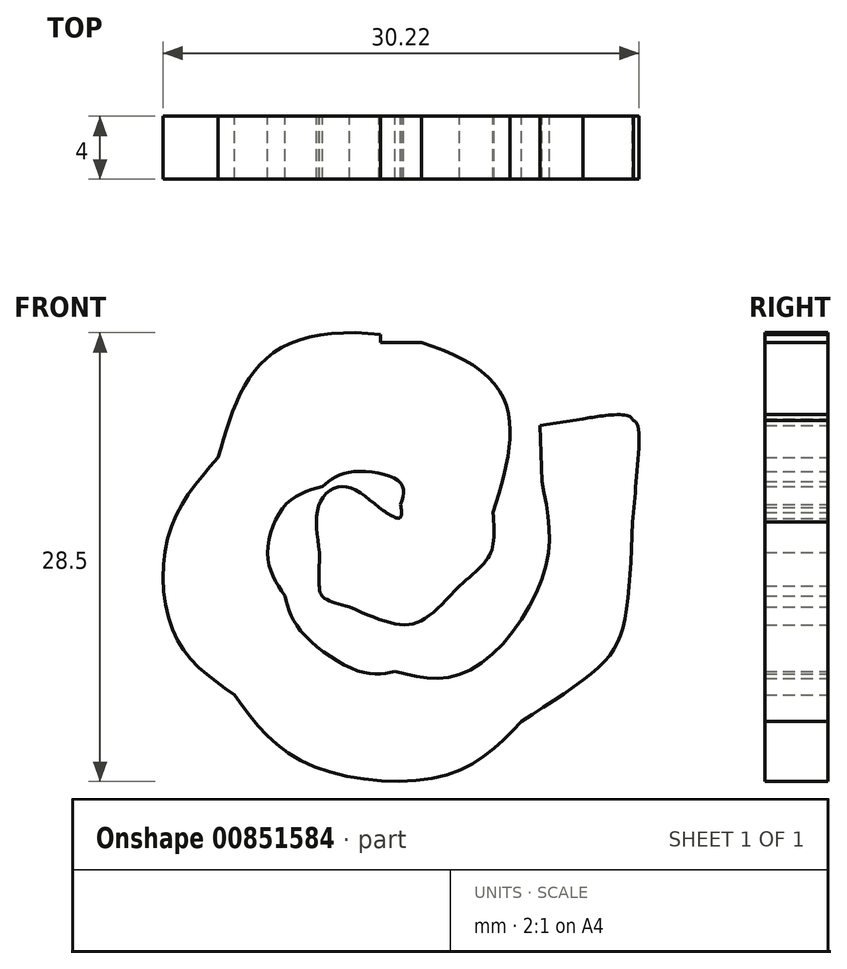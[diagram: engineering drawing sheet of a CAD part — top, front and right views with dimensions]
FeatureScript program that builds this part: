
annotation { "Feature Type Name" : "Feature", "Feature Type Description" : "" }
export const myFeature = defineFeature(function(context is Context, id is Id, definition is map)
    precondition{}
    {
        {
            var Q0;
            Q0=qCreatedBy(makeId("Front.planeOp"),FACE);
            var sketch = newSketch(context, id + "F0", { "sketchPlane" : qUnion([Q0])});
            skLineSegment(sketch, "E0", {"start": v(36.36, -139.97) * mm, "end": v(36.36, -139.97) * mm});
            skLineSegment(sketch, "E1", {"start": v(-25.94, -136.42) * mm, "end": v(-25.94, -136.42) * mm});
            skLineSegment(sketch, "E2", {"start": v(29.93, -128) * mm, "end": v(29.93, -132) * mm});
            skLineSegment(sketch, "E3", {"start": v(-29.93, -128) * mm, "end": v(-29.93, -132) * mm});
            skLineSegment(sketch, "E4", {"start": v(-29.93, -132) * mm, "end": v(29.93, -132) * mm});
            skLineSegment(sketch, "E5", {"start": v(-29.93, -128) * mm, "end": v(29.93, -128) * mm});
            skLineSegment(sketch, "E6", {"start": v(29.93, 122) * mm, "end": v(29.93, 118) * mm});
            skLineSegment(sketch, "E7", {"start": v(-29.93, 122) * mm, "end": v(-29.93, 118) * mm});
            skLineSegment(sketch, "E8", {"start": v(-29.93, 118) * mm, "end": v(29.93, 118) * mm});
            skLineSegment(sketch, "E9", {"start": v(-29.93, 122) * mm, "end": v(29.93, 122) * mm});
            skLineSegment(sketch, "E10", {"start": v(79.92, 150) * mm, "end": v(79.92, -150) * mm});
            skLineSegment(sketch, "E11", {"start": v(-79.92, 150) * mm, "end": v(-79.92, -150) * mm});
            skLineSegment(sketch, "E12", {"start": v(-79.92, -150) * mm, "end": v(79.92, -150) * mm});
            skLineSegment(sketch, "E13", {"start": v(36, -88.2) * mm, "end": v(37.81, -85.02) * mm});
            skLineSegment(sketch, "E14", {"start": v(-79.92, 150) * mm, "end": v(79.92, 150) * mm});
            skLineSegment(sketch, "E15", {"start": v(37.81, -85.02) * mm, "end": v(36.03, -83.85) * mm});
            skLineSegment(sketch, "E16", {"start": v(26.27, -98.72) * mm, "end": v(26.27, -98.72) * mm});
            skLineSegment(sketch, "E17", {"start": v(-42.53, -95.26) * mm, "end": v(-42.53, -95.26) * mm});
            skLineSegment(sketch, "E18", {"start": v(66.59, -95.3) * mm, "end": v(69.78, -95.3) * mm});
            skLineSegment(sketch, "E19", {"start": v(69.78, -95.3) * mm, "end": v(69.78, -92.14) * mm});
            skLineSegment(sketch, "E20", {"start": v(-23.5, -77.49) * mm, "end": v(-23.5, -77.49) * mm});
            skLineSegment(sketch, "E21", {"start": v(69.78, -63.28) * mm, "end": v(69.78, -63.28) * mm});
            skLineSegment(sketch, "E22", {"start": v(49.47, -48.56) * mm, "end": v(57.44, -48.58) * mm});
            skLineSegment(sketch, "E23", {"start": v(57.44, -48.58) * mm, "end": v(61.12, -45.49) * mm});
            skLineSegment(sketch, "E24", {"start": v(61.12, -45.49) * mm, "end": v(61.12, -45.49) * mm});
            skLineSegment(sketch, "E25", {"start": v(-66.72, -40.7) * mm, "end": v(-66.72, -40.7) * mm});
            skLineSegment(sketch, "E26", {"start": v(-6.36, -19.37) * mm, "end": v(-5.74, -15.94) * mm});
            skLineSegment(sketch, "E27", {"start": v(-5.74, -15.94) * mm, "end": v(-10.95, -15.85) * mm});
            skLineSegment(sketch, "E28", {"start": v(-15.96, -40.77) * mm, "end": v(-15.96, -40.77) * mm});
            skLineSegment(sketch, "E29", {"start": v(-39.28, -7.66) * mm, "end": v(-39.78, -2) * mm});
            skLineSegment(sketch, "E30", {"start": v(-39.78, -2) * mm, "end": v(-42.58, -1.59) * mm});
            skLineSegment(sketch, "E31", {"start": v(30.34, -23.6) * mm, "end": v(30.34, -23.6) * mm});
            skLineSegment(sketch, "E32", {"start": v(-30.01, -15.6) * mm, "end": v(-30.01, -15.6) * mm});
            skLineSegment(sketch, "E33", {"start": v(30.85, -8.85) * mm, "end": v(35.62, -7.69) * mm});
            skLineSegment(sketch, "E34", {"start": v(35.62, -7.69) * mm, "end": v(35.42, -4.75) * mm});
            skLineSegment(sketch, "E35", {"start": v(30.85, -8.85) * mm, "end": v(30.85, -8.85) * mm});
            skLineSegment(sketch, "E36", {"start": v(-66.78, 19.45) * mm, "end": v(-70.51, 19.45) * mm});
            skLineSegment(sketch, "E37", {"start": v(-70.51, 19.45) * mm, "end": v(-70.51, 16.65) * mm});
            skLineSegment(sketch, "E38", {"start": v(-21.63, 21.6) * mm, "end": v(-22.15, 15.83) * mm});
            skLineSegment(sketch, "E39", {"start": v(-22.15, 15.83) * mm, "end": v(-20.44, 16.3) * mm});
            skLineSegment(sketch, "E40", {"start": v(66.2, 31.38) * mm, "end": v(69.86, 31.27) * mm});
            skLineSegment(sketch, "E41", {"start": v(69.86, 31.27) * mm, "end": v(69.63, 33.78) * mm});
            skLineSegment(sketch, "E42", {"start": v(69.63, 33.78) * mm, "end": v(69.41, 36.3) * mm});
            skLineSegment(sketch, "E43", {"start": v(69.41, 36.3) * mm, "end": v(64.14, 36.3) * mm});
            skLineSegment(sketch, "E44", {"start": v(48.66, 39.8) * mm, "end": v(46.45, 40.2) * mm});
            skLineSegment(sketch, "E45", {"start": v(46.45, 40.2) * mm, "end": v(46.15, 35.79) * mm});
            skLineSegment(sketch, "E46", {"start": v(-70.51, 31.82) * mm, "end": v(-70.51, 28.39) * mm});
            skLineSegment(sketch, "E47", {"start": v(-70.51, 28.39) * mm, "end": v(-65.19, 28.4) * mm});
            skLineSegment(sketch, "E48", {"start": v(-55.9, 30.29) * mm, "end": v(-55.9, 30.29) * mm});
            skLineSegment(sketch, "E49", {"start": v(-18.1, 31.9) * mm, "end": v(-18.1, 31.9) * mm});
            skLineSegment(sketch, "E50", {"start": v(66.84, 41.57) * mm, "end": v(69.78, 41.53) * mm});
            skLineSegment(sketch, "E51", {"start": v(69.78, 41.53) * mm, "end": v(69.78, 45.61) * mm});
            skLineSegment(sketch, "E52", {"start": v(33.23, 47.48) * mm, "end": v(38.92, 47.78) * mm});
            skLineSegment(sketch, "E53", {"start": v(38.92, 47.78) * mm, "end": v(38.48, 50.36) * mm});
            skLineSegment(sketch, "E54", {"start": v(33.93, 65.25) * mm, "end": v(33.93, 65.25) * mm});
            skLineSegment(sketch, "E55", {"start": v(69.78, 74.16) * mm, "end": v(69.78, 77.16) * mm});
            skLineSegment(sketch, "E56", {"start": v(69.78, 77.16) * mm, "end": v(65.5, 76.74) * mm});
            skLineSegment(sketch, "E57", {"start": v(32.65, 87.45) * mm, "end": v(32.06, 85.77) * mm});
            skLineSegment(sketch, "E58", {"start": v(32.06, 85.77) * mm, "end": v(31.62, 87.42) * mm});
            skLineSegment(sketch, "E59", {"start": v(-17.07, 113.15) * mm, "end": v(-19.78, 112.74) * mm});
            skLineSegment(sketch, "E60", {"start": v(-19.78, 112.74) * mm, "end": v(-19.68, 109.18) * mm});
            skLineSegment(sketch, "E61", {"start": v(68.13, 110) * mm, "end": v(66.47, 112.94) * mm});
            skLineSegment(sketch, "E62", {"start": v(66.47, 112.94) * mm, "end": v(68.13, 115.64) * mm});
            skLineSegment(sketch, "E63", {"start": v(-43.22, 137.14) * mm, "end": v(-44.94, 140.4) * mm});
            skLineSegment(sketch, "E64", {"start": v(-44.94, 140.4) * mm, "end": v(-49.28, 140.4) * mm});
            skLineSegment(sketch, "E65", {"start": v(24.63, 136.8) * mm, "end": v(22.84, 140.4) * mm});
            skLineSegment(sketch, "E66", {"start": v(22.84, 140.4) * mm, "end": v(18.03, 140.4) * mm});
            skLineSegment(sketch, "E67", {"start": v(-2.29, 140.4) * mm, "end": v(-8.25, 140.4) * mm});
            skLineSegment(sketch, "E68", {"start": v(-8.25, 140.4) * mm, "end": v(-7.7, 138.51) * mm});
            skLineSegment(sketch, "E69", {"start": v(-21.3, 140.06) * mm, "end": v(-28.12, 140.06) * mm});
            skLineSegment(sketch, "E70", {"start": v(-28.12, 140.06) * mm, "end": v(-30.35, 137.47) * mm});
            skLineSegment(sketch, "E71", {"start": v(64.64, 137.41) * mm, "end": v(64.64, 140.4) * mm});
            skLineSegment(sketch, "E72", {"start": v(64.64, 140.4) * mm, "end": v(61.7, 140.4) * mm});
            skLineSegment(sketch, "E73", {"start": v(56.95, 136.32) * mm, "end": v(56.95, 136.32) * mm});
            skFitSpline(sketch, "E74", {"points": [v(-44.8, -139.2) * mm, v(-44.8, -136.21) * mm, v(-55.8, -134.8) * mm, v(-60.05, -137.22) * mm]});
            skFitSpline(sketch, "E75", {"points": [v(-60.05, -137.22) * mm, v(-64.45, -139.73) * mm, v(-63.24, -140.32) * mm, v(-53.62, -140.32) * mm]});
            skFitSpline(sketch, "E76", {"points": [v(-53.62, -140.32) * mm, v(-45.94, -140.32) * mm, v(-44.8, -140.18) * mm, v(-44.8, -139.2) * mm]});
            skFitSpline(sketch, "E77", {"points": [v(-34.52, -139.77) * mm, v(-34.52, -138.62) * mm, v(-36.01, -137.23) * mm, v(-37.24, -137.23) * mm]});
            skFitSpline(sketch, "E78", {"points": [v(-37.24, -137.23) * mm, v(-38.23, -137.23) * mm, v(-38.57, -139.4) * mm, v(-37.7, -140.2) * mm]});
            skFitSpline(sketch, "E79", {"points": [v(-37.7, -140.2) * mm, v(-36.84, -141.01) * mm, v(-34.52, -140.7) * mm, v(-34.52, -139.77) * mm]});
            skFitSpline(sketch, "E80", {"points": [v(-8.08, -139.18) * mm, v(-8.08, -137.4) * mm, v(-14.2, -134.92) * mm, v(-17.58, -135.35) * mm]});
            skFitSpline(sketch, "E81", {"points": [v(-17.58, -135.35) * mm, v(-20.96, -135.77) * mm, v(-24.24, -137.67) * mm, v(-24.24, -139.2) * mm]});
            skFitSpline(sketch, "E82", {"points": [v(-24.24, -139.2) * mm, v(-24.24, -140.17) * mm, v(-23.15, -140.32) * mm, v(-16.16, -140.32) * mm]});
            skFitSpline(sketch, "E83", {"points": [v(-16.16, -140.32) * mm, v(-9.12, -140.32) * mm, v(-8.08, -140.17) * mm, v(-8.08, -139.18) * mm]});
            skFitSpline(sketch, "E84", {"points": [v(-1.6, -139.47) * mm, v(-1.98, -137.68) * mm, v(-4.4, -137.48) * mm, v(-4.4, -139.24) * mm]});
            skFitSpline(sketch, "E85", {"points": [v(-4.4, -139.24) * mm, v(-4.4, -140.22) * mm, v(-3.94, -140.66) * mm, v(-2.88, -140.66) * mm]});
            skFitSpline(sketch, "E86", {"points": [v(-2.88, -140.66) * mm, v(-1.83, -140.66) * mm, v(-1.44, -140.3) * mm, v(-1.6, -139.47) * mm]});
            skFitSpline(sketch, "E87", {"points": [v(16.13, -139.33) * mm, v(17.1, -137.64) * mm, v(17.11, -135.85) * mm, v(16.14, -135.85) * mm]});
            skFitSpline(sketch, "E88", {"points": [v(16.14, -135.85) * mm, v(14.72, -135.85) * mm, v(9.5, -139.34) * mm, v(9.93, -140) * mm]});
            skFitSpline(sketch, "E89", {"points": [v(9.93, -140) * mm, v(10.76, -141.25) * mm, v(15.32, -140.76) * mm, v(16.13, -139.33) * mm]});
            skFitSpline(sketch, "E90", {"points": [v(28.28, -138.93) * mm, v(29.71, -137.34) * mm, v(32.67, -135.85) * mm, v(34.41, -135.85) * mm]});
            skFitSpline(sketch, "E91", {"points": [v(34.41, -135.85) * mm, v(35.47, -135.85) * mm, v(37.12, -136.78) * mm, v(38.5, -138.15) * mm]});
            skFitSpline(sketch, "E92", {"points": [v(38.5, -138.15) * mm, v(40.14, -139.78) * mm, v(41.5, -140.46) * mm, v(43.18, -140.5) * mm]});
            skFitSpline(sketch, "E93", {"points": [v(43.18, -140.5) * mm, v(45.3, -140.57) * mm, v(45.54, -140.37) * mm, v(45.54, -138.6) * mm]});
            skFitSpline(sketch, "E94", {"points": [v(45.54, -138.6) * mm, v(45.54, -136.35) * mm, v(42.67, -132.84) * mm, v(39.61, -131.36) * mm]});
            skFitSpline(sketch, "E95", {"points": [v(39.61, -131.36) * mm, v(36.24, -129.73) * mm, v(30.19, -130.06) * mm, v(27.05, -132.05) * mm]});
            skFitSpline(sketch, "E96", {"points": [v(27.05, -132.05) * mm, v(24.23, -133.85) * mm, v(21.3, -137.66) * mm, v(21.3, -139.55) * mm]});
            skFitSpline(sketch, "E97", {"points": [v(21.3, -139.55) * mm, v(21.3, -140.5) * mm, v(21.81, -140.6) * mm, v(24.42, -140.22) * mm]});
            skFitSpline(sketch, "E98", {"points": [v(24.42, -140.22) * mm, v(26.14, -139.96) * mm, v(27.87, -139.38) * mm, v(28.28, -138.93) * mm]});
            skFitSpline(sketch, "E99", {"points": [v(36.36, -139.97) * mm, v(36.92, -139.13) * mm, v(34.9, -138.3) * mm, v(33.81, -138.93) * mm]});
            skFitSpline(sketch, "E100", {"points": [v(33.81, -138.93) * mm, v(33.38, -139.18) * mm, v(33.22, -139.67) * mm, v(33.45, -140.02) * mm]});
            skFitSpline(sketch, "E101", {"points": [v(33.45, -140.02) * mm, v(34.01, -140.87) * mm, v(35.79, -140.84) * mm, v(36.36, -139.97) * mm]});
            skFitSpline(sketch, "E102", {"points": [v(-66.85, -137.74) * mm, v(-64.38, -135.2) * mm, v(-64.05, -133.8) * mm, v(-65.92, -133.78) * mm]});
            skFitSpline(sketch, "E103", {"points": [v(-65.92, -133.78) * mm, v(-66.63, -133.78) * mm, v(-67.95, -133.59) * mm, v(-68.86, -133.36) * mm]});
            skFitSpline(sketch, "E104", {"points": [v(-68.86, -133.36) * mm, v(-70.42, -132.97) * mm, v(-70.51, -133.15) * mm, v(-70.51, -136.46) * mm]});
            skFitSpline(sketch, "E105", {"points": [v(-70.51, -136.46) * mm, v(-70.51, -138.4) * mm, v(-70.18, -139.98) * mm, v(-69.77, -139.98) * mm]});
            skFitSpline(sketch, "E106", {"points": [v(-69.77, -139.98) * mm, v(-69.36, -139.98) * mm, v(-68.05, -138.97) * mm, v(-66.85, -137.74) * mm]});
            skFitSpline(sketch, "E107", {"points": [v(54.12, -138.46) * mm, v(55.46, -138) * mm, v(56.56, -137.32) * mm, v(56.56, -136.93) * mm]});
            skFitSpline(sketch, "E108", {"points": [v(56.56, -136.93) * mm, v(56.56, -135.48) * mm, v(51.75, -126.95) * mm, v(50.92, -126.94) * mm]});
            skFitSpline(sketch, "E109", {"points": [v(50.92, -126.94) * mm, v(50.25, -126.92) * mm, v(47.2, -128.2) * mm, v(44.87, -129.49) * mm]});
            skFitSpline(sketch, "E110", {"points": [v(44.87, -129.49) * mm, v(44.17, -129.87) * mm, v(49.68, -139.2) * mm, v(50.63, -139.25) * mm]});
            skFitSpline(sketch, "E111", {"points": [v(50.63, -139.25) * mm, v(51.2, -139.27) * mm, v(52.78, -138.92) * mm, v(54.12, -138.46) * mm]});
            skFitSpline(sketch, "E112", {"points": [v(-25.94, -136.42) * mm, v(-23.41, -134.2) * mm, v(-23.7, -132.42) * mm, v(-26.57, -132.42) * mm]});
            skFitSpline(sketch, "E113", {"points": [v(-26.57, -132.42) * mm, v(-29.63, -132.42) * mm, v(-34.96, -127.4) * mm, v(-35.67, -123.84) * mm]});
            skFitSpline(sketch, "E114", {"points": [v(-35.67, -123.84) * mm, v(-36.58, -119.29) * mm, v(-32.7, -114.56) * mm, v(-28.04, -114.55) * mm]});
            skFitSpline(sketch, "E115", {"points": [v(-28.04, -114.55) * mm, v(-25.94, -114.55) * mm, v(-22.04, -118.06) * mm, v(-22.04, -119.95) * mm]});
            skFitSpline(sketch, "E116", {"points": [v(-22.04, -119.95) * mm, v(-22.04, -121.63) * mm, v(-23.9, -123.5) * mm, v(-25.58, -123.46) * mm]});
            skFitSpline(sketch, "E117", {"points": [v(-25.58, -123.46) * mm, v(-26.7, -123.44) * mm, v(-26.7, -123.38) * mm, v(-25.52, -122.74) * mm]});
            skFitSpline(sketch, "E118", {"points": [v(-25.52, -122.74) * mm, v(-23.9, -121.85) * mm, v(-23.8, -118.29) * mm, v(-25.4, -117.72) * mm]});
            skFitSpline(sketch, "E119", {"points": [v(-25.4, -117.72) * mm, v(-28.94, -116.44) * mm, v(-32.32, -118.93) * mm, v(-32.32, -122.82) * mm]});
            skFitSpline(sketch, "E120", {"points": [v(-18.36, -125.92) * mm, v(-15.89, -123.41) * mm, v(-15.73, -117.03) * mm, v(-18.06, -114.08) * mm]});
            skFitSpline(sketch, "E121", {"points": [v(-18.06, -114.08) * mm, v(-20.81, -110.61) * mm, v(-24.04, -109.05) * mm, v(-28.48, -109.05) * mm]});
            skFitSpline(sketch, "E122", {"points": [v(-28.48, -109.05) * mm, v(-33.5, -109.05) * mm, v(-36.53, -110.68) * mm, v(-39.61, -115.04) * mm]});
            skFitSpline(sketch, "E123", {"points": [v(-39.61, -115.04) * mm, v(-44.52, -121.97) * mm, v(-41.67, -129.93) * mm, v(-31.95, -136.4) * mm]});
            skFitSpline(sketch, "E124", {"points": [v(-31.95, -136.4) * mm, v(-29.15, -138.27) * mm, v(-28.05, -138.27) * mm, v(-25.94, -136.42) * mm]});
            skFitSpline(sketch, "E125", {"points": [v(69.78, -134.48) * mm, v(69.78, -132.43) * mm, v(69.48, -131.73) * mm, v(68.62, -131.73) * mm]});
            skFitSpline(sketch, "E126", {"points": [v(68.62, -131.73) * mm, v(66.72, -131.73) * mm, v(63.31, -128) * mm, v(62.78, -125.34) * mm]});
            skFitSpline(sketch, "E127", {"points": [v(62.78, -125.34) * mm, v(62.2, -122.41) * mm, v(64.15, -119.3) * mm, v(67.63, -117.61) * mm]});
            skFitSpline(sketch, "E128", {"points": [v(67.63, -117.61) * mm, v(69.38, -116.77) * mm, v(69.78, -116.13) * mm, v(69.78, -114.19) * mm]});
            skFitSpline(sketch, "E129", {"points": [v(69.78, -114.19) * mm, v(69.78, -112.35) * mm, v(69.47, -111.8) * mm, v(68.46, -111.8) * mm]});
            skFitSpline(sketch, "E130", {"points": [v(68.46, -111.8) * mm, v(66.32, -111.8) * mm, v(60.8, -114.75) * mm, v(59.27, -116.7) * mm]});
            skFitSpline(sketch, "E131", {"points": [v(59.27, -116.7) * mm, v(56.34, -120.47) * mm, v(56.77, -129.54) * mm, v(60.05, -133.2) * mm]});
            skFitSpline(sketch, "E132", {"points": [v(60.05, -133.2) * mm, v(62.14, -135.5) * mm, v(65.46, -137.16) * mm, v(68.13, -137.2) * mm]});
            skFitSpline(sketch, "E133", {"points": [v(68.13, -137.2) * mm, v(69.57, -137.22) * mm, v(69.78, -136.88) * mm, v(69.78, -134.48) * mm]});
            skFitSpline(sketch, "E134", {"points": [v(10.65, -133.04) * mm, v(14.55, -130.57) * mm, v(17.16, -125.17) * mm, v(16.74, -120.43) * mm]});
            skFitSpline(sketch, "E135", {"points": [v(16.74, -120.43) * mm, v(16.47, -117.36) * mm, v(15.87, -116.05) * mm, v(13.33, -112.96) * mm]});
            skFitSpline(sketch, "E136", {"points": [v(13.33, -112.96) * mm, v(10.85, -109.96) * mm, v(9.24, -108.8) * mm, v(5.18, -107.1) * mm]});
            skFitSpline(sketch, "E137", {"points": [v(5.18, -107.1) * mm, v(-2.45, -103.9) * mm, v(-3.27, -103.82) * mm, v(-7.2, -105.8) * mm]});
            skFitSpline(sketch, "E138", {"points": [v(-7.2, -105.8) * mm, v(-9.1, -106.75) * mm, v(-12.06, -107.75) * mm, v(-13.77, -108) * mm]});
            skFitSpline(sketch, "E139", {"points": [v(-13.77, -108) * mm, v(-15.49, -108.27) * mm, v(-16.9, -108.7) * mm, v(-16.9, -108.94) * mm]});
            skFitSpline(sketch, "E140", {"points": [v(-16.9, -108.94) * mm, v(-16.92, -109.92) * mm, v(-12.82, -117.95) * mm, v(-12.3, -117.97) * mm]});
            skFitSpline(sketch, "E141", {"points": [v(-12.3, -117.97) * mm, v(-11.98, -117.98) * mm, v(-10.33, -116.64) * mm, v(-8.62, -114.98) * mm]});
            skFitSpline(sketch, "E142", {"points": [v(-8.62, -114.98) * mm, v(-4.52, -111.03) * mm, v(-1.24, -110.39) * mm, v(3.55, -112.62) * mm]});
            skFitSpline(sketch, "E143", {"points": [v(3.55, -112.62) * mm, v(6.95, -114.2) * mm, v(9.93, -117.47) * mm, v(10.75, -120.54) * mm]});
            skFitSpline(sketch, "E144", {"points": [v(10.75, -120.54) * mm, v(11.4, -122.96) * mm, v(9.63, -126.16) * mm, v(6.58, -128.05) * mm]});
            skFitSpline(sketch, "E145", {"points": [v(6.58, -128.05) * mm, v(3.97, -129.67) * mm, v(3.7, -129.7) * mm, v(1.18, -128.71) * mm]});
            skFitSpline(sketch, "E146", {"points": [v(1.18, -128.71) * mm, v(-2.1, -127.43) * mm, v(-3.53, -124.9) * mm, v(-2.34, -122.45) * mm]});
            skFitSpline(sketch, "E147", {"points": [v(-2.34, -122.45) * mm, v(-1.88, -121.5) * mm, v(-0.93, -120.73) * mm, v(-0.24, -120.73) * mm]});
            skFitSpline(sketch, "E148", {"points": [v(-0.24, -120.73) * mm, v(0.75, -120.73) * mm, v(0.83, -120.92) * mm, v(0.15, -121.56) * mm]});
            skFitSpline(sketch, "E149", {"points": [v(0.15, -121.56) * mm, v(-0.34, -122.01) * mm, v(-0.73, -123.24) * mm, v(-0.73, -124.3) * mm]});
            skFitSpline(sketch, "E150", {"points": [v(-0.73, -124.3) * mm, v(-0.73, -128.48) * mm, v(5.94, -127.14) * mm, v(6.87, -122.77) * mm]});
            skFitSpline(sketch, "E151", {"points": [v(6.87, -122.77) * mm, v(8.06, -117.23) * mm, v(2.16, -113) * mm, v(-3.34, -115.46) * mm]});
            skFitSpline(sketch, "E152", {"points": [v(-3.34, -115.46) * mm, v(-8.23, -117.64) * mm, v(-10.35, -124.2) * mm, v(-7.71, -128.98) * mm]});
            skFitSpline(sketch, "E153", {"points": [v(-7.71, -128.98) * mm, v(-6.51, -131.15) * mm, v(-2.7, -134.12) * mm, v(-0.37, -134.7) * mm]});
            skFitSpline(sketch, "E154", {"points": [v(-0.37, -134.7) * mm, v(2.72, -135.49) * mm, v(8.05, -134.68) * mm, v(10.65, -133.04) * mm]});
            skFitSpline(sketch, "E155", {"points": [v(-42.6, -132.59) * mm, v(-42.61, -132.3) * mm, v(-43.43, -130.53) * mm, v(-44.42, -128.64) * mm]});
            skFitSpline(sketch, "E156", {"points": [v(-44.42, -128.64) * mm, v(-45.41, -126.75) * mm, v(-46.24, -124.81) * mm, v(-46.25, -124.34) * mm]});
            skFitSpline(sketch, "E157", {"points": [v(-46.25, -124.34) * mm, v(-46.28, -123.35) * mm, v(-48.48, -123.15) * mm, v(-48.48, -124.15) * mm]});
            skFitSpline(sketch, "E158", {"points": [v(-48.48, -124.15) * mm, v(-48.48, -124.51) * mm, v(-49.47, -125.87) * mm, v(-50.68, -127.16) * mm]});
            skFitSpline(sketch, "E159", {"points": [v(-50.68, -127.16) * mm, v(-53.41, -130.07) * mm, v(-53.46, -131.03) * mm, v(-50.86, -131.07) * mm]});
            skFitSpline(sketch, "E160", {"points": [v(-50.86, -131.07) * mm, v(-49.75, -131.1) * mm, v(-47.85, -131.53) * mm, v(-46.64, -132.05) * mm]});
            skFitSpline(sketch, "E161", {"points": [v(-46.64, -132.05) * mm, v(-44.11, -133.13) * mm, v(-42.6, -133.33) * mm, v(-42.6, -132.59) * mm]});
            skFitSpline(sketch, "E162", {"points": [v(25.96, -128.25) * mm, v(28.43, -125.78) * mm, v(28.35, -125.09) * mm, v(25.35, -123.31) * mm]});
            skFitSpline(sketch, "E163", {"points": [v(25.35, -123.31) * mm, v(22.99, -120.8) * mm, v(22.31, -120.93) * mm, v(21.8, -124) * mm]});
            skFitSpline(sketch, "E164", {"points": [v(21.8, -124) * mm, v(21.57, -125.42) * mm, v(21.16, -127.27) * mm, v(20.89, -128.12) * mm]});
            skFitSpline(sketch, "E165", {"points": [v(-57.95, -127.41) * mm, v(-54.6, -125.3) * mm, v(-51.45, -119.84) * mm, v(-51.43, -116.07) * mm]});
            skFitSpline(sketch, "E166", {"points": [v(-51.43, -116.07) * mm, v(-51.4, -109.92) * mm, v(-56.36, -104.23) * mm, v(-64.32, -101.31) * mm]});
            skFitSpline(sketch, "E167", {"points": [v(-64.32, -101.31) * mm, v(-67.14, -100.28) * mm, v(-69.69, -99.43) * mm, v(-69.98, -99.43) * mm]});
            skFitSpline(sketch, "E168", {"points": [v(-69.98, -99.43) * mm, v(-70.27, -99.43) * mm, v(-70.51, -100.98) * mm, v(-70.51, -102.87) * mm]});
            skFitSpline(sketch, "E169", {"points": [v(-70.51, -102.87) * mm, v(-70.51, -106.24) * mm, v(-70.47, -106.3) * mm, v(-68.27, -106.3) * mm]});
            skFitSpline(sketch, "E170", {"points": [v(-68.27, -106.3) * mm, v(-65.03, -106.3) * mm, v(-61.98, -108.01) * mm, v(-59.48, -111.24) * mm]});
            skFitSpline(sketch, "E171", {"points": [v(-59.48, -111.24) * mm, v(-56.92, -114.54) * mm, v(-56.74, -116.64) * mm, v(-58.74, -119.67) * mm]});
            skFitSpline(sketch, "E172", {"points": [v(-58.74, -119.67) * mm, v(-61.2, -123.4) * mm, v(-63.4, -124) * mm, v(-68.86, -122.43) * mm]});
            skFitSpline(sketch, "E173", {"points": [v(-68.86, -122.43) * mm, v(-70.4, -121.98) * mm, v(-70.51, -122.15) * mm, v(-70.51, -125.06) * mm]});
            skFitSpline(sketch, "E174", {"points": [v(-70.51, -125.06) * mm, v(-70.51, -128.66) * mm, v(-70.21, -128.85) * mm, v(-64.56, -128.93) * mm]});
            skFitSpline(sketch, "E175", {"points": [v(-64.56, -128.93) * mm, v(-61.43, -128.97) * mm, v(-59.85, -128.6) * mm, v(-57.95, -127.41) * mm]});
            skFitSpline(sketch, "E176", {"points": [v(69.78, -124.86) * mm, v(69.78, -121.7) * mm, v(69.53, -120.73) * mm, v(68.7, -120.73) * mm]});
            skFitSpline(sketch, "E177", {"points": [v(68.7, -120.73) * mm, v(66.66, -120.73) * mm, v(65.38, -125.03) * mm, v(66.55, -127.9) * mm]});
            skFitSpline(sketch, "E178", {"points": [v(66.55, -127.9) * mm, v(66.8, -128.5) * mm, v(67.62, -128.98) * mm, v(68.39, -128.98) * mm]});
            skFitSpline(sketch, "E179", {"points": [v(68.39, -128.98) * mm, v(69.6, -128.98) * mm, v(69.78, -128.45) * mm, v(69.78, -124.86) * mm]});
            skFitSpline(sketch, "E180", {"points": [v(48.78, -123.28) * mm, v(50.92, -122.17) * mm, v(52.28, -120.7) * mm, v(53.9, -117.7) * mm]});
            skFitSpline(sketch, "E181", {"points": [v(53.9, -117.7) * mm, v(55.37, -114.99) * mm, v(57.14, -112.96) * mm, v(59.27, -111.56) * mm]});
            skFitSpline(sketch, "E182", {"points": [v(59.27, -111.56) * mm, v(61, -110.41) * mm, v(62.43, -109.13) * mm, v(62.43, -108.71) * mm]});
            skFitSpline(sketch, "E183", {"points": [v(62.43, -108.71) * mm, v(62.43, -108.3) * mm, v(60.8, -107.4) * mm, v(58.8, -106.73) * mm]});
            skFitSpline(sketch, "E184", {"points": [v(58.8, -106.73) * mm, v(56.8, -106.06) * mm, v(54.78, -105.07) * mm, v(54.3, -104.53) * mm]});
            skFitSpline(sketch, "E185", {"points": [v(54.3, -104.53) * mm, v(53.83, -104) * mm, v(52.96, -103.55) * mm, v(52.37, -103.55) * mm]});
            skFitSpline(sketch, "E186", {"points": [v(52.37, -103.55) * mm, v(51.52, -103.55) * mm, v(51.4, -104.27) * mm, v(51.8, -107.23) * mm]});
            skFitSpline(sketch, "E187", {"points": [v(51.8, -107.23) * mm, v(52.64, -113.53) * mm, v(48.58, -118.79) * mm, v(42.16, -119.73) * mm]});
            skFitSpline(sketch, "E188", {"points": [v(42.16, -119.73) * mm, v(40.58, -119.97) * mm, v(38.39, -119.83) * mm, v(37.28, -119.43) * mm]});
            skFitSpline(sketch, "E189", {"points": [v(37.28, -119.43) * mm, v(33.46, -118.06) * mm, v(31.16, -112.36) * mm, v(33.07, -109.01) * mm]});
            skFitSpline(sketch, "E190", {"points": [v(33.07, -109.01) * mm, v(34.07, -107.27) * mm, v(37.93, -105.44) * mm, v(39.58, -105.94) * mm]});
            skFitSpline(sketch, "E191", {"points": [v(39.58, -105.94) * mm, v(41.31, -106.45) * mm, v(42.95, -109.35) * mm, v(42.17, -110.53) * mm]});
            skFitSpline(sketch, "E192", {"points": [v(42.17, -110.53) * mm, v(41.73, -111.2) * mm, v(41.45, -110.98) * mm, v(41.13, -109.73) * mm]});
            skFitSpline(sketch, "E193", {"points": [v(41.13, -109.73) * mm, v(40.6, -107.58) * mm, v(37.6, -107) * mm, v(36.22, -108.77) * mm]});
            skFitSpline(sketch, "E194", {"points": [v(36.22, -108.77) * mm, v(33.7, -112) * mm, v(36.63, -116.61) * mm, v(41.2, -116.61) * mm]});
            skFitSpline(sketch, "E195", {"points": [v(41.2, -116.61) * mm, v(46.26, -116.61) * mm, v(49.09, -113.34) * mm, v(48.13, -108.57) * mm]});
            skFitSpline(sketch, "E196", {"points": [v(48.13, -108.57) * mm, v(46.97, -102.76) * mm, v(44.09, -100.43) * mm, v(38.2, -100.51) * mm]});
            skFitSpline(sketch, "E197", {"points": [v(38.2, -100.51) * mm, v(34.02, -100.57) * mm, v(30.4, -102.4) * mm, v(28.03, -105.65) * mm]});
            skFitSpline(sketch, "E198", {"points": [v(28.03, -105.65) * mm, v(26.56, -107.68) * mm, v(26.35, -108.68) * mm, v(26.58, -112.63) * mm]});
            skFitSpline(sketch, "E199", {"points": [v(26.58, -112.63) * mm, v(26.8, -116.4) * mm, v(27.26, -117.78) * mm, v(29.05, -120.19) * mm]});
            skFitSpline(sketch, "E200", {"points": [v(29.05, -120.19) * mm, v(32.26, -124.49) * mm, v(35.24, -125.73) * mm, v(41.12, -125.2) * mm]});
            skFitSpline(sketch, "E201", {"points": [v(41.12, -125.2) * mm, v(43.9, -124.96) * mm, v(47.08, -124.16) * mm, v(48.78, -123.28) * mm]});
            skFitSpline(sketch, "E202", {"points": [v(-62.34, -119.6) * mm, v(-61.78, -118.97) * mm, v(-61.33, -117.13) * mm, v(-61.33, -115.5) * mm]});
            skFitSpline(sketch, "E203", {"points": [v(-61.33, -115.5) * mm, v(-61.33, -111.65) * mm, v(-63.38, -109.6) * mm, v(-67.32, -109.48) * mm]});
            skFitSpline(sketch, "E204", {"points": [v(-67.32, -109.48) * mm, v(-70.13, -109.4) * mm, v(-70.15, -109.4) * mm, v(-70.37, -112.32) * mm]});
            skFitSpline(sketch, "E205", {"points": [v(-70.37, -112.32) * mm, v(-70.57, -114.87) * mm, v(-70.4, -115.24) * mm, v(-69.1, -115.24) * mm]});
            skFitSpline(sketch, "E206", {"points": [v(-69.1, -115.24) * mm, v(-67.78, -115.24) * mm, v(-67.7, -115.44) * mm, v(-68.42, -116.91) * mm]});
            skFitSpline(sketch, "E207", {"points": [v(-68.42, -116.91) * mm, v(-68.87, -117.83) * mm, v(-69.04, -119.07) * mm, v(-68.8, -119.66) * mm]});
            skFitSpline(sketch, "E208", {"points": [v(-68.8, -119.66) * mm, v(-68.2, -121.12) * mm, v(-63.65, -121.08) * mm, v(-62.34, -119.6) * mm]});
            skFitSpline(sketch, "E209", {"points": [v(-44.8, -113.86) * mm, v(-44.8, -113.49) * mm, v(-43.59, -111.92) * mm, v(-42.1, -110.38) * mm]});
            skFitSpline(sketch, "E210", {"points": [v(-42.1, -110.38) * mm, v(-39.35, -107.53) * mm, v(-35.79, -105.5) * mm, v(-32.13, -104.67) * mm]});
            skFitSpline(sketch, "E211", {"points": [v(-32.13, -104.67) * mm, v(-29.44, -104.06) * mm, v(-29.59, -103.09) * mm, v(-32.83, -99.98) * mm]});
            skFitSpline(sketch, "E212", {"points": [v(-32.83, -99.98) * mm, v(-35.95, -97) * mm, v(-36.86, -96.83) * mm, v(-39.48, -98.76) * mm]});
            skFitSpline(sketch, "E213", {"points": [v(-39.48, -98.76) * mm, v(-42.08, -100.67) * mm, v(-48.74, -102.39) * mm, v(-51.43, -101.83) * mm]});
            skFitSpline(sketch, "E214", {"points": [v(-51.43, -101.83) * mm, v(-54.27, -101.25) * mm, v(-54.23, -102.1) * mm, v(-51.22, -105.8) * mm]});
            skFitSpline(sketch, "E215", {"points": [v(-51.22, -105.8) * mm, v(-49.9, -107.4) * mm, v(-48.36, -110.04) * mm, v(-47.8, -111.64) * mm]});
            skFitSpline(sketch, "E216", {"points": [v(-47.8, -111.64) * mm, v(-47.24, -113.24) * mm, v(-46.33, -114.55) * mm, v(-45.79, -114.55) * mm]});
            skFitSpline(sketch, "E217", {"points": [v(-45.79, -114.55) * mm, v(-45.25, -114.55) * mm, v(-44.8, -114.24) * mm, v(-44.8, -113.86) * mm]});
            skFitSpline(sketch, "E218", {"points": [v(21.55, -111.29) * mm, v(21.8, -109.5) * mm, v(22.2, -107.38) * mm, v(22.43, -106.6) * mm]});
            skFitSpline(sketch, "E219", {"points": [v(22.43, -106.6) * mm, v(22.84, -105.27) * mm, v(22.57, -105.19) * mm, v(18.05, -105.19) * mm]});
            skFitSpline(sketch, "E220", {"points": [v(18.05, -105.19) * mm, v(13.88, -105.19) * mm, v(13.22, -105.36) * mm, v(13.22, -106.43) * mm]});
            skFitSpline(sketch, "E221", {"points": [v(13.22, -106.43) * mm, v(13.22, -107.12) * mm, v(13.51, -107.68) * mm, v(13.86, -107.68) * mm]});
            skFitSpline(sketch, "E222", {"points": [v(13.86, -107.68) * mm, v(14.22, -107.68) * mm, v(15.62, -109.22) * mm, v(16.99, -111.1) * mm]});
            skFitSpline(sketch, "E223", {"points": [v(16.99, -111.1) * mm, v(18.35, -112.98) * mm, v(19.83, -114.52) * mm, v(20.28, -114.53) * mm]});
            skFitSpline(sketch, "E224", {"points": [v(20.28, -114.53) * mm, v(20.73, -114.54) * mm, v(21.3, -113.08) * mm, v(21.55, -111.29) * mm]});
            skFitSpline(sketch, "E225", {"points": [v(-12.38, -103.54) * mm, v(-6.82, -102.1) * mm, v(-2.31, -94.9) * mm, v(-3.18, -88.85) * mm]});
            skFitSpline(sketch, "E226", {"points": [v(-3.18, -88.85) * mm, v(-4.2, -81.69) * mm, v(-13.12, -77.28) * mm, v(-19.93, -80.58) * mm]});
            skFitSpline(sketch, "E227", {"points": [v(-19.93, -80.58) * mm, v(-24.29, -82.69) * mm, v(-25.79, -90.49) * mm, v(-22.44, -93.62) * mm]});
            skFitSpline(sketch, "E228", {"points": [v(-22.44, -93.62) * mm, v(-19.85, -96.04) * mm, v(-15.36, -95.98) * mm, v(-13.27, -93.5) * mm]});
            skFitSpline(sketch, "E229", {"points": [v(-13.27, -93.5) * mm, v(-11.45, -91.33) * mm, v(-11.32, -88.94) * mm, v(-12.94, -87.42) * mm]});
            skFitSpline(sketch, "E230", {"points": [v(-12.94, -87.42) * mm, v(-14.5, -85.97) * mm, v(-16.28, -86.33) * mm, v(-17.33, -88.3) * mm]});
            skFitSpline(sketch, "E231", {"points": [v(-17.33, -88.3) * mm, v(-18.03, -89.63) * mm, v(-18.25, -89.7) * mm, v(-18.63, -88.78) * mm]});
            skFitSpline(sketch, "E232", {"points": [v(-18.63, -88.78) * mm, v(-19.1, -87.61) * mm, v(-16.17, -84.31) * mm, v(-14.65, -84.31) * mm]});
            skFitSpline(sketch, "E233", {"points": [v(-14.65, -84.31) * mm, v(-12.98, -84.31) * mm, v(-8.81, -88.95) * mm, v(-8.81, -90.8) * mm]});
            skFitSpline(sketch, "E234", {"points": [v(-8.81, -90.8) * mm, v(-8.81, -93.54) * mm, v(-10.76, -96.52) * mm, v(-13.35, -97.77) * mm]});
            skFitSpline(sketch, "E235", {"points": [v(-13.35, -97.77) * mm, v(-20.39, -101.18) * mm, v(-29.5, -93.36) * mm, v(-28.28, -84.98) * mm]});
            skFitSpline(sketch, "E236", {"points": [v(-28.28, -84.98) * mm, v(-27.88, -82.32) * mm, v(-28.06, -81.28) * mm, v(-29.13, -79.9) * mm]});
            skFitSpline(sketch, "E237", {"points": [v(-29.13, -79.9) * mm, v(-31.55, -76.8) * mm, v(-32.41, -77.63) * mm, v(-31.88, -82.52) * mm]});
            skFitSpline(sketch, "E238", {"points": [v(-31.88, -82.52) * mm, v(-31.52, -85.81) * mm, v(-31.72, -87.88) * mm, v(-32.7, -90.78) * mm]});
            skFitSpline(sketch, "E239", {"points": [v(-32.7, -90.78) * mm, v(-33.95, -94.51) * mm, v(-33.95, -94.69) * mm, v(-32.62, -96.06) * mm]});
            skFitSpline(sketch, "E240", {"points": [v(-32.62, -96.06) * mm, v(-28.46, -100.37) * mm, v(-22.6, -103.13) * mm, v(-15.42, -104.18) * mm]});
            skFitSpline(sketch, "E241", {"points": [v(-15.42, -104.18) * mm, v(-15.22, -104.2) * mm, v(-13.85, -103.92) * mm, v(-12.38, -103.54) * mm]});
            skFitSpline(sketch, "E242", {"points": [v(68.86, -103.56) * mm, v(69.42, -103.56) * mm, v(69.78, -102.61) * mm, v(69.78, -101.15) * mm]});
            skFitSpline(sketch, "E243", {"points": [v(69.78, -101.15) * mm, v(69.78, -98.86) * mm, v(69.65, -98.74) * mm, v(67.23, -98.74) * mm]});
            skFitSpline(sketch, "E244", {"points": [v(67.23, -98.74) * mm, v(63.48, -98.74) * mm, v(59.86, -96.84) * mm, v(58.13, -93.96) * mm]});
            skFitSpline(sketch, "E245", {"points": [v(58.13, -93.96) * mm, v(56.86, -91.84) * mm, v(56.73, -91.01) * mm, v(57.34, -88.93) * mm]});
            skFitSpline(sketch, "E246", {"points": [v(57.34, -88.93) * mm, v(58.62, -84.58) * mm, v(64.45, -81.96) * mm, v(66.84, -84.66) * mm]});
            skFitSpline(sketch, "E247", {"points": [v(66.84, -84.66) * mm, v(68.63, -86.67) * mm, v(69.78, -85.86) * mm, v(69.78, -82.58) * mm]});
            skFitSpline(sketch, "E248", {"points": [v(69.78, -82.58) * mm, v(69.78, -79.87) * mm, v(69.53, -79.38) * mm, v(67.9, -78.8) * mm]});
            skFitSpline(sketch, "E249", {"points": [v(67.9, -78.8) * mm, v(63.29, -77.16) * mm, v(57.72, -78.5) * mm, v(54.07, -82.13) * mm]});
            skFitSpline(sketch, "E250", {"points": [v(54.07, -82.13) * mm, v(49.74, -86.44) * mm, v(50.97, -98.01) * mm, v(56.1, -101.16) * mm]});
            skFitSpline(sketch, "E251", {"points": [v(56.1, -101.16) * mm, v(58.54, -102.65) * mm, v(64.6, -104.23) * mm, v(66.47, -103.86) * mm]});
            skFitSpline(sketch, "E252", {"points": [v(66.47, -103.86) * mm, v(67.28, -103.7) * mm, v(68.35, -103.57) * mm, v(68.86, -103.56) * mm]});
            skFitSpline(sketch, "E253", {"points": [v(5.88, -100.78) * mm, v(5.88, -99.64) * mm, v(2.75, -96) * mm, v(1.78, -96) * mm]});
            skFitSpline(sketch, "E254", {"points": [v(1.78, -96) * mm, v(0.87, -96) * mm, v(0, -97.49) * mm, v(0, -99.04) * mm]});
            skFitSpline(sketch, "E255", {"points": [v(0, -99.04) * mm, v(0, -100) * mm, v(2.6, -101.37) * mm, v(4.6, -101.45) * mm]});
            skFitSpline(sketch, "E256", {"points": [v(4.6, -101.45) * mm, v(5.3, -101.47) * mm, v(5.88, -101.17) * mm, v(5.88, -100.78) * mm]});
            skFitSpline(sketch, "E257", {"points": [v(26.27, -98.72) * mm, v(30.25, -96.58) * mm, v(32.85, -93.77) * mm, v(36, -88.2) * mm]});
            skFitSpline(sketch, "E258", {"points": [v(36.03, -83.85) * mm, v(35.05, -83.2) * mm, v(33.65, -82.12) * mm, v(32.91, -81.43) * mm]});
            skFitSpline(sketch, "E259", {"points": [v(32.91, -81.43) * mm, v(30.8, -79.47) * mm, v(30.11, -79.95) * mm, v(30.11, -83.4) * mm]});
            skFitSpline(sketch, "E260", {"points": [v(30.11, -83.4) * mm, v(30.11, -89.29) * mm, v(24.35, -95.3) * mm, v(18.72, -95.3) * mm]});
            skFitSpline(sketch, "E261", {"points": [v(18.72, -95.3) * mm, v(16.5, -95.3) * mm, v(11.82, -91.28) * mm, v(11.67, -89.25) * mm]});
            skFitSpline(sketch, "E262", {"points": [v(11.67, -89.25) * mm, v(11.41, -85.74) * mm, v(13.29, -82.76) * mm, v(16.33, -81.86) * mm]});
            skFitSpline(sketch, "E263", {"points": [v(16.33, -81.86) * mm, v(17.92, -81.38) * mm, v(20.57, -83.26) * mm, v(20.57, -84.87) * mm]});
            skFitSpline(sketch, "E264", {"points": [v(20.57, -84.87) * mm, v(20.57, -85.73) * mm, v(20.33, -85.7) * mm, v(19.15, -84.7) * mm]});
            skFitSpline(sketch, "E265", {"points": [v(19.15, -84.7) * mm, v(16.82, -82.73) * mm, v(15.1, -83.56) * mm, v(14.84, -86.78) * mm]});
            skFitSpline(sketch, "E266", {"points": [v(14.84, -86.78) * mm, v(14.58, -90.02) * mm, v(15.54, -91.07) * mm, v(19.26, -91.63) * mm]});
            skFitSpline(sketch, "E267", {"points": [v(19.26, -91.63) * mm, v(21.25, -91.93) * mm, v(22.22, -91.64) * mm, v(24.1, -90.16) * mm]});
            skFitSpline(sketch, "E268", {"points": [v(24.1, -90.16) * mm, v(26.13, -88.56) * mm, v(26.44, -87.88) * mm, v(26.44, -85.03) * mm]});
            skFitSpline(sketch, "E269", {"points": [v(26.44, -85.03) * mm, v(26.44, -82.25) * mm, v(26.06, -81.34) * mm, v(23.98, -79.22) * mm]});
            skFitSpline(sketch, "E270", {"points": [v(23.98, -79.22) * mm, v(14.84, -69.89) * mm, v(0.2, -83.45) * mm, v(7.4, -94.55) * mm]});
            skFitSpline(sketch, "E271", {"points": [v(7.4, -94.55) * mm, v(8.18, -95.74) * mm, v(10.36, -97.63) * mm, v(12.26, -98.76) * mm]});
            skFitSpline(sketch, "E272", {"points": [v(12.26, -98.76) * mm, v(16.95, -101.54) * mm, v(21.03, -101.53) * mm, v(26.27, -98.72) * mm]});
            skFitSpline(sketch, "E273", {"points": [v(47.4, -97.2) * mm, v(47.12, -96.35) * mm, v(46.54, -94.1) * mm, v(46.12, -92.22) * mm]});
            skFitSpline(sketch, "E274", {"points": [v(46.12, -92.22) * mm, v(45.7, -90.33) * mm, v(44.83, -88.4) * mm, v(44.2, -87.92) * mm]});
            skFitSpline(sketch, "E275", {"points": [v(44.2, -87.92) * mm, v(41.85, -86.16) * mm, v(40.53, -86.94) * mm, v(38.23, -91.45) * mm]});
            skFitSpline(sketch, "E276", {"points": [v(38.23, -91.45) * mm, v(37, -93.87) * mm, v(36, -96.04) * mm, v(36, -96.27) * mm]});
            skFitSpline(sketch, "E277", {"points": [v(36, -96.27) * mm, v(36, -96.5) * mm, v(37.06, -96.7) * mm, v(38.38, -96.72) * mm]});
            skFitSpline(sketch, "E278", {"points": [v(38.38, -96.72) * mm, v(39.7, -96.74) * mm, v(41.92, -97.17) * mm, v(43.34, -97.67) * mm]});
            skFitSpline(sketch, "E279", {"points": [v(43.34, -97.67) * mm, v(47.28, -99.07) * mm, v(48, -98.98) * mm, v(47.4, -97.2) * mm]});
            skFitSpline(sketch, "E280", {"points": [v(-60.96, -96.75) * mm, v(-60.96, -96.41) * mm, v(-61.79, -94.79) * mm, v(-62.8, -93.14) * mm]});
            skFitSpline(sketch, "E281", {"points": [v(-62.8, -93.14) * mm, v(-63.8, -91.5) * mm, v(-64.62, -89.61) * mm, v(-64.63, -88.95) * mm]});
            skFitSpline(sketch, "E282", {"points": [v(-64.63, -88.95) * mm, v(-64.64, -87.45) * mm, v(-66.34, -87.4) * mm, v(-68.7, -88.86) * mm]});
            skFitSpline(sketch, "E283", {"points": [v(-68.7, -88.86) * mm, v(-70, -89.65) * mm, v(-70.51, -90.59) * mm, v(-70.5, -92.12) * mm]});
            skFitSpline(sketch, "E284", {"points": [v(-70.5, -92.12) * mm, v(-70.5, -94.07) * mm, v(-70.13, -94.41) * mm, v(-66.65, -95.74) * mm]});
            skFitSpline(sketch, "E285", {"points": [v(-66.65, -95.74) * mm, v(-62.27, -97.4) * mm, v(-60.96, -97.64) * mm, v(-60.96, -96.75) * mm]});
            skFitSpline(sketch, "E286", {"points": [v(-42.53, -95.26) * mm, v(-39.46, -93.21) * mm, v(-36.78, -89) * mm, v(-36.25, -85.35) * mm]});
            skFitSpline(sketch, "E287", {"points": [v(-36.25, -85.35) * mm, v(-35.69, -81.55) * mm, v(-38.4, -75.88) * mm, v(-42.3, -72.68) * mm]});
            skFitSpline(sketch, "E288", {"points": [v(-42.3, -72.68) * mm, v(-45.65, -69.92) * mm, v(-51.58, -67.13) * mm, v(-54.1, -67.13) * mm]});
            skFitSpline(sketch, "E289", {"points": [v(-54.1, -67.13) * mm, v(-55.2, -67.13) * mm, v(-57.54, -66.48) * mm, v(-59.3, -65.68) * mm]});
            skFitSpline(sketch, "E290", {"points": [v(-59.3, -65.68) * mm, v(-61.07, -64.88) * mm, v(-62.73, -64.43) * mm, v(-62.99, -64.68) * mm]});
            skFitSpline(sketch, "E291", {"points": [v(-62.99, -64.68) * mm, v(-63.25, -64.92) * mm, v(-63.04, -66.12) * mm, v(-62.51, -67.33) * mm]});
            skFitSpline(sketch, "E292", {"points": [v(-62.51, -67.33) * mm, v(-61.99, -68.54) * mm, v(-61.23, -70.85) * mm, v(-60.83, -72.46) * mm]});
            skFitSpline(sketch, "E293", {"points": [v(-60.83, -72.46) * mm, v(-60.44, -74.06) * mm, v(-59.85, -75.38) * mm, v(-59.53, -75.38) * mm]});
            skFitSpline(sketch, "E294", {"points": [v(-59.53, -75.38) * mm, v(-59.2, -75.38) * mm, v(-57.7, -74.9) * mm, v(-56.17, -74.3) * mm]});
            skFitSpline(sketch, "E295", {"points": [v(-56.17, -74.3) * mm, v(-53.63, -73.3) * mm, v(-53.13, -73.3) * mm, v(-50.22, -74.34) * mm]});
            skFitSpline(sketch, "E296", {"points": [v(-50.22, -74.34) * mm, v(-46.49, -75.68) * mm, v(-43.7, -78.52) * mm, v(-42.52, -82.23) * mm]});
            skFitSpline(sketch, "E297", {"points": [v(-42.52, -82.23) * mm, v(-41.79, -84.53) * mm, v(-41.86, -85.2) * mm, v(-43.05, -87.1) * mm]});
            skFitSpline(sketch, "E298", {"points": [v(-43.05, -87.1) * mm, v(-43.81, -88.32) * mm, v(-45.56, -89.87) * mm, v(-46.92, -90.56) * mm]});
            skFitSpline(sketch, "E299", {"points": [v(-46.92, -90.56) * mm, v(-49.07, -91.63) * mm, v(-49.73, -91.68) * mm, v(-51.7, -90.93) * mm]});
            skFitSpline(sketch, "E300", {"points": [v(-51.7, -90.93) * mm, v(-54.87, -89.72) * mm, v(-56.4, -87.06) * mm, v(-55.25, -84.72) * mm]});
            skFitSpline(sketch, "E301", {"points": [v(-55.25, -84.72) * mm, v(-54.78, -83.74) * mm, v(-53.84, -82.94) * mm, v(-53.18, -82.94) * mm]});
            skFitSpline(sketch, "E302", {"points": [v(-53.18, -82.94) * mm, v(-52.2, -82.94) * mm, v(-52.14, -83.13) * mm, v(-52.85, -83.93) * mm]});
            skFitSpline(sketch, "E303", {"points": [v(-52.85, -83.93) * mm, v(-54.03, -85.26) * mm, v(-53.56, -87.77) * mm, v(-51.96, -88.7) * mm]});
            skFitSpline(sketch, "E304", {"points": [v(-51.96, -88.7) * mm, v(-50.98, -89.28) * mm, v(-50.2, -89.22) * mm, v(-48.71, -88.44) * mm]});
            skFitSpline(sketch, "E305", {"points": [v(-48.71, -88.44) * mm, v(-43.13, -85.49) * mm, v(-45.97, -76.75) * mm, v(-52.51, -76.75) * mm]});
            skFitSpline(sketch, "E306", {"points": [v(-52.51, -76.75) * mm, v(-54.56, -76.75) * mm, v(-55.83, -77.35) * mm, v(-58.24, -79.45) * mm]});
            skFitSpline(sketch, "E307", {"points": [v(-58.24, -79.45) * mm, v(-61.19, -82.03) * mm, v(-61.33, -82.34) * mm, v(-61.33, -86.15) * mm]});
            skFitSpline(sketch, "E308", {"points": [v(-61.33, -86.15) * mm, v(-61.33, -91.03) * mm, v(-59.3, -94.13) * mm, v(-54.8, -96.1) * mm]});
            skFitSpline(sketch, "E309", {"points": [v(-54.8, -96.1) * mm, v(-51.04, -97.75) * mm, v(-45.72, -97.38) * mm, v(-42.53, -95.26) * mm]});
            skFitSpline(sketch, "E310", {"points": [v(69.78, -92.14) * mm, v(69.78, -89.33) * mm, v(69.61, -89) * mm, v(68.35, -89.31) * mm]});
            skFitSpline(sketch, "E311", {"points": [v(68.35, -89.31) * mm, v(67.23, -89.59) * mm, v(66.87, -89.26) * mm, v(66.7, -87.85) * mm]});
            skFitSpline(sketch, "E312", {"points": [v(66.7, -87.85) * mm, v(66.52, -86.45) * mm, v(66.01, -85.98) * mm, v(64.5, -85.82) * mm]});
            skFitSpline(sketch, "E313", {"points": [v(64.5, -85.82) * mm, v(61.9, -85.54) * mm, v(59.84, -88.26) * mm, v(60.57, -91) * mm]});
            skFitSpline(sketch, "E314", {"points": [v(60.57, -91) * mm, v(61.4, -94.13) * mm, v(63.06, -95.3) * mm, v(66.59, -95.3) * mm]});
            skFitSpline(sketch, "E315", {"points": [v(47.74, -84.06) * mm, v(47.74, -83.55) * mm, v(48.4, -82.34) * mm, v(49.21, -81.38) * mm]});
            skFitSpline(sketch, "E316", {"points": [v(49.21, -81.38) * mm, v(50.02, -80.42) * mm, v(50.68, -79.33) * mm, v(50.68, -78.96) * mm]});
            skFitSpline(sketch, "E317", {"points": [v(50.68, -78.96) * mm, v(50.68, -78.6) * mm, v(48.86, -78.16) * mm, v(46.64, -77.98) * mm]});
            skFitSpline(sketch, "E318", {"points": [v(46.64, -77.98) * mm, v(42.07, -77.63) * mm, v(39.72, -76.06) * mm, v(37.39, -71.8) * mm]});
            skFitSpline(sketch, "E319", {"points": [v(37.39, -71.8) * mm, v(35.26, -67.92) * mm, v(35.58, -65.98) * mm, v(38.84, -62.93) * mm]});
            skFitSpline(sketch, "E320", {"points": [v(38.84, -62.93) * mm, v(40.41, -61.46) * mm, v(42.31, -60.26) * mm, v(43.07, -60.26) * mm]});
            skFitSpline(sketch, "E321", {"points": [v(43.07, -60.26) * mm, v(45.34, -60.27) * mm, v(49.14, -62.85) * mm, v(49.65, -64.73) * mm]});
            skFitSpline(sketch, "E322", {"points": [v(49.65, -64.73) * mm, v(50.18, -66.72) * mm, v(48.32, -69.2) * mm, v(46.34, -69.17) * mm]});
            skFitSpline(sketch, "E323", {"points": [v(46.34, -69.17) * mm, v(45.33, -69.15) * mm, v(45.34, -69.03) * mm, v(46.46, -68.24) * mm]});
            skFitSpline(sketch, "E324", {"points": [v(46.46, -68.24) * mm, v(48.47, -66.81) * mm, v(48.13, -63.81) * mm, v(45.9, -63.3) * mm]});
            skFitSpline(sketch, "E325", {"points": [v(45.9, -63.3) * mm, v(42.18, -62.42) * mm, v(38.89, -66.2) * mm, v(39.94, -70.14) * mm]});
            skFitSpline(sketch, "E326", {"points": [v(39.94, -70.14) * mm, v(40.81, -73.38) * mm, v(42.95, -75.02) * mm, v(46.19, -74.94) * mm]});
            skFitSpline(sketch, "E327", {"points": [v(46.19, -74.94) * mm, v(54.47, -74.74) * mm, v(58.63, -65.76) * mm, v(53.4, -59.36) * mm]});
            skFitSpline(sketch, "E328", {"points": [v(53.4, -59.36) * mm, v(49.97, -55.15) * mm, v(42.98, -53.46) * mm, v(38.34, -55.73) * mm]});
            skFitSpline(sketch, "E329", {"points": [v(38.34, -55.73) * mm, v(33.73, -57.99) * mm, v(30.11, -63.32) * mm, v(30.11, -67.88) * mm]});
            skFitSpline(sketch, "E330", {"points": [v(30.11, -67.88) * mm, v(30.11, -73.55) * mm, v(34.43, -79.06) * mm, v(41.87, -82.9) * mm]});
            skFitSpline(sketch, "E331", {"points": [v(41.87, -82.9) * mm, v(46.33, -85.2) * mm, v(47.74, -85.47) * mm, v(47.74, -84.06) * mm]});
            skFitSpline(sketch, "E332", {"points": [v(2.53, -81.63) * mm, v(3.14, -80.54) * mm, v(4.96, -78.57) * mm, v(6.6, -77.27) * mm]});
            skFitSpline(sketch, "E333", {"points": [v(6.6, -77.27) * mm, v(8.22, -75.97) * mm, v(9.55, -74.59) * mm, v(9.55, -74.2) * mm]});
            skFitSpline(sketch, "E334", {"points": [v(9.55, -74.2) * mm, v(9.55, -73.81) * mm, v(8.27, -73.3) * mm, v(6.7, -73.07) * mm]});
            skFitSpline(sketch, "E335", {"points": [v(6.7, -73.07) * mm, v(5.14, -72.83) * mm, v(2.17, -71.56) * mm, v(0.1, -70.23) * mm]});
            skFitSpline(sketch, "E336", {"points": [v(0.1, -70.23) * mm, v(-1.95, -68.9) * mm, v(-3.99, -67.82) * mm, v(-4.41, -67.82) * mm]});
            skFitSpline(sketch, "E337", {"points": [v(-4.41, -67.82) * mm, v(-4.84, -67.82) * mm, v(-6.19, -68.89) * mm, v(-7.41, -70.2) * mm]});
            skFitSpline(sketch, "E338", {"points": [v(-7.41, -70.2) * mm, v(-8.64, -71.5) * mm, v(-10.28, -72.75) * mm, v(-11.06, -72.99) * mm]});
            skFitSpline(sketch, "E339", {"points": [v(-11.06, -72.99) * mm, v(-13.55, -73.73) * mm, v(-12.58, -74.98) * mm, v(-7.89, -77.1) * mm]});
            skFitSpline(sketch, "E340", {"points": [v(-7.89, -77.1) * mm, v(-4.96, -78.42) * mm, v(-2.8, -79.95) * mm, v(-1.85, -81.37) * mm]});
            skFitSpline(sketch, "E341", {"points": [v(-1.85, -81.37) * mm, v(0, -84.12) * mm, v(1.12, -84.19) * mm, v(2.53, -81.63) * mm]});
            skFitSpline(sketch, "E342", {"points": [v(-66.98, -80.27) * mm, v(-64.81, -76.67) * mm, v(-64.81, -71.34) * mm, v(-66.98, -67.74) * mm]});
            skFitSpline(sketch, "E343", {"points": [v(-66.98, -67.74) * mm, v(-69.86, -62.94) * mm, v(-70.51, -64.1) * mm, v(-70.51, -74) * mm]});
            skFitSpline(sketch, "E344", {"points": [v(-70.51, -74) * mm, v(-70.51, -83.92) * mm, v(-69.86, -85.07) * mm, v(-66.98, -80.27) * mm]});
            skFitSpline(sketch, "E345", {"points": [v(-23.5, -77.49) * mm, v(-23.5, -77.13) * mm, v(-22.84, -76.65) * mm, v(-22.04, -76.4) * mm]});
            skFitSpline(sketch, "E346", {"points": [v(-22.04, -76.4) * mm, v(-20.12, -75.84) * mm, v(-20.14, -73.54) * mm, v(-22.06, -72.97) * mm]});
            skFitSpline(sketch, "E347", {"points": [v(-22.06, -72.97) * mm, v(-24.03, -72.38) * mm, v(-26.95, -68.13) * mm, v(-27.56, -64.97) * mm]});
            skFitSpline(sketch, "E348", {"points": [v(-27.56, -64.97) * mm, v(-28.48, -60.2) * mm, v(-24.26, -55.45) * mm, v(-19.11, -55.45) * mm]});
            skFitSpline(sketch, "E349", {"points": [v(-19.11, -55.45) * mm, v(-16.9, -55.45) * mm, v(-13.22, -59.06) * mm, v(-13.22, -61.24) * mm]});
            skFitSpline(sketch, "E350", {"points": [v(-13.22, -61.24) * mm, v(-13.22, -62.96) * mm, v(-15.46, -65.76) * mm, v(-16.85, -65.76) * mm]});
            skFitSpline(sketch, "E351", {"points": [v(-16.85, -65.76) * mm, v(-18.33, -65.76) * mm, v(-18.43, -64.27) * mm, v(-16.97, -63.91) * mm]});
            skFitSpline(sketch, "E352", {"points": [v(-16.97, -63.91) * mm, v(-14.84, -63.4) * mm, v(-14.83, -59.92) * mm, v(-16.96, -58.85) * mm]});
            skFitSpline(sketch, "E353", {"points": [v(-16.96, -58.85) * mm, v(-18.83, -57.92) * mm, v(-22.45, -59.1) * mm, v(-23.53, -61) * mm]});
            skFitSpline(sketch, "E354", {"points": [v(-23.53, -61) * mm, v(-24.57, -62.82) * mm, v(-24.4, -66.24) * mm, v(-23.14, -68.51) * mm]});
            skFitSpline(sketch, "E355", {"points": [v(-23.14, -68.51) * mm, v(-20.77, -72.8) * mm, v(-11.38, -71.45) * mm, v(-8.59, -66.43) * mm]});
            skFitSpline(sketch, "E356", {"points": [v(-8.59, -66.43) * mm, v(-5.74, -61.31) * mm, v(-8.47, -53.64) * mm, v(-14.11, -50.9) * mm]});
            skFitSpline(sketch, "E357", {"points": [v(-14.11, -50.9) * mm, v(-17.68, -49.18) * mm, v(-23.95, -49.87) * mm, v(-27.72, -52.4) * mm]});
            skFitSpline(sketch, "E358", {"points": [v(-27.72, -52.4) * mm, v(-32.06, -55.3) * mm, v(-33.06, -57.25) * mm, v(-33.04, -62.77) * mm]});
            skFitSpline(sketch, "E359", {"points": [v(-33.04, -62.77) * mm, v(-33.02, -67.82) * mm, v(-31.57, -71.75) * mm, v(-28.2, -75.88) * mm]});
            skFitSpline(sketch, "E360", {"points": [v(-28.2, -75.88) * mm, v(-26.51, -77.95) * mm, v(-23.5, -78.98) * mm, v(-23.5, -77.49) * mm]});
            skFitSpline(sketch, "E361", {"points": [v(27.91, -75.08) * mm, v(27.91, -74.53) * mm, v(27.6, -73.9) * mm, v(27.22, -73.69) * mm]});
            skFitSpline(sketch, "E362", {"points": [v(27.22, -73.69) * mm, v(26.84, -73.47) * mm, v(26.3, -71.9) * mm, v(26.03, -70.2) * mm]});
            skFitSpline(sketch, "E363", {"points": [v(26.03, -70.2) * mm, v(25.46, -66.61) * mm, v(24.54, -66.39) * mm, v(21.72, -69.14) * mm]});
            skFitSpline(sketch, "E364", {"points": [v(21.72, -69.14) * mm, v(19.29, -71.52) * mm, v(19.4, -72.01) * mm, v(22.77, -74.25) * mm]});
            skFitSpline(sketch, "E365", {"points": [v(22.77, -74.25) * mm, v(25.69, -76.18) * mm, v(27.91, -76.54) * mm, v(27.91, -75.08) * mm]});
            skFitSpline(sketch, "E366", {"points": [v(69.78, -73.06) * mm, v(69.78, -71.06) * mm, v(69.5, -70.69) * mm, v(67.68, -70.35) * mm]});
            skFitSpline(sketch, "E367", {"points": [v(67.68, -70.35) * mm, v(66.52, -70.13) * mm, v(64.57, -69.16) * mm, v(63.35, -68.2) * mm]});
            skFitSpline(sketch, "E368", {"points": [v(63.35, -68.2) * mm, v(60.9, -66.28) * mm, v(59.5, -65.96) * mm, v(59.5, -67.33) * mm]});
            skFitSpline(sketch, "E369", {"points": [v(59.5, -67.33) * mm, v(59.5, -67.82) * mm, v(58.83, -69.43) * mm, v(58.03, -70.91) * mm]});
            skFitSpline(sketch, "E370", {"points": [v(58.03, -70.91) * mm, v(56.03, -74.58) * mm, v(56.14, -74.87) * mm, v(59.31, -74.42) * mm]});
            skFitSpline(sketch, "E371", {"points": [v(59.31, -74.42) * mm, v(60.83, -74.2) * mm, v(63.22, -74.3) * mm, v(64.64, -74.63) * mm]});
            skFitSpline(sketch, "E372", {"points": [v(64.64, -74.63) * mm, v(69.33, -75.74) * mm, v(69.78, -75.6) * mm, v(69.78, -73.06) * mm]});
            skFitSpline(sketch, "E373", {"points": [v(-37, -68.34) * mm, v(-37.24, -67.48) * mm, v(-37.44, -65.32) * mm, v(-37.45, -63.52) * mm]});
            skFitSpline(sketch, "E374", {"points": [v(-37.45, -63.52) * mm, v(-37.46, -61.37) * mm, v(-37.77, -60.27) * mm, v(-38.38, -60.28) * mm]});
            skFitSpline(sketch, "E375", {"points": [v(-38.38, -60.28) * mm, v(-39.44, -60.3) * mm, v(-44.8, -64.8) * mm, v(-44.8, -65.67) * mm]});
            skFitSpline(sketch, "E376", {"points": [v(-44.8, -65.67) * mm, v(-44.8, -66.57) * mm, v(-39.48, -69.8) * mm, v(-37.92, -69.84) * mm]});
            skFitSpline(sketch, "E377", {"points": [v(-37.92, -69.84) * mm, v(-36.86, -69.87) * mm, v(-36.65, -69.54) * mm, v(-37, -68.34) * mm]});
            skFitSpline(sketch, "E378", {"points": [v(15.2, -67.68) * mm, v(21.47, -65.16) * mm, v(23.5, -62.04) * mm, v(23.5, -54.92) * mm]});
            skFitSpline(sketch, "E379", {"points": [v(23.5, -54.92) * mm, v(23.5, -50.06) * mm, v(21.04, -42.4) * mm, v(19.48, -42.4) * mm]});
            skFitSpline(sketch, "E380", {"points": [v(19.48, -42.4) * mm, v(17.79, -42.4) * mm, v(13.96, -43.9) * mm, v(13.96, -44.57) * mm]});
            skFitSpline(sketch, "E381", {"points": [v(13.96, -44.57) * mm, v(13.96, -44.93) * mm, v(14.75, -46.22) * mm, v(15.73, -47.42) * mm]});
            skFitSpline(sketch, "E382", {"points": [v(15.73, -47.42) * mm, v(18.28, -50.56) * mm, v(18.81, -54.15) * mm, v(17.29, -57.89) * mm]});
            skFitSpline(sketch, "E383", {"points": [v(17.29, -57.89) * mm, v(15.8, -61.5) * mm, v(13.8, -63) * mm, v(10.44, -63) * mm]});
            skFitSpline(sketch, "E384", {"points": [v(10.44, -63) * mm, v(7.21, -63) * mm, v(5.4, -62.04) * mm, v(4.05, -59.59) * mm]});
            skFitSpline(sketch, "E385", {"points": [v(4.05, -59.59) * mm, v(2.51, -56.8) * mm, v(2.65, -55.66) * mm, v(4.77, -53.67) * mm]});
            skFitSpline(sketch, "E386", {"points": [v(4.77, -53.67) * mm, v(6.37, -52.17) * mm, v(6.8, -52.07) * mm, v(8.26, -52.82) * mm]});
            skFitSpline(sketch, "E387", {"points": [v(8.26, -52.82) * mm, v(9.9, -53.67) * mm, v(9.9, -53.68) * mm, v(7.71, -54.05) * mm]});
            skFitSpline(sketch, "E388", {"points": [v(7.71, -54.05) * mm, v(5.27, -54.47) * mm, v(4.34, -56.81) * mm, v(5.9, -58.58) * mm]});
            skFitSpline(sketch, "E389", {"points": [v(5.9, -58.58) * mm, v(7.15, -59.98) * mm, v(12, -59.85) * mm, v(13.42, -58.37) * mm]});
            skFitSpline(sketch, "E390", {"points": [v(13.42, -58.37) * mm, v(16.44, -55.23) * mm, v(15.48, -49.34) * mm, v(11.71, -47.88) * mm]});
            skFitSpline(sketch, "E391", {"points": [v(11.71, -47.88) * mm, v(8.46, -46.62) * mm, v(2.54, -47.36) * mm, v(0.34, -49.3) * mm]});
            skFitSpline(sketch, "E392", {"points": [v(0.34, -49.3) * mm, v(-4.7, -53.71) * mm, v(-3.16, -63.56) * mm, v(3.11, -67.14) * mm]});
            skFitSpline(sketch, "E393", {"points": [v(3.11, -67.14) * mm, v(5.87, -68.7) * mm, v(11.97, -68.98) * mm, v(15.2, -67.68) * mm]});
            skFitSpline(sketch, "E394", {"points": [v(69.78, -63.28) * mm, v(69.78, -61.64) * mm, v(69.16, -60.11) * mm, v(67.94, -58.76) * mm]});
            skFitSpline(sketch, "E395", {"points": [v(67.94, -58.76) * mm, v(66.9, -57.61) * mm, v(66.1, -55.85) * mm, v(66.1, -54.73) * mm]});
            skFitSpline(sketch, "E396", {"points": [v(66.1, -54.73) * mm, v(66.1, -53.36) * mm, v(66.68, -52.38) * mm, v(67.94, -51.6) * mm]});
            skFitSpline(sketch, "E397", {"points": [v(67.94, -51.6) * mm, v(70.38, -50.11) * mm, v(70.63, -45.83) * mm, v(68.27, -45.83) * mm]});
            skFitSpline(sketch, "E398", {"points": [v(68.27, -45.83) * mm, v(65.82, -45.83) * mm, v(62.54, -47.77) * mm, v(61.34, -49.93) * mm]});
            skFitSpline(sketch, "E399", {"points": [v(61.34, -49.93) * mm, v(59.92, -52.5) * mm, v(59.91, -57.7) * mm, v(61.32, -60.23) * mm]});
            skFitSpline(sketch, "E400", {"points": [v(61.32, -60.23) * mm, v(62.62, -62.6) * mm, v(66.7, -65.74) * mm, v(68.5, -65.75) * mm]});
            skFitSpline(sketch, "E401", {"points": [v(68.5, -65.75) * mm, v(69.48, -65.76) * mm, v(69.78, -65.19) * mm, v(69.78, -63.28) * mm]});
            skFitSpline(sketch, "E402", {"points": [v(-47.02, -61.3) * mm, v(-43.78, -59.73) * mm, v(-42.6, -57.66) * mm, v(-42.6, -53.55) * mm]});
            skFitSpline(sketch, "E403", {"points": [v(-42.6, -53.55) * mm, v(-42.6, -46.85) * mm, v(-46.3, -43.45) * mm, v(-51.75, -45.13) * mm]});
            skFitSpline(sketch, "E404", {"points": [v(-51.75, -45.13) * mm, v(-54.76, -46.06) * mm, v(-55.82, -47.54) * mm, v(-55.82, -50.8) * mm]});
            skFitSpline(sketch, "E405", {"points": [v(-55.82, -50.8) * mm, v(-55.82, -53.6) * mm, v(-54.72, -54.76) * mm, v(-52.05, -54.76) * mm]});
            skFitSpline(sketch, "E406", {"points": [v(-52.05, -54.76) * mm, v(-49.94, -54.76) * mm, v(-48.64, -52.83) * mm, v(-49.64, -51.16) * mm]});
            skFitSpline(sketch, "E407", {"points": [v(-49.64, -51.16) * mm, v(-49.92, -50.69) * mm, v(-49.58, -50.8) * mm, v(-48.87, -51.42) * mm]});
            skFitSpline(sketch, "E408", {"points": [v(-48.87, -51.42) * mm, v(-47.16, -52.93) * mm, v(-47.98, -55.17) * mm, v(-50.73, -56.5) * mm]});
            skFitSpline(sketch, "E409", {"points": [v(-50.73, -56.5) * mm, v(-52.66, -57.44) * mm, v(-53.11, -57.44) * mm, v(-55.08, -56.49) * mm]});
            skFitSpline(sketch, "E410", {"points": [v(-55.08, -56.49) * mm, v(-59.32, -54.43) * mm, v(-60.78, -48.91) * mm, v(-57.96, -45.56) * mm]});
            skFitSpline(sketch, "E411", {"points": [v(-57.96, -45.56) * mm, v(-56.26, -43.54) * mm, v(-52.21, -41.7) * mm, v(-49.46, -41.7) * mm]});
            skFitSpline(sketch, "E412", {"points": [v(-49.46, -41.7) * mm, v(-44.7, -41.7) * mm, v(-38.83, -46.8) * mm, v(-37.75, -51.85) * mm]});
            skFitSpline(sketch, "E413", {"points": [v(-37.75, -51.85) * mm, v(-37.18, -54.54) * mm, v(-35.87, -54.71) * mm, v(-34.48, -52.3) * mm]});
            skFitSpline(sketch, "E414", {"points": [v(-34.48, -52.3) * mm, v(-33.92, -51.3) * mm, v(-32.54, -49.78) * mm, v(-31.42, -48.9) * mm]});
            skFitSpline(sketch, "E415", {"points": [v(-31.42, -48.9) * mm, v(-30.3, -48.02) * mm, v(-29.38, -47.03) * mm, v(-29.38, -46.72) * mm]});
            skFitSpline(sketch, "E416", {"points": [v(-29.38, -46.72) * mm, v(-29.38, -46.4) * mm, v(-30.56, -45.55) * mm, v(-32.01, -44.82) * mm]});
            skFitSpline(sketch, "E417", {"points": [v(-32.01, -44.82) * mm, v(-33.46, -44.09) * mm, v(-35.63, -42.2) * mm, v(-36.84, -40.62) * mm]});
            skFitSpline(sketch, "E418", {"points": [v(-36.84, -40.62) * mm, v(-38.72, -38.18) * mm, v(-39.54, -37.7) * mm, v(-42.4, -37.33) * mm]});
            skFitSpline(sketch, "E419", {"points": [v(-42.4, -37.33) * mm, v(-51.66, -36.14) * mm, v(-58.6, -37.46) * mm, v(-62.2, -41.1) * mm]});
            skFitSpline(sketch, "E420", {"points": [v(-62.2, -41.1) * mm, v(-65.63, -44.58) * mm, v(-65.83, -53.98) * mm, v(-62.56, -58.2) * mm]});
            skFitSpline(sketch, "E421", {"points": [v(-62.56, -58.2) * mm, v(-59.62, -62) * mm, v(-51.71, -63.57) * mm, v(-47.02, -61.3) * mm]});
            skFitSpline(sketch, "E422", {"points": [v(-68.3, -56.82) * mm, v(-68.3, -56.06) * mm, v(-68.8, -55.45) * mm, v(-69.41, -55.45) * mm]});
            skFitSpline(sketch, "E423", {"points": [v(-69.41, -55.45) * mm, v(-70.02, -55.45) * mm, v(-70.51, -56.06) * mm, v(-70.51, -56.82) * mm]});
            skFitSpline(sketch, "E424", {"points": [v(-70.51, -56.82) * mm, v(-70.51, -57.59) * mm, v(-70.02, -58.2) * mm, v(-69.41, -58.2) * mm]});
            skFitSpline(sketch, "E425", {"points": [v(-69.41, -58.2) * mm, v(-68.8, -58.2) * mm, v(-68.3, -57.59) * mm, v(-68.3, -56.82) * mm]});
            skFitSpline(sketch, "E426", {"points": [v(56.56, -54.08) * mm, v(56.56, -52.33) * mm, v(56.27, -52.01) * mm, v(54.72, -52.01) * mm]});
            skFitSpline(sketch, "E427", {"points": [v(54.72, -52.01) * mm, v(52.71, -52.01) * mm, v(52.18, -53.83) * mm, v(53.77, -55.31) * mm]});
            skFitSpline(sketch, "E428", {"points": [v(53.77, -55.31) * mm, v(55.33, -56.78) * mm, v(56.56, -56.24) * mm, v(56.56, -54.08) * mm]});
            skFitSpline(sketch, "E429", {"points": [v(33.1, -53.56) * mm, v(34.67, -52.52) * mm, v(35.95, -51.36) * mm, v(35.93, -50.98) * mm]});
            skFitSpline(sketch, "E430", {"points": [v(35.93, -50.98) * mm, v(35.91, -50.6) * mm, v(34.54, -49.37) * mm, v(32.88, -48.23) * mm]});
            skFitSpline(sketch, "E431", {"points": [v(32.88, -48.23) * mm, v(31.07, -47) * mm, v(28.95, -44.59) * mm, v(27.6, -42.22) * mm]});
            skFitSpline(sketch, "E432", {"points": [v(27.6, -42.22) * mm, v(25.34, -38.26) * mm, v(23.99, -37.58) * mm, v(22.56, -39.7) * mm]});
            skFitSpline(sketch, "E433", {"points": [v(22.56, -39.7) * mm, v(22.01, -40.52) * mm, v(22.57, -41.92) * mm, v(24.82, -45.4) * mm]});
            skFitSpline(sketch, "E434", {"points": [v(24.82, -45.4) * mm, v(26.45, -47.95) * mm, v(28.02, -51.25) * mm, v(28.29, -52.74) * mm]});
            skFitSpline(sketch, "E435", {"points": [v(28.29, -52.74) * mm, v(28.55, -54.23) * mm, v(29.1, -55.45) * mm, v(29.51, -55.45) * mm]});
            skFitSpline(sketch, "E436", {"points": [v(29.51, -55.45) * mm, v(29.92, -55.45) * mm, v(31.53, -54.6) * mm, v(33.1, -53.56) * mm]});
            skFitSpline(sketch, "E437", {"points": [v(-4.4, -50.35) * mm, v(-4.4, -48.96) * mm, v(0.3, -44.46) * mm, v(1.74, -44.46) * mm]});
            skFitSpline(sketch, "E438", {"points": [v(1.74, -44.46) * mm, v(2.4, -44.46) * mm, v(2.94, -44.13) * mm, v(2.94, -43.74) * mm]});
            skFitSpline(sketch, "E439", {"points": [v(2.94, -43.74) * mm, v(2.94, -43.1) * mm, v(-3.95, -36.2) * mm, v(-4.58, -36.2) * mm]});
            skFitSpline(sketch, "E440", {"points": [v(-4.58, -36.2) * mm, v(-5.1, -36.2) * mm, v(-14.7, -45.24) * mm, v(-14.7, -45.73) * mm]});
            skFitSpline(sketch, "E441", {"points": [v(-14.7, -45.73) * mm, v(-14.7, -46) * mm, v(-13.52, -46.63) * mm, v(-12.1, -47.12) * mm]});
            skFitSpline(sketch, "E442", {"points": [v(-12.1, -47.12) * mm, v(-10.68, -47.6) * mm, v(-8.99, -48.74) * mm, v(-8.34, -49.66) * mm]});
            skFitSpline(sketch, "E443", {"points": [v(-8.34, -49.66) * mm, v(-7.08, -51.47) * mm, v(-4.4, -51.93) * mm, v(-4.4, -50.35) * mm]});
            skFitSpline(sketch, "E444", {"points": [v(61.12, -45.49) * mm, v(63.14, -43.78) * mm, v(65.1, -42.4) * mm, v(65.45, -42.4) * mm]});
            skFitSpline(sketch, "E445", {"points": [v(65.45, -42.4) * mm, v(65.81, -42.4) * mm, v(66.1, -41.93) * mm, v(66.1, -41.36) * mm]});
            skFitSpline(sketch, "E446", {"points": [v(66.1, -41.36) * mm, v(66.1, -40.8) * mm, v(65.64, -40.33) * mm, v(65.08, -40.33) * mm]});
            skFitSpline(sketch, "E447", {"points": [v(65.08, -40.33) * mm, v(64.52, -40.33) * mm, v(63, -39.4) * mm, v(61.7, -38.27) * mm]});
            skFitSpline(sketch, "E448", {"points": [v(61.7, -38.27) * mm, v(58.75, -35.7) * mm, v(58.02, -35.72) * mm, v(56.19, -38.44) * mm]});
            skFitSpline(sketch, "E449", {"points": [v(56.19, -38.44) * mm, v(55.38, -39.64) * mm, v(53.56, -41.36) * mm, v(52.15, -42.26) * mm]});
            skFitSpline(sketch, "E450", {"points": [v(52.15, -42.26) * mm, v(47.26, -45.36) * mm, v(39.32, -43.03) * mm, v(36.99, -37.8) * mm]});
            skFitSpline(sketch, "E451", {"points": [v(36.99, -37.8) * mm, v(36.05, -35.7) * mm, v(36.09, -35.17) * mm, v(37.37, -32.46) * mm]});
            skFitSpline(sketch, "E452", {"points": [v(37.37, -32.46) * mm, v(39.6, -27.75) * mm, v(43.82, -26.5) * mm, v(46.97, -29.64) * mm]});
            skFitSpline(sketch, "E453", {"points": [v(46.97, -29.64) * mm, v(48.21, -30.88) * mm, v(48.53, -31.78) * mm, v(48.19, -33.08) * mm]});
            skFitSpline(sketch, "E454", {"points": [v(48.19, -33.08) * mm, v(47.93, -34.04) * mm, v(47.42, -34.83) * mm, v(47.06, -34.83) * mm]});
            skFitSpline(sketch, "E455", {"points": [v(47.06, -34.83) * mm, v(46.7, -34.83) * mm, v(46.58, -34.21) * mm, v(46.8, -33.46) * mm]});
            skFitSpline(sketch, "E456", {"points": [v(46.8, -33.46) * mm, v(47.6, -30.58) * mm, v(43.89, -28.92) * mm, v(41.55, -31.1) * mm]});
            skFitSpline(sketch, "E457", {"points": [v(41.55, -31.1) * mm, v(40, -32.56) * mm, v(40.08, -37.06) * mm, v(41.68, -38.9) * mm]});
            skFitSpline(sketch, "E458", {"points": [v(41.68, -38.9) * mm, v(43.47, -40.95) * mm, v(47.91, -41.52) * mm, v(50.36, -40.02) * mm]});
            skFitSpline(sketch, "E459", {"points": [v(50.36, -40.02) * mm, v(52.54, -38.69) * mm, v(54.35, -35.13) * mm, v(54.35, -32.2) * mm]});
            skFitSpline(sketch, "E460", {"points": [v(54.35, -32.2) * mm, v(54.35, -24.56) * mm, v(45.4, -20.04) * mm, v(37.61, -23.77) * mm]});
            skFitSpline(sketch, "E461", {"points": [v(37.61, -23.77) * mm, v(32.66, -26.13) * mm, v(30.85, -29.47) * mm, v(30.85, -36.2) * mm]});
            skFitSpline(sketch, "E462", {"points": [v(30.85, -36.2) * mm, v(30.85, -41.16) * mm, v(32.8, -44.08) * mm, v(37.85, -46.67) * mm]});
            skFitSpline(sketch, "E463", {"points": [v(37.85, -46.67) * mm, v(41.18, -48.38) * mm, v(42.2, -48.55) * mm, v(49.47, -48.56) * mm]});
            skFitSpline(sketch, "E464", {"points": [v(-66.72, -40.7) * mm, v(-65.61, -39) * mm, v(-63.47, -37) * mm, v(-61.77, -36.1) * mm]});
            skFitSpline(sketch, "E465", {"points": [v(-61.77, -36.1) * mm, v(-60.12, -35.21) * mm, v(-58.77, -34.13) * mm, v(-58.77, -33.7) * mm]});
            skFitSpline(sketch, "E466", {"points": [v(-58.77, -33.7) * mm, v(-58.76, -33.26) * mm, v(-60.25, -32.09) * mm, v(-62.07, -31.09) * mm]});
            skFitSpline(sketch, "E467", {"points": [v(-62.07, -31.09) * mm, v(-63.89, -30.1) * mm, v(-66.1, -28.36) * mm, v(-66.98, -27.25) * mm]});
            skFitSpline(sketch, "E468", {"points": [v(-66.98, -27.25) * mm, v(-69.68, -23.83) * mm, v(-70.82, -24.53) * mm, v(-70.12, -29.16) * mm]});
            skFitSpline(sketch, "E469", {"points": [v(-70.12, -29.16) * mm, v(-69.42, -33.81) * mm, v(-69.43, -36.07) * mm, v(-70.16, -40.5) * mm]});
            skFitSpline(sketch, "E470", {"points": [v(-70.16, -40.5) * mm, v(-70.87, -44.78) * mm, v(-69.42, -44.87) * mm, v(-66.72, -40.7) * mm]});
            skFitSpline(sketch, "E471", {"points": [v(-15.96, -40.77) * mm, v(-13.61, -39.8) * mm, v(-10.97, -37.97) * mm, v(-9.35, -36.2) * mm]});
            skFitSpline(sketch, "E472", {"points": [v(-9.35, -36.2) * mm, v(-6.7, -33.3) * mm, v(-6.65, -33.14) * mm, v(-6.81, -28.03) * mm]});
            skFitSpline(sketch, "E473", {"points": [v(-6.81, -28.03) * mm, v(-6.9, -25.16) * mm, v(-6.7, -21.26) * mm, v(-6.36, -19.37) * mm]});
            skFitSpline(sketch, "E474", {"points": [v(-10.95, -15.85) * mm, v(-16.6, -15.77) * mm, v(-17.4, -16.4) * mm, v(-14.59, -18.75) * mm]});
            skFitSpline(sketch, "E475", {"points": [v(-14.59, -18.75) * mm, v(-12.76, -20.27) * mm, v(-11.02, -23.82) * mm, v(-11.02, -26) * mm]});
            skFitSpline(sketch, "E476", {"points": [v(-11.02, -26) * mm, v(-11.02, -29.02) * mm, v(-13.98, -33.42) * mm, v(-17.21, -35.19) * mm]});
            skFitSpline(sketch, "E477", {"points": [v(-17.21, -35.19) * mm, v(-22.37, -38.02) * mm, v(-26.6, -37.15) * mm, v(-29.02, -32.76) * mm]});
            skFitSpline(sketch, "E478", {"points": [v(-29.02, -32.76) * mm, v(-30.7, -29.73) * mm, v(-30.38, -27.41) * mm, v(-27.97, -25.16) * mm]});
            skFitSpline(sketch, "E479", {"points": [v(-27.97, -25.16) * mm, v(-25.33, -22.7) * mm, v(-23.19, -22.6) * mm, v(-21.59, -24.9) * mm]});
            skFitSpline(sketch, "E480", {"points": [v(-21.59, -24.9) * mm, v(-20.18, -26.9) * mm, v(-20.82, -28.15) * mm, v(-22.3, -26.26) * mm]});
            skFitSpline(sketch, "E481", {"points": [v(-22.3, -26.26) * mm, v(-23.02, -25.34) * mm, v(-23.8, -25.13) * mm, v(-25.23, -25.47) * mm]});
            skFitSpline(sketch, "E482", {"points": [v(-25.23, -25.47) * mm, v(-26.87, -25.85) * mm, v(-27.18, -26.3) * mm, v(-27.18, -28.32) * mm]});
            skFitSpline(sketch, "E483", {"points": [v(-27.18, -28.32) * mm, v(-27.18, -31.33) * mm, v(-25.02, -33.46) * mm, v(-21.99, -33.46) * mm]});
            skFitSpline(sketch, "E484", {"points": [v(-21.99, -33.46) * mm, v(-17.4, -33.46) * mm, v(-14.75, -31.08) * mm, v(-14.71, -26.92) * mm]});
            skFitSpline(sketch, "E485", {"points": [v(-14.71, -26.92) * mm, v(-14.69, -23.65) * mm, v(-17.5, -19.3) * mm, v(-20.3, -18.3) * mm]});
            skFitSpline(sketch, "E486", {"points": [v(-20.3, -18.3) * mm, v(-27.9, -15.6) * mm, v(-36, -21.17) * mm, v(-36, -29.12) * mm]});
            skFitSpline(sketch, "E487", {"points": [v(-36, -29.12) * mm, v(-36, -34.48) * mm, v(-33.15, -39.07) * mm, v(-28.28, -41.6) * mm]});
            skFitSpline(sketch, "E488", {"points": [v(-28.28, -41.6) * mm, v(-25.78, -42.88) * mm, v(-20.16, -42.51) * mm, v(-15.96, -40.77) * mm]});
            skFitSpline(sketch, "E489", {"points": [v(18.15, -37.6) * mm, v(21.23, -35.85) * mm, v(23.5, -31.6) * mm, v(23.5, -27.61) * mm]});
            skFitSpline(sketch, "E490", {"points": [v(23.5, -27.61) * mm, v(23.5, -20.22) * mm, v(18.1, -16.37) * mm, v(10.45, -18.3) * mm]});
            skFitSpline(sketch, "E491", {"points": [v(10.45, -18.3) * mm, v(7.14, -19.13) * mm, v(5.14, -21.56) * mm, v(5.14, -24.74) * mm]});
            skFitSpline(sketch, "E492", {"points": [v(5.14, -24.74) * mm, v(5.14, -28.48) * mm, v(10.5, -31.76) * mm, v(13.86, -30.07) * mm]});
            skFitSpline(sketch, "E493", {"points": [v(13.86, -30.07) * mm, v(17.15, -28.43) * mm, v(16.21, -24.1) * mm, v(12.7, -24.72) * mm]});
            skFitSpline(sketch, "E494", {"points": [v(12.7, -24.72) * mm, v(11.34, -24.97) * mm, v(11.17, -24.84) * mm, v(11.84, -24.09) * mm]});
            skFitSpline(sketch, "E495", {"points": [v(11.84, -24.09) * mm, v(13.9, -21.77) * mm, v(17.63, -24.13) * mm, v(17.63, -27.76) * mm]});
            skFitSpline(sketch, "E496", {"points": [v(17.63, -27.76) * mm, v(17.63, -32.2) * mm, v(11.8, -35.27) * mm, v(7.42, -33.15) * mm]});
            skFitSpline(sketch, "E497", {"points": [v(7.42, -33.15) * mm, v(4, -31.5) * mm, v(1.83, -26.73) * mm, v(2.65, -22.65) * mm]});
            skFitSpline(sketch, "E498", {"points": [v(2.65, -22.65) * mm, v(3.2, -19.95) * mm, v(8.27, -14.37) * mm, v(10.71, -13.8) * mm]});
            skFitSpline(sketch, "E499", {"points": [v(10.71, -13.8) * mm, v(13.12, -13.23) * mm, v(12.93, -12.06) * mm, v(10.22, -10.61) * mm]});
            skFitSpline(sketch, "E500", {"points": [v(10.22, -10.61) * mm, v(7.16, -8.98) * mm, v(6.29, -9.08) * mm, v(2.57, -11.47) * mm]});
            skFitSpline(sketch, "E501", {"points": [v(2.57, -11.47) * mm, v(-0.85, -13.67) * mm, v(-0.9, -13.77) * mm, v(-2.23, -20.02) * mm]});
            skFitSpline(sketch, "E502", {"points": [v(-2.23, -20.02) * mm, v(-3.78, -27.29) * mm, v(-1.45, -34.98) * mm, v(3.07, -37.56) * mm]});
            skFitSpline(sketch, "E503", {"points": [v(3.07, -37.56) * mm, v(6.46, -39.5) * mm, v(14.8, -39.52) * mm, v(18.15, -37.6) * mm]});
            skFitSpline(sketch, "E504", {"points": [v(69.78, -34.22) * mm, v(69.78, -32.07) * mm, v(69.27, -31.06) * mm, v(67.2, -29.13) * mm]});
            skFitSpline(sketch, "E505", {"points": [v(67.2, -29.13) * mm, v(65.8, -27.8) * mm, v(64.64, -26.17) * mm, v(64.64, -25.5) * mm]});
            skFitSpline(sketch, "E506", {"points": [v(64.64, -25.5) * mm, v(64.64, -24.04) * mm, v(67.42, -21.1) * mm, v(68.8, -21.1) * mm]});
            skFitSpline(sketch, "E507", {"points": [v(68.8, -21.1) * mm, v(69.46, -21.1) * mm, v(69.78, -20.15) * mm, v(69.78, -18.26) * mm]});
            skFitSpline(sketch, "E508", {"points": [v(69.78, -18.26) * mm, v(69.78, -15.43) * mm, v(69.77, -15.42) * mm, v(67.43, -15.86) * mm]});
            skFitSpline(sketch, "E509", {"points": [v(67.43, -15.86) * mm, v(56.81, -17.85) * mm, v(55.79, -29.83) * mm, v(65.74, -35.61) * mm]});
            skFitSpline(sketch, "E510", {"points": [v(65.74, -35.61) * mm, v(69.03, -37.52) * mm, v(69.78, -37.26) * mm, v(69.78, -34.22) * mm]});
            skFitSpline(sketch, "E511", {"points": [v(-41.13, -31.74) * mm, v(-41.13, -29.97) * mm, v(-41.63, -29.72) * mm, v(-43.64, -30.44) * mm]});
            skFitSpline(sketch, "E512", {"points": [v(-43.64, -30.44) * mm, v(-45.6, -31.14) * mm, v(-45.08, -33.46) * mm, v(-42.97, -33.46) * mm]});
            skFitSpline(sketch, "E513", {"points": [v(-42.97, -33.46) * mm, v(-41.5, -33.46) * mm, v(-41.13, -33.12) * mm, v(-41.13, -31.74) * mm]});
            skFitSpline(sketch, "E514", {"points": [v(-46.27, -27.27) * mm, v(-43.68, -25.98) * mm, v(-40.52, -21.16) * mm, v(-39.63, -17.15) * mm]});
            skFitSpline(sketch, "E515", {"points": [v(-39.63, -17.15) * mm, v(-39.1, -14.76) * mm, v(-38.97, -11.16) * mm, v(-39.28, -7.66) * mm]});
            skFitSpline(sketch, "E516", {"points": [v(-42.58, -1.59) * mm, v(-44.12, -1.36) * mm, v(-47.1, -0.08) * mm, v(-49.2, 1.24) * mm]});
            skFitSpline(sketch, "E517", {"points": [v(-49.2, 1.24) * mm, v(-51.31, 2.57) * mm, v(-53.26, 3.65) * mm, v(-53.53, 3.65) * mm]});
            skFitSpline(sketch, "E518", {"points": [v(-53.53, 3.65) * mm, v(-54.14, 3.65) * mm, v(-56.56, -0.07) * mm, v(-56.56, -1) * mm]});
            skFitSpline(sketch, "E519", {"points": [v(-56.56, -1) * mm, v(-56.56, -1.37) * mm, v(-55.1, -2.05) * mm, v(-53.31, -2.52) * mm]});
            skFitSpline(sketch, "E520", {"points": [v(-53.31, -2.52) * mm, v(-47.27, -4.1) * mm, v(-43.37, -9.9) * mm, v(-44.85, -15.1) * mm]});
            skFitSpline(sketch, "E521", {"points": [v(-44.85, -15.1) * mm, v(-46.68, -21.55) * mm, v(-51.58, -24.53) * mm, v(-56.46, -22.17) * mm]});
            skFitSpline(sketch, "E522", {"points": [v(-56.46, -22.17) * mm, v(-58.75, -21.06) * mm, v(-60.96, -18) * mm, v(-60.96, -15.92) * mm]});
            skFitSpline(sketch, "E523", {"points": [v(-60.96, -15.92) * mm, v(-60.96, -15.3) * mm, v(-59.98, -13.88) * mm, v(-58.78, -12.76) * mm]});
            skFitSpline(sketch, "E524", {"points": [v(-58.78, -12.76) * mm, v(-56.95, -11.05) * mm, v(-56.35, -10.84) * mm, v(-55.1, -11.46) * mm]});
            skFitSpline(sketch, "E525", {"points": [v(-55.1, -11.46) * mm, v(-53.03, -12.5) * mm, v(-53.25, -13.25) * mm, v(-55.64, -13.21) * mm]});
            skFitSpline(sketch, "E526", {"points": [v(-55.64, -13.21) * mm, v(-57.45, -13.2) * mm, v(-57.68, -13.45) * mm, v(-57.89, -15.77) * mm]});
            skFitSpline(sketch, "E527", {"points": [v(-57.89, -15.77) * mm, v(-58.09, -18.03) * mm, v(-57.87, -18.43) * mm, v(-56.1, -19.06) * mm]});
            skFitSpline(sketch, "E528", {"points": [v(-56.1, -19.06) * mm, v(-51.14, -20.82) * mm, v(-47.5, -17.9) * mm, v(-47.88, -12.46) * mm]});
            skFitSpline(sketch, "E529", {"points": [v(-47.88, -12.46) * mm, v(-48.17, -8.29) * mm, v(-50.4, -6.56) * mm, v(-56.08, -6.12) * mm]});
            skFitSpline(sketch, "E530", {"points": [v(-56.08, -6.12) * mm, v(-59.8, -5.83) * mm, v(-60.25, -5.97) * mm, v(-62.79, -8.15) * mm]});
            skFitSpline(sketch, "E531", {"points": [v(-62.79, -8.15) * mm, v(-69.59, -13.98) * mm, v(-66.56, -25.95) * mm, v(-57.79, -27.9) * mm]});
            skFitSpline(sketch, "E532", {"points": [v(-57.79, -27.9) * mm, v(-54.24, -28.68) * mm, v(-48.46, -28.37) * mm, v(-46.27, -27.27) * mm]});
            skFitSpline(sketch, "E533", {"points": [v(69.78, -25.21) * mm, v(69.78, -23.6) * mm, v(69.45, -23.15) * mm, v(68.3, -23.15) * mm]});
            skFitSpline(sketch, "E534", {"points": [v(68.3, -23.15) * mm, v(67.17, -23.15) * mm, v(66.84, -23.6) * mm, v(66.84, -25.21) * mm]});
            skFitSpline(sketch, "E535", {"points": [v(66.84, -25.21) * mm, v(66.84, -26.82) * mm, v(67.17, -27.27) * mm, v(68.3, -27.27) * mm]});
            skFitSpline(sketch, "E536", {"points": [v(68.3, -27.27) * mm, v(69.45, -27.27) * mm, v(69.78, -26.82) * mm, v(69.78, -25.21) * mm]});
            skFitSpline(sketch, "E537", {"points": [v(30.34, -23.6) * mm, v(30.98, -22.02) * mm, v(37.6, -18.34) * mm, v(39.79, -18.34) * mm]});
            skFitSpline(sketch, "E538", {"points": [v(39.79, -18.34) * mm, v(42.35, -18.34) * mm, v(42.4, -17.53) * mm, v(40.03, -14.62) * mm]});
            skFitSpline(sketch, "E539", {"points": [v(40.03, -14.62) * mm, v(39.02, -13.38) * mm, v(38.2, -11.98) * mm, v(38.2, -11.5) * mm]});
            skFitSpline(sketch, "E540", {"points": [v(38.2, -11.5) * mm, v(38.2, -10.93) * mm, v(37.6, -10.76) * mm, v(36.54, -11) * mm]});
            skFitSpline(sketch, "E541", {"points": [v(36.54, -11) * mm, v(34.43, -11.5) * mm, v(23.96, -14.96) * mm, v(23.6, -15.28) * mm]});
            skFitSpline(sketch, "E542", {"points": [v(23.6, -15.28) * mm, v(23.46, -15.41) * mm, v(24.2, -17.14) * mm, v(25.26, -19.13) * mm]});
            skFitSpline(sketch, "E543", {"points": [v(25.26, -19.13) * mm, v(26.31, -21.11) * mm, v(27.18, -23.14) * mm, v(27.18, -23.63) * mm]});
            skFitSpline(sketch, "E544", {"points": [v(27.18, -23.63) * mm, v(27.18, -24.81) * mm, v(29.85, -24.79) * mm, v(30.34, -23.6) * mm]});
            skFitSpline(sketch, "E545", {"points": [v(56.41, -20.57) * mm, v(56.93, -19.16) * mm, v(57.53, -17.5) * mm, v(57.75, -16.9) * mm]});
            skFitSpline(sketch, "E546", {"points": [v(57.75, -16.9) * mm, v(58.04, -16.07) * mm, v(57.33, -15.59) * mm, v(54.84, -14.94) * mm]});
            skFitSpline(sketch, "E547", {"points": [v(54.84, -14.94) * mm, v(51.07, -13.95) * mm, v(48.33, -11.58) * mm, v(46.68, -7.88) * mm]});
            skFitSpline(sketch, "E548", {"points": [v(46.68, -7.88) * mm, v(45.31, -4.82) * mm, v(45.27, -2.74) * mm, v(46.53, -0.6) * mm]});
            skFitSpline(sketch, "E549", {"points": [v(46.53, -0.6) * mm, v(47.8, 1.54) * mm, v(51.35, 3.64) * mm, v(53.7, 3.64) * mm]});
            skFitSpline(sketch, "E550", {"points": [v(53.7, 3.64) * mm, v(58.16, 3.66) * mm, v(61.76, -1.88) * mm, v(59.08, -4.64) * mm]});
            skFitSpline(sketch, "E551", {"points": [v(59.08, -4.64) * mm, v(57.76, -6.01) * mm, v(55.82, -6.44) * mm, v(55.82, -5.36) * mm]});
            skFitSpline(sketch, "E552", {"points": [v(55.82, -5.36) * mm, v(55.82, -5.02) * mm, v(56.32, -4.57) * mm, v(56.92, -4.35) * mm]});
            skFitSpline(sketch, "E553", {"points": [v(56.92, -4.35) * mm, v(58.52, -3.78) * mm, v(58.3, -0.66) * mm, v(56.6, 0.19) * mm]});
            skFitSpline(sketch, "E554", {"points": [v(56.6, 0.19) * mm, v(54.4, 1.3) * mm, v(52.97, 1.04) * mm, v(51.01, -0.79) * mm]});
            skFitSpline(sketch, "E555", {"points": [v(51.01, -0.79) * mm, v(46.91, -4.62) * mm, v(49.75, -11.47) * mm, v(55.45, -11.47) * mm]});
            skFitSpline(sketch, "E556", {"points": [v(55.45, -11.47) * mm, v(64.14, -11.47) * mm, v(68.49, -4.5) * mm, v(64.45, 2.98) * mm]});
            skFitSpline(sketch, "E557", {"points": [v(64.45, 2.98) * mm, v(60.43, 10.44) * mm, v(50.39, 11.43) * mm, v(43.53, 5.04) * mm]});
            skFitSpline(sketch, "E558", {"points": [v(43.53, 5.04) * mm, v(42.23, 3.82) * mm, v(40.85, 1.76) * mm, v(40.46, 0.45) * mm]});
            skFitSpline(sketch, "E559", {"points": [v(40.46, 0.45) * mm, v(39.62, -2.4) * mm, v(40.64, -9.27) * mm, v(42.37, -12.42) * mm]});
            skFitSpline(sketch, "E560", {"points": [v(42.37, -12.42) * mm, v(43.97, -15.32) * mm, v(52.58, -23.15) * mm, v(54.18, -23.15) * mm]});
            skFitSpline(sketch, "E561", {"points": [v(54.18, -23.15) * mm, v(55, -23.15) * mm, v(55.8, -22.23) * mm, v(56.41, -20.57) * mm]});
            skFitSpline(sketch, "E562", {"points": [v(-30.01, -15.6) * mm, v(-28.25, -14.86) * mm, v(-25.9, -14.24) * mm, v(-24.79, -14.23) * mm]});
            skFitSpline(sketch, "E563", {"points": [v(-24.79, -14.23) * mm, v(-22.05, -14.21) * mm, v(-22.25, -13.18) * mm, v(-25.66, -9.72) * mm]});
            skFitSpline(sketch, "E564", {"points": [v(-25.66, -9.72) * mm, v(-27.31, -8.04) * mm, v(-28.91, -5.52) * mm, v(-29.41, -3.8) * mm]});
            skFitSpline(sketch, "E565", {"points": [v(-29.41, -3.8) * mm, v(-29.9, -2.16) * mm, v(-30.4, -0.43) * mm, v(-30.55, 0.05) * mm]});
            skFitSpline(sketch, "E566", {"points": [v(-30.55, 0.05) * mm, v(-30.76, 0.74) * mm, v(-31.3, 0.73) * mm, v(-33.22, 0) * mm]});
            skFitSpline(sketch, "E567", {"points": [v(-33.22, 0) * mm, v(-35.23, -0.79) * mm, v(-35.6, -1.26) * mm, v(-35.46, -2.94) * mm]});
            skFitSpline(sketch, "E568", {"points": [v(-35.46, -2.94) * mm, v(-35.37, -4.04) * mm, v(-35.07, -7.65) * mm, v(-34.8, -10.95) * mm]});
            skFitSpline(sketch, "E569", {"points": [v(-34.8, -10.95) * mm, v(-34.54, -14.26) * mm, v(-34.07, -16.97) * mm, v(-33.77, -16.97) * mm]});
            skFitSpline(sketch, "E570", {"points": [v(-33.77, -16.97) * mm, v(-33.46, -16.97) * mm, v(-31.77, -16.36) * mm, v(-30.01, -15.6) * mm]});
            skFitSpline(sketch, "E571", {"points": [v(69.78, -10.39) * mm, v(69.78, -8.13) * mm, v(67.32, -8.33) * mm, v(66.97, -10.62) * mm]});
            skFitSpline(sketch, "E572", {"points": [v(66.97, -10.62) * mm, v(66.8, -11.79) * mm, v(67.1, -12.16) * mm, v(68.26, -12.16) * mm]});
            skFitSpline(sketch, "E573", {"points": [v(68.26, -12.16) * mm, v(69.4, -12.16) * mm, v(69.78, -11.72) * mm, v(69.78, -10.39) * mm]});
            skFitSpline(sketch, "E574", {"points": [v(-0.18, -8.82) * mm, v(2.34, -7.62) * mm, v(4.4, -6.26) * mm, v(4.4, -5.79) * mm]});
            skFitSpline(sketch, "E575", {"points": [v(4.4, -5.79) * mm, v(4.37, -3.76) * mm, v(2.24, 0.58) * mm, v(1.17, 0.78) * mm]});
            skFitSpline(sketch, "E576", {"points": [v(1.17, 0.78) * mm, v(0.53, 0.9) * mm, v(0, 0.55) * mm, v(0, 0) * mm]});
            skFitSpline(sketch, "E577", {"points": [v(0, 0) * mm, v(0, -1.63) * mm, v(-5.45, -5.74) * mm, v(-8.27, -6.24) * mm]});
            skFitSpline(sketch, "E578", {"points": [v(-8.27, -6.24) * mm, v(-11.83, -6.86) * mm, v(-16.62, -5.02) * mm, v(-18.02, -2.48) * mm]});
            skFitSpline(sketch, "E579", {"points": [v(-18.02, -2.48) * mm, v(-20.37, 1.75) * mm, v(-18.5, 7.08) * mm, v(-14.32, 8.06) * mm]});
            skFitSpline(sketch, "E580", {"points": [v(-14.32, 8.06) * mm, v(-10.8, 8.88) * mm, v(-6.97, 5.39) * mm, v(-8.95, 3.15) * mm]});
            skFitSpline(sketch, "E581", {"points": [v(-8.95, 3.15) * mm, v(-9.8, 2.19) * mm, v(-9.96, 2.3) * mm, v(-10.29, 4.06) * mm]});
            skFitSpline(sketch, "E582", {"points": [v(-10.29, 4.06) * mm, v(-11.03, 8.03) * mm, v(-16.16, 6.4) * mm, v(-16.16, 2.2) * mm]});
            skFitSpline(sketch, "E583", {"points": [v(-16.16, 2.2) * mm, v(-16.16, -2.8) * mm, v(-8.64, -5.18) * mm, v(-4.66, -1.46) * mm]});
            skFitSpline(sketch, "E584", {"points": [v(-4.66, -1.46) * mm, v(-2.94, 0.15) * mm, v(-2.8, 0.7) * mm, v(-3.08, 4.82) * mm]});
            skFitSpline(sketch, "E585", {"points": [v(-3.08, 4.82) * mm, v(-3.35, 8.84) * mm, v(-3.64, 9.54) * mm, v(-5.7, 11.26) * mm]});
            skFitSpline(sketch, "E586", {"points": [v(-5.7, 11.26) * mm, v(-6.97, 12.33) * mm, v(-9.22, 13.4) * mm, v(-10.69, 13.67) * mm]});
            skFitSpline(sketch, "E587", {"points": [v(-10.69, 13.67) * mm, v(-15.86, 14.57) * mm, v(-22.3, 11.45) * mm, v(-24.23, 7.1) * mm]});
            skFitSpline(sketch, "E588", {"points": [v(-24.23, 7.1) * mm, v(-25.47, 4.31) * mm, v(-24.89, -2.2) * mm, v(-23.1, -5.63) * mm]});
            skFitSpline(sketch, "E589", {"points": [v(-23.1, -5.63) * mm, v(-19.84, -11.88) * mm, v(-9.63, -13.3) * mm, v(-0.18, -8.82) * mm]});
            skFitSpline(sketch, "E590", {"points": [v(-68.02, -9.7) * mm, v(-67.28, -7.88) * mm, v(-67.5, -7.35) * mm, v(-69.04, -7.35) * mm]});
            skFitSpline(sketch, "E591", {"points": [v(-69.04, -7.35) * mm, v(-70.12, -7.35) * mm, v(-70.51, -7.8) * mm, v(-70.51, -9.06) * mm]});
            skFitSpline(sketch, "E592", {"points": [v(-70.51, -9.06) * mm, v(-70.51, -10.98) * mm, v(-68.73, -11.43) * mm, v(-68.02, -9.7) * mm]});
            skFitSpline(sketch, "E593", {"points": [v(35.42, -4.75) * mm, v(34.9, 3.09) * mm, v(40.6, 11.3) * mm, v(47.93, 13.22) * mm]});
            skFitSpline(sketch, "E594", {"points": [v(47.93, 13.22) * mm, v(50, 13.76) * mm, v(51.42, 14.53) * mm, v(51.42, 15.11) * mm]});
            skFitSpline(sketch, "E595", {"points": [v(51.42, 15.11) * mm, v(51.42, 16.38) * mm, v(49.33, 20.15) * mm, v(48.64, 20.13) * mm]});
            skFitSpline(sketch, "E596", {"points": [v(48.64, 20.13) * mm, v(48.35, 20.12) * mm, v(45.84, 19.04) * mm, v(43.06, 17.72) * mm]});
            skFitSpline(sketch, "E597", {"points": [v(43.06, 17.72) * mm, v(39.59, 16.08) * mm, v(37.02, 15.33) * mm, v(34.8, 15.33) * mm]});
            skFitSpline(sketch, "E598", {"points": [v(34.8, 15.33) * mm, v(31.2, 15.33) * mm, v(31.08, 15.11) * mm, v(32.79, 11.91) * mm]});
            skFitSpline(sketch, "E599", {"points": [v(32.79, 11.91) * mm, v(34.8, 8.14) * mm, v(34.84, 4.4) * mm, v(32.92, 0.9) * mm]});
            skFitSpline(sketch, "E600", {"points": [v(32.92, 0.9) * mm, v(29.7, -4.95) * mm, v(23.18, -6.65) * mm, v(17.2, -3.19) * mm]});
            skFitSpline(sketch, "E601", {"points": [v(17.2, -3.19) * mm, v(13.78, -1.21) * mm, v(12.69, 1.7) * mm, v(14.01, 5.28) * mm]});
            skFitSpline(sketch, "E602", {"points": [v(14.01, 5.28) * mm, v(15.9, 10.38) * mm, v(21.72, 11.67) * mm, v(24.23, 7.55) * mm]});
            skFitSpline(sketch, "E603", {"points": [v(24.23, 7.55) * mm, v(25.2, 5.95) * mm, v(25.2, 5.63) * mm, v(24.2, 4.7) * mm]});
            skFitSpline(sketch, "E604", {"points": [v(24.2, 4.7) * mm, v(23.2, 3.75) * mm, v(23.08, 3.84) * mm, v(23.1, 5.54) * mm]});
            skFitSpline(sketch, "E605", {"points": [v(23.1, 5.54) * mm, v(23.13, 7.1) * mm, v(22.79, 7.47) * mm, v(21.07, 7.65) * mm]});
            skFitSpline(sketch, "E606", {"points": [v(21.07, 7.65) * mm, v(19.94, 7.77) * mm, v(18.53, 7.5) * mm, v(17.95, 7.05) * mm]});
            skFitSpline(sketch, "E607", {"points": [v(17.95, 7.05) * mm, v(16.4, 5.85) * mm, v(16.66, 2.05) * mm, v(18.42, -0.04) * mm]});
            skFitSpline(sketch, "E608", {"points": [v(18.42, -0.04) * mm, v(19.68, -1.54) * mm, v(20.53, -1.85) * mm, v(23.44, -1.85) * mm]});
            skFitSpline(sketch, "E609", {"points": [v(23.44, -1.85) * mm, v(27.67, -1.85) * mm, v(29.3, -0.48) * mm, v(30.17, 3.8) * mm]});
            skFitSpline(sketch, "E610", {"points": [v(30.17, 3.8) * mm, v(30.97, 7.78) * mm, v(29.84, 11.41) * mm, v(27.1, 13.56) * mm]});
            skFitSpline(sketch, "E611", {"points": [v(27.1, 13.56) * mm, v(25.24, 15.03) * mm, v(24.11, 15.33) * mm, v(20.47, 15.33) * mm]});
            skFitSpline(sketch, "E612", {"points": [v(20.47, 15.33) * mm, v(13.65, 15.33) * mm, v(9.66, 12.7) * mm, v(8.1, 7.18) * mm]});
            skFitSpline(sketch, "E613", {"points": [v(8.1, 7.18) * mm, v(6.65, 2.1) * mm, v(8.61, -4.92) * mm, v(12.06, -7.03) * mm]});
            skFitSpline(sketch, "E614", {"points": [v(12.06, -7.03) * mm, v(17.25, -10.2) * mm, v(22.95, -10.76) * mm, v(30.85, -8.85) * mm]});
            skFitSpline(sketch, "E615", {"points": [v(-63.47, -0.74) * mm, v(-56.89, 2.18) * mm, v(-55.49, 12.37) * mm, v(-60.97, 17.5) * mm]});
            skFitSpline(sketch, "E616", {"points": [v(-60.97, 17.5) * mm, v(-62.71, 19.13) * mm, v(-63.67, 19.45) * mm, v(-66.78, 19.45) * mm]});
            skFitSpline(sketch, "E617", {"points": [v(-70.51, 16.65) * mm, v(-70.51, 13.92) * mm, v(-70.46, 13.86) * mm, v(-68.4, 14.28) * mm]});
            skFitSpline(sketch, "E618", {"points": [v(-68.4, 14.28) * mm, v(-66.66, 14.64) * mm, v(-65.99, 14.38) * mm, v(-64.72, 12.87) * mm]});
            skFitSpline(sketch, "E619", {"points": [v(-64.72, 12.87) * mm, v(-63.87, 11.85) * mm, v(-63.17, 10.33) * mm, v(-63.17, 9.5) * mm]});
            skFitSpline(sketch, "E620", {"points": [v(-63.17, 9.5) * mm, v(-63.17, 7.43) * mm, v(-65.55, 4.72) * mm, v(-68.28, 3.66) * mm]});
            skFitSpline(sketch, "E621", {"points": [v(-68.28, 3.66) * mm, v(-70.14, 2.94) * mm, v(-70.51, 2.41) * mm, v(-70.51, 0.47) * mm]});
            skFitSpline(sketch, "E622", {"points": [v(-70.51, 0.47) * mm, v(-70.51, -1.66) * mm, v(-70.33, -1.85) * mm, v(-68.24, -1.85) * mm]});
            skFitSpline(sketch, "E623", {"points": [v(-68.24, -1.85) * mm, v(-66.98, -1.85) * mm, v(-64.84, -1.35) * mm, v(-63.47, -0.74) * mm]});
            skFitSpline(sketch, "E624", {"points": [v(-35.32, 3.63) * mm, v(-30.03, 5.05) * mm, v(-26.58, 10.1) * mm, v(-25.93, 17.37) * mm]});
            skFitSpline(sketch, "E625", {"points": [v(-25.93, 17.37) * mm, v(-25.7, 19.93) * mm, v(-25.73, 23.12) * mm, v(-26, 24.44) * mm]});
            skFitSpline(sketch, "E626", {"points": [v(-26, 24.44) * mm, v(-26.42, 26.58) * mm, v(-26.84, 26.94) * mm, v(-29.78, 27.71) * mm]});
            skFitSpline(sketch, "E627", {"points": [v(-29.78, 27.71) * mm, v(-31.6, 28.19) * mm, v(-33.29, 28.4) * mm, v(-33.53, 28.18) * mm]});
            skFitSpline(sketch, "E628", {"points": [v(-33.53, 28.18) * mm, v(-33.76, 27.95) * mm, v(-33.1, 26.15) * mm, v(-32.04, 24.17) * mm]});
            skFitSpline(sketch, "E629", {"points": [v(-32.04, 24.17) * mm, v(-30.98, 22.18) * mm, v(-30.12, 19.92) * mm, v(-30.13, 19.15) * mm]});
            skFitSpline(sketch, "E630", {"points": [v(-30.13, 19.15) * mm, v(-30.18, 15.03) * mm, v(-35.74, 8.46) * mm, v(-39.17, 8.46) * mm]});
            skFitSpline(sketch, "E631", {"points": [v(-39.17, 8.46) * mm, v(-41.54, 8.47) * mm, v(-45.47, 10.96) * mm, v(-46.3, 12.97) * mm]});
            skFitSpline(sketch, "E632", {"points": [v(-46.3, 12.97) * mm, v(-47.4, 15.72) * mm, v(-47.17, 16.66) * mm, v(-44.82, 18.85) * mm]});
            skFitSpline(sketch, "E633", {"points": [v(-44.82, 18.85) * mm, v(-43, 20.56) * mm, v(-42.4, 20.78) * mm, v(-41.15, 20.15) * mm]});
            skFitSpline(sketch, "E634", {"points": [v(-41.15, 20.15) * mm, v(-38.98, 19.06) * mm, v(-39.33, 18.27) * mm, v(-41.83, 18.62) * mm]});
            skFitSpline(sketch, "E635", {"points": [v(-41.83, 18.62) * mm, v(-43.66, 18.87) * mm, v(-44.08, 18.64) * mm, v(-44.47, 17.19) * mm]});
            skFitSpline(sketch, "E636", {"points": [v(-44.47, 17.19) * mm, v(-45.43, 13.58) * mm, v(-41.72, 10.97) * mm, v(-37.54, 12.32) * mm]});
            skFitSpline(sketch, "E637", {"points": [v(-37.54, 12.32) * mm, v(-34.81, 13.2) * mm, v(-32.67, 17.51) * mm, v(-33.54, 20.36) * mm]});
            skFitSpline(sketch, "E638", {"points": [v(-33.54, 20.36) * mm, v(-34.48, 23.43) * mm, v(-38.28, 25.64) * mm, v(-42.61, 25.64) * mm]});
            skFitSpline(sketch, "E639", {"points": [v(-42.61, 25.64) * mm, v(-47.92, 25.64) * mm, v(-51.32, 22.54) * mm, v(-52.4, 16.7) * mm]});
            skFitSpline(sketch, "E640", {"points": [v(-52.4, 16.7) * mm, v(-53.5, 10.74) * mm, v(-49.92, 5.54) * mm, v(-43.6, 3.95) * mm]});
            skFitSpline(sketch, "E641", {"points": [v(-43.6, 3.95) * mm, v(-39.14, 2.83) * mm, v(-38.4, 2.8) * mm, v(-35.32, 3.63) * mm]});
            skFitSpline(sketch, "E642", {"points": [v(69.78, 8.8) * mm, v(69.78, 12.6) * mm, v(69.59, 13.27) * mm, v(68.5, 13.25) * mm]});
            skFitSpline(sketch, "E643", {"points": [v(68.5, 13.25) * mm, v(67.02, 13.22) * mm, v(64.64, 11.7) * mm, v(64.63, 10.79) * mm]});
            skFitSpline(sketch, "E644", {"points": [v(64.63, 10.79) * mm, v(64.63, 10.45) * mm, v(65.38, 8.86) * mm, v(66.29, 7.26) * mm]});
            skFitSpline(sketch, "E645", {"points": [v(66.29, 7.26) * mm, v(68.7, 2.98) * mm, v(69.78, 3.45) * mm, v(69.78, 8.8) * mm]});
            skFitSpline(sketch, "E646", {"points": [v(-66.96, 7.5) * mm, v(-65.8, 8.26) * mm, v(-65.35, 9.14) * mm, v(-65.51, 10.42) * mm]});
            skFitSpline(sketch, "E647", {"points": [v(-65.51, 10.42) * mm, v(-65.7, 11.94) * mm, v(-66.1, 12.24) * mm, v(-67.94, 12.24) * mm]});
            skFitSpline(sketch, "E648", {"points": [v(-67.94, 12.24) * mm, v(-70, 12.24) * mm, v(-70.16, 12.06) * mm, v(-70.37, 9.32) * mm]});
            skFitSpline(sketch, "E649", {"points": [v(-70.37, 9.32) * mm, v(-70.62, 6.07) * mm, v(-69.8, 5.63) * mm, v(-66.96, 7.5) * mm]});
            skFitSpline(sketch, "E650", {"points": [v(3.69, 8.85) * mm, v(4.7, 11.7) * mm, v(4.75, 11.6) * mm, v(1.65, 12.21) * mm]});
            skFitSpline(sketch, "E651", {"points": [v(1.65, 12.21) * mm, v(-1.05, 12.76) * mm, v(-1.25, 12.3) * mm, v(0.15, 8.68) * mm]});
            skFitSpline(sketch, "E652", {"points": [v(0.15, 8.68) * mm, v(1.3, 5.72) * mm, v(2.6, 5.78) * mm, v(3.69, 8.85) * mm]});
            skFitSpline(sketch, "E653", {"points": [v(10.04, 17.18) * mm, v(11.99, 18.57) * mm, v(13.7, 19.1) * mm, v(16.97, 19.33) * mm]});
            skFitSpline(sketch, "E654", {"points": [v(16.97, 19.33) * mm, v(19.35, 19.49) * mm, v(21.3, 19.78) * mm, v(21.3, 19.98) * mm]});
            skFitSpline(sketch, "E655", {"points": [v(21.3, 19.98) * mm, v(21.3, 20.17) * mm, v(20.4, 22.13) * mm, v(19.28, 24.33) * mm]});
            skFitSpline(sketch, "E656", {"points": [v(19.28, 24.33) * mm, v(17.2, 28.43) * mm, v(15.85, 29.34) * mm, v(15.1, 27.12) * mm]});
            skFitSpline(sketch, "E657", {"points": [v(15.1, 27.12) * mm, v(14.4, 25.05) * mm, v(11.4, 22.87) * mm, v(7.95, 21.9) * mm]});
            skFitSpline(sketch, "E658", {"points": [v(7.95, 21.9) * mm, v(3.67, 20.69) * mm, v(-0.21, 21.87) * mm, v(-3.49, 25.38) * mm]});
            skFitSpline(sketch, "E659", {"points": [v(-3.49, 25.38) * mm, v(-6.66, 28.76) * mm, v(-6.69, 31.6) * mm, v(-3.6, 34.9) * mm]});
            skFitSpline(sketch, "E660", {"points": [v(-3.6, 34.9) * mm, v(-0.76, 37.92) * mm, v(2.53, 38.2) * mm, v(5.1, 35.64) * mm]});
            skFitSpline(sketch, "E661", {"points": [v(5.1, 35.64) * mm, v(6.95, 33.8) * mm, v(6.8, 30.93) * mm, v(4.81, 30.22) * mm]});
            skFitSpline(sketch, "E662", {"points": [v(4.81, 30.22) * mm, v(3.92, 29.9) * mm, v(3.88, 30.12) * mm, v(4.55, 31.5) * mm]});
            skFitSpline(sketch, "E663", {"points": [v(4.55, 31.5) * mm, v(5.55, 33.56) * mm, v(4.3, 35.26) * mm, v(1.79, 35.26) * mm]});
            skFitSpline(sketch, "E664", {"points": [v(1.79, 35.26) * mm, v(-2.13, 35.26) * mm, v(-3.62, 28.96) * mm, v(-0.4, 25.95) * mm]});
            skFitSpline(sketch, "E665", {"points": [v(-0.4, 25.95) * mm, v(4.76, 21.12) * mm, v(13.67, 27.45) * mm, v(12.17, 34.9) * mm]});
            skFitSpline(sketch, "E666", {"points": [v(12.17, 34.9) * mm, v(11.21, 39.68) * mm, v(6.81, 42.82) * mm, v(1.07, 42.82) * mm]});
            skFitSpline(sketch, "E667", {"points": [v(1.07, 42.82) * mm, v(-5.62, 42.82) * mm, v(-9.58, 39.43) * mm, v(-11.16, 32.36) * mm]});
            skFitSpline(sketch, "E668", {"points": [v(-11.16, 32.36) * mm, v(-11.9, 29.11) * mm, v(-11.83, 28.1) * mm, v(-10.76, 25.48) * mm]});
            skFitSpline(sketch, "E669", {"points": [v(-10.76, 25.48) * mm, v(-9.31, 21.92) * mm, v(-5.19, 18.5) * mm, v(-0.1, 16.64) * mm]});
            skFitSpline(sketch, "E670", {"points": [v(-0.1, 16.64) * mm, v(4.65, 14.9) * mm, v(7.02, 15.03) * mm, v(10.04, 17.18) * mm]});
            skFitSpline(sketch, "E671", {"points": [v(-14.87, 17.17) * mm, v(-12.75, 17.4) * mm, v(-11.02, 17.84) * mm, v(-11.02, 18.15) * mm]});
            skFitSpline(sketch, "E672", {"points": [v(-11.02, 18.15) * mm, v(-11.02, 18.45) * mm, v(-11.83, 19.83) * mm, v(-12.83, 21.2) * mm]});
            skFitSpline(sketch, "E673", {"points": [v(-12.83, 21.2) * mm, v(-13.83, 22.58) * mm, v(-15.06, 24.79) * mm, v(-15.57, 26.1) * mm]});
            skFitSpline(sketch, "E674", {"points": [v(-15.57, 26.1) * mm, v(-16.4, 28.27) * mm, v(-16.7, 28.46) * mm, v(-18.66, 28.1) * mm]});
            skFitSpline(sketch, "E675", {"points": [v(-18.66, 28.1) * mm, v(-19.85, 27.87) * mm, v(-20.9, 27.61) * mm, v(-20.97, 27.52) * mm]});
            skFitSpline(sketch, "E676", {"points": [v(-20.97, 27.52) * mm, v(-21.05, 27.43) * mm, v(-21.35, 24.76) * mm, v(-21.63, 21.6) * mm]});
            skFitSpline(sketch, "E677", {"points": [v(-20.44, 16.3) * mm, v(-19.5, 16.55) * mm, v(-17, 16.94) * mm, v(-14.87, 17.17) * mm]});
            skFitSpline(sketch, "E678", {"points": [v(67.07, 16.8) * mm, v(69.38, 17.94) * mm, v(69.75, 18.72) * mm, v(69.77, 22.33) * mm]});
            skFitSpline(sketch, "E679", {"points": [v(69.77, 22.33) * mm, v(69.78, 27.04) * mm, v(66.16, 29.57) * mm, v(61.96, 27.78) * mm]});
            skFitSpline(sketch, "E680", {"points": [v(61.96, 27.78) * mm, v(60.55, 27.18) * mm, v(60.19, 26.57) * mm, v(60.36, 25.12) * mm]});
            skFitSpline(sketch, "E681", {"points": [v(60.36, 25.12) * mm, v(60.55, 23.65) * mm, v(61.07, 23.16) * mm, v(62.73, 22.9) * mm]});
            skFitSpline(sketch, "E682", {"points": [v(62.73, 22.9) * mm, v(64.65, 22.58) * mm, v(64.74, 22.45) * mm, v(63.66, 21.61) * mm]});
            skFitSpline(sketch, "E683", {"points": [v(63.66, 21.61) * mm, v(62.15, 20.45) * mm, v(60.66, 20.94) * mm, v(59.14, 23.12) * mm]});
            skFitSpline(sketch, "E684", {"points": [v(59.14, 23.12) * mm, v(57.67, 25.22) * mm, v(58.25, 27.7) * mm, v(60.72, 29.87) * mm]});
            skFitSpline(sketch, "E685", {"points": [v(60.72, 29.87) * mm, v(62.18, 31.16) * mm, v(63.3, 31.46) * mm, v(66.2, 31.38) * mm]});
            skFitSpline(sketch, "E686", {"points": [v(64.14, 36.3) * mm, v(59.55, 36.3) * mm, v(58.62, 36.07) * mm, v(56.89, 34.57) * mm]});
            skFitSpline(sketch, "E687", {"points": [v(56.89, 34.57) * mm, v(51.59, 30) * mm, v(51.5, 20.51) * mm, v(56.72, 17.1) * mm]});
            skFitSpline(sketch, "E688", {"points": [v(56.72, 17.1) * mm, v(58.64, 15.83) * mm, v(64.75, 15.66) * mm, v(67.07, 16.8) * mm]});
            skFitSpline(sketch, "E689", {"points": [v(43.72, 21.47) * mm, v(48.18, 23.37) * mm, v(48.48, 23.63) * mm, v(48.48, 25.77) * mm]});
            skFitSpline(sketch, "E690", {"points": [v(48.48, 25.77) * mm, v(48.49, 29.43) * mm, v(49.87, 33.07) * mm, v(52.19, 35.54) * mm]});
            skFitSpline(sketch, "E691", {"points": [v(52.19, 35.54) * mm, v(54.8, 38.33) * mm, v(54.92, 39.38) * mm, v(52.6, 39.38) * mm]});
            skFitSpline(sketch, "E692", {"points": [v(52.6, 39.38) * mm, v(51.65, 39.38) * mm, v(49.87, 39.57) * mm, v(48.66, 39.8) * mm]});
            skFitSpline(sketch, "E693", {"points": [v(46.15, 35.79) * mm, v(45.9, 32.07) * mm, v(45.47, 30.91) * mm, v(43.47, 28.55) * mm]});
            skFitSpline(sketch, "E694", {"points": [v(43.47, 28.55) * mm, v(38.35, 22.5) * mm, v(29.29, 23.27) * mm, v(27.53, 29.9) * mm]});
            skFitSpline(sketch, "E695", {"points": [v(27.53, 29.9) * mm, v(25.94, 35.9) * mm, v(33.78, 41.25) * mm, v(36.6, 36.1) * mm]});
            skFitSpline(sketch, "E696", {"points": [v(36.6, 36.1) * mm, v(37.32, 34.8) * mm, v(36.97, 33.2) * mm, v(35.98, 33.2) * mm]});
            skFitSpline(sketch, "E697", {"points": [v(35.98, 33.2) * mm, v(35.64, 33.2) * mm, v(35.25, 33.9) * mm, v(35.12, 34.74) * mm]});
            skFitSpline(sketch, "E698", {"points": [v(35.12, 34.74) * mm, v(34.6, 38.16) * mm, v(30.11, 36.19) * mm, v(30.11, 32.54) * mm]});
            skFitSpline(sketch, "E699", {"points": [v(30.11, 32.54) * mm, v(30.11, 29.36) * mm, v(32.4, 27.36) * mm, v(35.94, 27.45) * mm]});
            skFitSpline(sketch, "E700", {"points": [v(35.94, 27.45) * mm, v(37.69, 27.5) * mm, v(39.57, 28.03) * mm, v(40.38, 28.72) * mm]});
            skFitSpline(sketch, "E701", {"points": [v(40.38, 28.72) * mm, v(43.48, 31.34) * mm, v(43.07, 38.36) * mm, v(39.63, 41.58) * mm]});
            skFitSpline(sketch, "E702", {"points": [v(39.63, 41.58) * mm, v(37.9, 43.2) * mm, v(36.97, 43.5) * mm, v(33.66, 43.5) * mm]});
            skFitSpline(sketch, "E703", {"points": [v(33.66, 43.5) * mm, v(26.26, 43.5) * mm, v(22.03, 39.37) * mm, v(22.05, 32.17) * mm]});
            skFitSpline(sketch, "E704", {"points": [v(22.05, 32.17) * mm, v(22.07, 26.96) * mm, v(24.05, 22.71) * mm, v(27.32, 20.85) * mm]});
            skFitSpline(sketch, "E705", {"points": [v(27.32, 20.85) * mm, v(31.1, 18.68) * mm, v(37.74, 18.94) * mm, v(43.72, 21.47) * mm]});
            skFitSpline(sketch, "E706", {"points": [v(-55.07, 21) * mm, v(-55.06, 21.47) * mm, v(-54.4, 22.63) * mm, v(-53.62, 23.58) * mm]});
            skFitSpline(sketch, "E707", {"points": [v(-53.62, 23.58) * mm, v(-51.31, 26.34) * mm, v(-52.23, 29.2) * mm, v(-54.76, 27.13) * mm]});
            skFitSpline(sketch, "E708", {"points": [v(-54.76, 27.13) * mm, v(-55.14, 26.82) * mm, v(-56.86, 26.18) * mm, v(-58.58, 25.73) * mm]});
            skFitSpline(sketch, "E709", {"points": [v(-58.58, 25.73) * mm, v(-60.3, 25.27) * mm, v(-61.7, 24.59) * mm, v(-61.7, 24.2) * mm]});
            skFitSpline(sketch, "E710", {"points": [v(-61.7, 24.2) * mm, v(-61.7, 23.14) * mm, v(-57.81, 20.19) * mm, v(-56.37, 20.16) * mm]});
            skFitSpline(sketch, "E711", {"points": [v(-56.37, 20.16) * mm, v(-55.67, 20.15) * mm, v(-55.08, 20.53) * mm, v(-55.07, 21) * mm]});
            skFitSpline(sketch, "E712", {"points": [v(-55.9, 30.29) * mm, v(-50.73, 32.73) * mm, v(-48.93, 35.76) * mm, v(-48.9, 42.1) * mm]});
            skFitSpline(sketch, "E713", {"points": [v(-48.9, 42.1) * mm, v(-48.88, 47.39) * mm, v(-50.35, 50.48) * mm, v(-53.81, 52.45) * mm]});
            skFitSpline(sketch, "E714", {"points": [v(-53.81, 52.45) * mm, v(-59.15, 55.49) * mm, v(-66.7, 54.5) * mm, v(-69.27, 50.42) * mm]});
            skFitSpline(sketch, "E715", {"points": [v(-69.27, 50.42) * mm, v(-71.09, 47.54) * mm, v(-70.94, 41.45) * mm, v(-69, 39.13) * mm]});
            skFitSpline(sketch, "E716", {"points": [v(-69, 39.13) * mm, v(-67.73, 37.63) * mm, v(-66.87, 37.32) * mm, v(-63.96, 37.32) * mm]});
            skFitSpline(sketch, "E717", {"points": [v(-63.96, 37.32) * mm, v(-61.55, 37.32) * mm, v(-60.1, 37.7) * mm, v(-59.3, 38.52) * mm]});
            skFitSpline(sketch, "E718", {"points": [v(-59.3, 38.52) * mm, v(-56.12, 41.83) * mm, v(-57.6, 47.24) * mm, v(-61.56, 46.81) * mm]});
            skFitSpline(sketch, "E719", {"points": [v(-61.56, 46.81) * mm, v(-63.1, 46.65) * mm, v(-63.61, 46.15) * mm, v(-63.91, 44.54) * mm]});
            skFitSpline(sketch, "E720", {"points": [v(-63.91, 44.54) * mm, v(-64.18, 43.11) * mm, v(-64.49, 42.75) * mm, v(-64.9, 43.37) * mm]});
            skFitSpline(sketch, "E721", {"points": [v(-64.9, 43.37) * mm, v(-65.88, 44.83) * mm, v(-64.74, 47.62) * mm, v(-62.83, 48.43) * mm]});
            skFitSpline(sketch, "E722", {"points": [v(-62.83, 48.43) * mm, v(-60.25, 49.53) * mm, v(-57.44, 48.59) * mm, v(-55.8, 46.07) * mm]});
            skFitSpline(sketch, "E723", {"points": [v(-55.8, 46.07) * mm, v(-52.76, 41.4) * mm, v(-54.67, 37) * mm, v(-60.67, 34.85) * mm]});
            skFitSpline(sketch, "E724", {"points": [v(-60.67, 34.85) * mm, v(-63.44, 33.86) * mm, v(-64.45, 33.8) * mm, v(-66.4, 34.46) * mm]});
            skFitSpline(sketch, "E725", {"points": [v(-66.4, 34.46) * mm, v(-70.22, 35.75) * mm, v(-70.51, 35.56) * mm, v(-70.51, 31.82) * mm]});
            skFitSpline(sketch, "E726", {"points": [v(-65.19, 28.4) * mm, v(-60.86, 28.4) * mm, v(-59.12, 28.76) * mm, v(-55.9, 30.29) * mm]});
            skFitSpline(sketch, "E727", {"points": [v(-38.2, 31.24) * mm, v(-38.2, 31.61) * mm, v(-39.02, 32.93) * mm, v(-40.03, 34.17) * mm]});
            skFitSpline(sketch, "E728", {"points": [v(-40.03, 34.17) * mm, v(-41.04, 35.4) * mm, v(-41.87, 36.78) * mm, v(-41.87, 37.22) * mm]});
            skFitSpline(sketch, "E729", {"points": [v(-41.87, 37.22) * mm, v(-41.87, 38.94) * mm, v(-44.1, 37.88) * mm, v(-45.09, 35.69) * mm]});
            skFitSpline(sketch, "E730", {"points": [v(-45.09, 35.69) * mm, v(-45.66, 34.41) * mm, v(-46.49, 33.16) * mm, v(-46.93, 32.9) * mm]});
            skFitSpline(sketch, "E731", {"points": [v(-46.93, 32.9) * mm, v(-47.38, 32.64) * mm, v(-47.74, 31.9) * mm, v(-47.74, 31.27) * mm]});
            skFitSpline(sketch, "E732", {"points": [v(-47.74, 31.27) * mm, v(-47.75, 30.27) * mm, v(-47.06, 30.14) * mm, v(-42.97, 30.34) * mm]});
            skFitSpline(sketch, "E733", {"points": [v(-42.97, 30.34) * mm, v(-40.34, 30.46) * mm, v(-38.2, 30.87) * mm, v(-38.2, 31.24) * mm]});
            skFitSpline(sketch, "E734", {"points": [v(-18.1, 31.9) * mm, v(-16.87, 32.43) * mm, v(-16.13, 33.45) * mm, v(-15.8, 35.07) * mm]});
            skFitSpline(sketch, "E735", {"points": [v(-15.8, 35.07) * mm, v(-15.19, 38.18) * mm, v(-15.64, 38.5) * mm, v(-18.76, 37.1) * mm]});
            skFitSpline(sketch, "E736", {"points": [v(-18.76, 37.1) * mm, v(-21.91, 35.7) * mm, v(-24.24, 35.64) * mm, v(-27.47, 36.9) * mm]});
            skFitSpline(sketch, "E737", {"points": [v(-27.47, 36.9) * mm, v(-30.7, 38.17) * mm, v(-32.32, 40.45) * mm, v(-32.32, 43.73) * mm]});
            skFitSpline(sketch, "E738", {"points": [v(-32.32, 43.73) * mm, v(-32.32, 45.82) * mm, v(-31.83, 46.82) * mm, v(-30.04, 48.39) * mm]});
            skFitSpline(sketch, "E739", {"points": [v(-30.04, 48.39) * mm, v(-27.24, 50.83) * mm, v(-25.46, 50.9) * mm, v(-23.08, 48.67) * mm]});
            skFitSpline(sketch, "E740", {"points": [v(-23.08, 48.67) * mm, v(-21.47, 47.17) * mm, v(-21.36, 46.76) * mm, v(-22.16, 45.4) * mm]});
            skFitSpline(sketch, "E741", {"points": [v(-22.16, 45.4) * mm, v(-23.07, 43.86) * mm, v(-23.08, 43.86) * mm, v(-23.48, 45.91) * mm]});
            skFitSpline(sketch, "E742", {"points": [v(-23.48, 45.91) * mm, v(-24.25, 49.87) * mm, v(-29.38, 48.4) * mm, v(-29.38, 44.22) * mm]});
            skFitSpline(sketch, "E743", {"points": [v(-29.38, 44.22) * mm, v(-29.38, 41.33) * mm, v(-27.28, 39.36) * mm, v(-23.72, 38.91) * mm]});
            skFitSpline(sketch, "E744", {"points": [v(-23.72, 38.91) * mm, v(-20.97, 38.57) * mm, v(-20.39, 38.76) * mm, v(-18.3, 40.7) * mm]});
            skFitSpline(sketch, "E745", {"points": [v(-18.3, 40.7) * mm, v(-16.14, 42.73) * mm, v(-16, 43.14) * mm, v(-16.32, 46.66) * mm]});
            skFitSpline(sketch, "E746", {"points": [v(-16.32, 46.66) * mm, v(-16.74, 51.45) * mm, v(-18.61, 53.87) * mm, v(-22.75, 54.99) * mm]});
            skFitSpline(sketch, "E747", {"points": [v(-22.75, 54.99) * mm, v(-31, 57.22) * mm, v(-38.2, 52.19) * mm, v(-38.18, 44.2) * mm]});
            skFitSpline(sketch, "E748", {"points": [v(-38.18, 44.2) * mm, v(-38.15, 38.04) * mm, v(-35.07, 33.16) * mm, v(-30.38, 31.84) * mm]});
            skFitSpline(sketch, "E749", {"points": [v(-30.38, 31.84) * mm, v(-27.3, 30.98) * mm, v(-20.18, 31.02) * mm, v(-18.1, 31.9) * mm]});
            skFitSpline(sketch, "E750", {"points": [v(19.41, 38.8) * mm, v(21.1, 41.98) * mm, v(20.9, 42.34) * mm, v(17.81, 41.8) * mm]});
            skFitSpline(sketch, "E751", {"points": [v(17.81, 41.8) * mm, v(16.3, 41.54) * mm, v(14.94, 41.21) * mm, v(14.8, 41.08) * mm]});
            skFitSpline(sketch, "E752", {"points": [v(14.8, 41.08) * mm, v(14.25, 40.58) * mm, v(16.55, 36.64) * mm, v(17.39, 36.64) * mm]});
            skFitSpline(sketch, "E753", {"points": [v(17.39, 36.64) * mm, v(17.86, 36.64) * mm, v(18.78, 37.61) * mm, v(19.41, 38.8) * mm]});
            skFitSpline(sketch, "E754", {"points": [v(69.78, 45.61) * mm, v(69.78, 48.76) * mm, v(69.53, 49.7) * mm, v(68.7, 49.7) * mm]});
            skFitSpline(sketch, "E755", {"points": [v(68.7, 49.7) * mm, v(68.1, 49.7) * mm, v(67.4, 48.94) * mm, v(67.16, 48.02) * mm]});
            skFitSpline(sketch, "E756", {"points": [v(67.16, 48.02) * mm, v(66.9, 47.1) * mm, v(66.08, 45.82) * mm, v(65.3, 45.17) * mm]});
            skFitSpline(sketch, "E757", {"points": [v(65.3, 45.17) * mm, v(62.86, 43.1) * mm, v(63.5, 41.61) * mm, v(66.84, 41.57) * mm]});
            skFitSpline(sketch, "E758", {"points": [v(-8.66, 44.18) * mm, v(-7.8, 44.93) * mm, v(-5.64, 46.07) * mm, v(-3.85, 46.7) * mm]});
            skFitSpline(sketch, "E759", {"points": [v(-3.85, 46.7) * mm, v(-0.26, 47.99) * mm, v(-0.3, 47.72) * mm, v(-2.72, 54.35) * mm]});
            skFitSpline(sketch, "E760", {"points": [v(-2.72, 54.35) * mm, v(-3.84, 57.44) * mm, v(-4.26, 57.92) * mm, v(-5.5, 57.56) * mm]});
            skFitSpline(sketch, "E761", {"points": [v(-5.5, 57.56) * mm, v(-6.32, 57.33) * mm, v(-8.71, 56.97) * mm, v(-10.83, 56.77) * mm]});
            skFitSpline(sketch, "E762", {"points": [v(-10.83, 56.77) * mm, v(-12.95, 56.56) * mm, v(-14.7, 56.22) * mm, v(-14.7, 56) * mm]});
            skFitSpline(sketch, "E763", {"points": [v(-14.7, 56) * mm, v(-14.7, 55.8) * mm, v(-13.97, 54.24) * mm, v(-13.1, 52.55) * mm]});
            skFitSpline(sketch, "E764", {"points": [v(-13.1, 52.55) * mm, v(-12.08, 50.57) * mm, v(-11.54, 48.28) * mm, v(-11.59, 46.15) * mm]});
            skFitSpline(sketch, "E765", {"points": [v(-11.59, 46.15) * mm, v(-11.68, 42.52) * mm, v(-11.05, 42.1) * mm, v(-8.66, 44.18) * mm]});
            skFitSpline(sketch, "E766", {"points": [v(59.21, 45.24) * mm, v(62.57, 47.63) * mm, v(63.9, 50.3) * mm, v(63.9, 54.6) * mm]});
            skFitSpline(sketch, "E767", {"points": [v(63.9, 54.6) * mm, v(63.9, 59.1) * mm, v(61.7, 63.52) * mm, v(58.25, 65.99) * mm]});
            skFitSpline(sketch, "E768", {"points": [v(58.25, 65.99) * mm, v(56.08, 67.54) * mm, v(54.99, 67.8) * mm, v(51, 67.77) * mm]});
            skFitSpline(sketch, "E769", {"points": [v(51, 67.77) * mm, v(45.82, 67.73) * mm, v(42.9, 66.84) * mm, v(38.77, 64.07) * mm]});
            skFitSpline(sketch, "E770", {"points": [v(38.77, 64.07) * mm, v(32.66, 59.98) * mm, v(30.89, 58.08) * mm, v(30.1, 54.76) * mm]});
            skFitSpline(sketch, "E771", {"points": [v(30.1, 54.76) * mm, v(29.67, 52.98) * mm, v(28.77, 50.66) * mm, v(28.1, 49.6) * mm]});
            skFitSpline(sketch, "E772", {"points": [v(28.1, 49.6) * mm, v(27.43, 48.54) * mm, v(27.03, 47.56) * mm, v(27.22, 47.43) * mm]});
            skFitSpline(sketch, "E773", {"points": [v(27.22, 47.43) * mm, v(27.4, 47.3) * mm, v(30.1, 47.32) * mm, v(33.23, 47.48) * mm]});
            skFitSpline(sketch, "E774", {"points": [v(38.48, 50.36) * mm, v(37.54, 55.84) * mm, v(42.34, 61.55) * mm, v(48.7, 62.52) * mm]});
            skFitSpline(sketch, "E775", {"points": [v(48.7, 62.52) * mm, v(55.97, 63.62) * mm, v(60.99, 55.1) * mm, v(55.88, 50.33) * mm]});
            skFitSpline(sketch, "E776", {"points": [v(55.88, 50.33) * mm, v(53.62, 48.21) * mm, v(52.18, 47.88) * mm, v(49.98, 48.99) * mm]});
            skFitSpline(sketch, "E777", {"points": [v(49.98, 48.99) * mm, v(48.31, 49.82) * mm, v(47.64, 51.4) * mm, v(48.28, 52.96) * mm]});
            skFitSpline(sketch, "E778", {"points": [v(48.28, 52.96) * mm, v(48.7, 53.96) * mm, v(48.85, 53.88) * mm, v(49.2, 52.44) * mm]});
            skFitSpline(sketch, "E779", {"points": [v(49.2, 52.44) * mm, v(49.7, 50.5) * mm, v(52.32, 49.77) * mm, v(54.03, 51.1) * mm]});
            skFitSpline(sketch, "E780", {"points": [v(54.03, 51.1) * mm, v(57.02, 53.42) * mm, v(53.61, 59.31) * mm, v(49.28, 59.31) * mm]});
            skFitSpline(sketch, "E781", {"points": [v(49.28, 59.31) * mm, v(42.55, 59.31) * mm, v(40, 53.63) * mm, v(43.73, 46.9) * mm]});
            skFitSpline(sketch, "E782", {"points": [v(43.73, 46.9) * mm, v(46.12, 42.56) * mm, v(54.24, 41.7) * mm, v(59.21, 45.24) * mm]});
            skFitSpline(sketch, "E783", {"points": [v(18.42, 47.17) * mm, v(22.54, 49.2) * mm, v(25.7, 54.45) * mm, v(25.7, 59.26) * mm]});
            skFitSpline(sketch, "E784", {"points": [v(25.7, 59.26) * mm, v(25.7, 63.04) * mm, v(22.9, 67.73) * mm, v(19, 70.5) * mm]});
            skFitSpline(sketch, "E785", {"points": [v(19, 70.5) * mm, v(16.76, 72.08) * mm, v(7.97, 75.8) * mm, v(6.48, 75.8) * mm]});
            skFitSpline(sketch, "E786", {"points": [v(6.48, 75.8) * mm, v(6.15, 75.8) * mm, v(5.88, 74.26) * mm, v(5.88, 72.37) * mm]});
            skFitSpline(sketch, "E787", {"points": [v(5.88, 72.37) * mm, v(5.88, 68.94) * mm, v(5.88, 68.93) * mm, v(8.3, 68.93) * mm]});
            skFitSpline(sketch, "E788", {"points": [v(8.3, 68.93) * mm, v(13.34, 68.93) * mm, v(19.83, 62.93) * mm, v(19.83, 58.28) * mm]});
            skFitSpline(sketch, "E789", {"points": [v(19.83, 58.28) * mm, v(19.83, 56.01) * mm, v(14.9, 51.07) * mm, v(12.63, 51.07) * mm]});
            skFitSpline(sketch, "E790", {"points": [v(12.63, 51.07) * mm, v(10.46, 51.07) * mm, v(6.61, 54.34) * mm, v(6.61, 56.17) * mm]});
            skFitSpline(sketch, "E791", {"points": [v(6.61, 56.17) * mm, v(6.61, 57.03) * mm, v(7.27, 58.29) * mm, v(8.08, 58.97) * mm]});
            skFitSpline(sketch, "E792", {"points": [v(8.08, 58.97) * mm, v(9.72, 60.36) * mm, v(9.99, 59.95) * mm, v(8.7, 58.02) * mm]});
            skFitSpline(sketch, "E793", {"points": [v(8.7, 58.02) * mm, v(7.04, 55.54) * mm, v(9.35, 53.27) * mm, v(12.73, 54.07) * mm]});
            skFitSpline(sketch, "E794", {"points": [v(12.73, 54.07) * mm, v(16.48, 54.95) * mm, v(17.23, 60.48) * mm, v(14.01, 63.49) * mm]});
            skFitSpline(sketch, "E795", {"points": [v(14.01, 63.49) * mm, v(10.78, 66.51) * mm, v(7.29, 66.3) * mm, v(3.59, 62.83) * mm]});
            skFitSpline(sketch, "E796", {"points": [v(3.59, 62.83) * mm, v(1, 60.42) * mm, v(0.73, 59.82) * mm, v(0.73, 56.61) * mm]});
            skFitSpline(sketch, "E797", {"points": [v(0.73, 56.61) * mm, v(0.73, 52.47) * mm, v(2.06, 49.7) * mm, v(4.86, 47.99) * mm]});
            skFitSpline(sketch, "E798", {"points": [v(4.86, 47.99) * mm, v(9.38, 45.21) * mm, v(13.92, 44.94) * mm, v(18.42, 47.17) * mm]});
            skFitSpline(sketch, "E799", {"points": [v(-40.95, 51) * mm, v(-39.84, 53.2) * mm, v(-38.93, 55.16) * mm, v(-38.93, 55.36) * mm]});
            skFitSpline(sketch, "E800", {"points": [v(-38.93, 55.36) * mm, v(-38.93, 55.56) * mm, v(-40.6, 55.72) * mm, v(-42.62, 55.72) * mm]});
            skFitSpline(sketch, "E801", {"points": [v(-42.62, 55.72) * mm, v(-46.67, 55.72) * mm, v(-50.53, 57.62) * mm, v(-54.12, 61.39) * mm]});
            skFitSpline(sketch, "E802", {"points": [v(-54.12, 61.39) * mm, v(-56.52, 63.91) * mm, v(-57.4, 63.95) * mm, v(-58.58, 61.58) * mm]});
            skFitSpline(sketch, "E803", {"points": [v(-58.58, 61.58) * mm, v(-59.87, 58.98) * mm, v(-59.79, 58.8) * mm, v(-57.1, 58.25) * mm]});
            skFitSpline(sketch, "E804", {"points": [v(-57.1, 58.25) * mm, v(-53.25, 57.46) * mm, v(-48.59, 54) * mm, v(-46.43, 50.34) * mm]});
            skFitSpline(sketch, "E805", {"points": [v(-46.43, 50.34) * mm, v(-45.33, 48.48) * mm, v(-44.1, 46.97) * mm, v(-43.7, 46.99) * mm]});
            skFitSpline(sketch, "E806", {"points": [v(-43.7, 46.99) * mm, v(-43.3, 47) * mm, v(-42.06, 48.8) * mm, v(-40.95, 51) * mm]});
            skFitSpline(sketch, "E807", {"points": [v(-66.33, 58.6) * mm, v(-63.23, 60.36) * mm, v(-61.8, 62.51) * mm, v(-61.26, 66.25) * mm]});
            skFitSpline(sketch, "E808", {"points": [v(-61.26, 66.25) * mm, v(-60.62, 70.59) * mm, v(-62.35, 74.18) * mm, v(-65.69, 75.49) * mm]});
            skFitSpline(sketch, "E809", {"points": [v(-65.69, 75.49) * mm, v(-69.69, 77.05) * mm, v(-70.51, 76.82) * mm, v(-70.51, 74.17) * mm]});
            skFitSpline(sketch, "E810", {"points": [v(-70.51, 74.17) * mm, v(-70.51, 72.44) * mm, v(-70.04, 71.55) * mm, v(-68.68, 70.71) * mm]});
            skFitSpline(sketch, "E811", {"points": [v(-68.68, 70.71) * mm, v(-66.2, 69.2) * mm, v(-66.2, 66.03) * mm, v(-68.68, 63.72) * mm]});
            skFitSpline(sketch, "E812", {"points": [v(-68.68, 63.72) * mm, v(-69.93, 62.55) * mm, v(-70.51, 61.24) * mm, v(-70.51, 59.63) * mm]});
            skFitSpline(sketch, "E813", {"points": [v(-70.51, 59.63) * mm, v(-70.51, 56.88) * mm, v(-69.7, 56.68) * mm, v(-66.33, 58.6) * mm]});
            skFitSpline(sketch, "E814", {"points": [v(-22.77, 60.12) * mm, v(-22.77, 61.14) * mm, v(-24.97, 63.44) * mm, v(-25.95, 63.44) * mm]});
            skFitSpline(sketch, "E815", {"points": [v(-25.95, 63.44) * mm, v(-27.07, 63.44) * mm, v(-29.38, 61.29) * mm, v(-29.38, 60.24) * mm]});
            skFitSpline(sketch, "E816", {"points": [v(-29.38, 60.24) * mm, v(-29.38, 59.6) * mm, v(-28.35, 59.31) * mm, v(-26.07, 59.31) * mm]});
            skFitSpline(sketch, "E817", {"points": [v(-26.07, 59.31) * mm, v(-24.04, 59.31) * mm, v(-22.77, 59.62) * mm, v(-22.77, 60.12) * mm]});
            skFitSpline(sketch, "E818", {"points": [v(-35.98, 61.27) * mm, v(-32.94, 62.78) * mm, v(-30.11, 66.4) * mm, v(-30.11, 68.78) * mm]});
            skFitSpline(sketch, "E819", {"points": [v(-30.11, 68.78) * mm, v(-30.11, 74.1) * mm, v(-33.5, 78.55) * mm, v(-37.52, 78.55) * mm]});
            skFitSpline(sketch, "E820", {"points": [v(-37.52, 78.55) * mm, v(-43.53, 78.55) * mm, v(-47.17, 72.53) * mm, v(-43.34, 68.93) * mm]});
            skFitSpline(sketch, "E821", {"points": [v(-43.34, 68.93) * mm, v(-40.44, 66.23) * mm, v(-36.45, 68.04) * mm, v(-38.05, 71.33) * mm]});
            skFitSpline(sketch, "E822", {"points": [v(-38.05, 71.33) * mm, v(-38.73, 72.7) * mm, v(-38.68, 72.92) * mm, v(-37.79, 72.6) * mm]});
            skFitSpline(sketch, "E823", {"points": [v(-37.79, 72.6) * mm, v(-37.2, 72.4) * mm, v(-36.5, 71.43) * mm, v(-36.24, 70.46) * mm]});
            skFitSpline(sketch, "E824", {"points": [v(-36.24, 70.46) * mm, v(-35.87, 69.08) * mm, v(-36.2, 68.35) * mm, v(-37.76, 67.1) * mm]});
            skFitSpline(sketch, "E825", {"points": [v(-37.76, 67.1) * mm, v(-38.85, 66.22) * mm, v(-40.5, 65.5) * mm, v(-41.44, 65.5) * mm]});
            skFitSpline(sketch, "E826", {"points": [v(-41.44, 65.5) * mm, v(-45.66, 65.5) * mm, v(-49.45, 71.26) * mm, v(-47.75, 75.1) * mm]});
            skFitSpline(sketch, "E827", {"points": [v(-47.75, 75.1) * mm, v(-46.62, 77.66) * mm, v(-44.33, 79.61) * mm, v(-40.88, 80.96) * mm]});
            skFitSpline(sketch, "E828", {"points": [v(-40.88, 80.96) * mm, v(-38.57, 81.86) * mm, v(-37.6, 81.92) * mm, v(-35.38, 81.25) * mm]});
            skFitSpline(sketch, "E829", {"points": [v(-35.38, 81.25) * mm, v(-33.9, 80.81) * mm, v(-32.37, 80.18) * mm, v(-31.99, 79.85) * mm]});
            skFitSpline(sketch, "E830", {"points": [v(-31.99, 79.85) * mm, v(-30.26, 78.35) * mm, v(-28.89, 79.33) * mm, v(-27.68, 82.9) * mm]});
            skFitSpline(sketch, "E831", {"points": [v(-27.68, 82.9) * mm, v(-27, 84.93) * mm, v(-26.44, 86.74) * mm, v(-26.44, 86.93) * mm]});
            skFitSpline(sketch, "E832", {"points": [v(-26.44, 86.93) * mm, v(-26.44, 87.13) * mm, v(-28.78, 87.5) * mm, v(-31.64, 87.74) * mm]});
            skFitSpline(sketch, "E833", {"points": [v(-31.64, 87.74) * mm, v(-35.66, 88.1) * mm, v(-37.65, 87.92) * mm, v(-40.44, 87) * mm]});
            skFitSpline(sketch, "E834", {"points": [v(-40.44, 87) * mm, v(-45.16, 85.43) * mm, v(-51.51, 81.4) * mm, v(-52.67, 79.24) * mm]});
            skFitSpline(sketch, "E835", {"points": [v(-52.67, 79.24) * mm, v(-53.8, 77.14) * mm, v(-53.9, 69.73) * mm, v(-52.84, 67.09) * mm]});
            skFitSpline(sketch, "E836", {"points": [v(-52.84, 67.09) * mm, v(-50.37, 61.01) * mm, v(-42.19, 58.19) * mm, v(-35.98, 61.27) * mm]});
            skFitSpline(sketch, "E837", {"points": [v(-7.01, 62.14) * mm, v(-2.76, 63.24) * mm, v(0.49, 66.59) * mm, v(1.12, 70.52) * mm]});
            skFitSpline(sketch, "E838", {"points": [v(1.12, 70.52) * mm, v(1.86, 75.16) * mm, v(0.98, 78.47) * mm, v(-1.6, 80.73) * mm]});
            skFitSpline(sketch, "E839", {"points": [v(-1.6, 80.73) * mm, v(-3.53, 82.42) * mm, v(-4.41, 82.68) * mm, v(-8.21, 82.68) * mm]});
            skFitSpline(sketch, "E840", {"points": [v(-8.21, 82.68) * mm, v(-12.12, 82.68) * mm, v(-12.84, 82.45) * mm, v(-14.84, 80.58) * mm]});
            skFitSpline(sketch, "E841", {"points": [v(-14.84, 80.58) * mm, v(-16.82, 78.73) * mm, v(-17.03, 78.16) * mm, v(-16.66, 75.6) * mm]});
            skFitSpline(sketch, "E842", {"points": [v(-16.66, 75.6) * mm, v(-16.17, 72.18) * mm, v(-14.07, 70.3) * mm, v(-10.72, 70.3) * mm]});
            skFitSpline(sketch, "E843", {"points": [v(-10.72, 70.3) * mm, v(-7.83, 70.3) * mm, v(-6.61, 71.37) * mm, v(-6.61, 73.88) * mm]});
            skFitSpline(sketch, "E844", {"points": [v(-6.61, 73.88) * mm, v(-6.61, 75.58) * mm, v(-6.88, 75.8) * mm, v(-8.9, 75.8) * mm]});
            skFitSpline(sketch, "E845", {"points": [v(-8.9, 75.8) * mm, v(-10.86, 75.8) * mm, v(-11.06, 75.96) * mm, v(-10.28, 76.84) * mm]});
            skFitSpline(sketch, "E846", {"points": [v(-10.28, 76.84) * mm, v(-8.96, 78.32) * mm, v(-6.87, 78.1) * mm, v(-5.55, 76.34) * mm]});
            skFitSpline(sketch, "E847", {"points": [v(-5.55, 76.34) * mm, v(-2.76, 72.61) * mm, v(-5.46, 67.76) * mm, v(-10.69, 67.1) * mm]});
            skFitSpline(sketch, "E848", {"points": [v(-10.69, 67.1) * mm, v(-13.17, 66.79) * mm, v(-14.04, 67.03) * mm, v(-16, 68.57) * mm]});
            skFitSpline(sketch, "E849", {"points": [v(-16, 68.57) * mm, v(-18.65, 70.66) * mm, v(-20.18, 74.86) * mm, v(-19.51, 78.2) * mm]});
            skFitSpline(sketch, "E850", {"points": [v(-19.51, 78.2) * mm, v(-19.02, 80.7) * mm, v(-14.64, 85.82) * mm, v(-12.47, 86.46) * mm]});
            skFitSpline(sketch, "E851", {"points": [v(-12.47, 86.46) * mm, v(-11.67, 86.7) * mm, v(-11.02, 87.26) * mm, v(-11.02, 87.7) * mm]});
            skFitSpline(sketch, "E852", {"points": [v(-11.02, 87.7) * mm, v(-11.01, 88.95) * mm, v(-14.23, 94.36) * mm, v(-14.97, 94.36) * mm]});
            skFitSpline(sketch, "E853", {"points": [v(-14.97, 94.36) * mm, v(-15.33, 94.36) * mm, v(-16.34, 93.66) * mm, v(-17.22, 92.81) * mm]});
            skFitSpline(sketch, "E854", {"points": [v(-17.22, 92.81) * mm, v(-18.1, 91.96) * mm, v(-19.66, 90.6) * mm, v(-20.7, 89.8) * mm]});
            skFitSpline(sketch, "E855", {"points": [v(-20.7, 89.8) * mm, v(-22.12, 88.7) * mm, v(-22.9, 87) * mm, v(-23.86, 82.95) * mm]});
            skFitSpline(sketch, "E856", {"points": [v(-23.86, 82.95) * mm, v(-26.52, 71.77) * mm, v(-23.28, 63.82) * mm, v(-15.33, 62.06) * mm]});
            skFitSpline(sketch, "E857", {"points": [v(-15.33, 62.06) * mm, v(-11.76, 61.27) * mm, v(-10.28, 61.29) * mm, v(-7.01, 62.14) * mm]});
            skFitSpline(sketch, "E858", {"points": [v(69.78, 64.47) * mm, v(69.78, 67.69) * mm, v(68.7, 68.42) * mm, v(66.15, 66.9) * mm]});
            skFitSpline(sketch, "E859", {"points": [v(66.15, 66.9) * mm, v(65.24, 66.37) * mm, v(65.29, 65.93) * mm, v(66.5, 63.83) * mm]});
            skFitSpline(sketch, "E860", {"points": [v(66.5, 63.83) * mm, v(68.47, 60.4) * mm, v(69.78, 60.65) * mm, v(69.78, 64.47) * mm]});
            skFitSpline(sketch, "E861", {"points": [v(33.93, 65.25) * mm, v(37.67, 67.67) * mm, v(37.7, 69.26) * mm, v(33.97, 68.69) * mm]});
            skFitSpline(sketch, "E862", {"points": [v(33.97, 68.69) * mm, v(32.46, 68.45) * mm, v(30.47, 68.26) * mm, v(29.56, 68.25) * mm]});
            skFitSpline(sketch, "E863", {"points": [v(29.56, 68.25) * mm, v(27.76, 68.25) * mm, v(27.43, 66.94) * mm, v(28.67, 64.77) * mm]});
            skFitSpline(sketch, "E864", {"points": [v(28.67, 64.77) * mm, v(29.68, 63) * mm, v(30.6, 63.09) * mm, v(33.93, 65.25) * mm]});
            skFitSpline(sketch, "E865", {"points": [v(-68.3, 67.9) * mm, v(-68.3, 68.97) * mm, v(-68.73, 69.62) * mm, v(-69.41, 69.62) * mm]});
            skFitSpline(sketch, "E866", {"points": [v(-69.41, 69.62) * mm, v(-70.1, 69.62) * mm, v(-70.51, 68.97) * mm, v(-70.51, 67.9) * mm]});
            skFitSpline(sketch, "E867", {"points": [v(-70.51, 67.9) * mm, v(-70.51, 66.83) * mm, v(-70.1, 66.18) * mm, v(-69.41, 66.18) * mm]});
            skFitSpline(sketch, "E868", {"points": [v(-69.41, 66.18) * mm, v(-68.73, 66.18) * mm, v(-68.3, 66.83) * mm, v(-68.3, 67.9) * mm]});
            skFitSpline(sketch, "E869", {"points": [v(68.13, 70.74) * mm, v(69.52, 71.1) * mm, v(69.78, 71.63) * mm, v(69.78, 74.16) * mm]});
            skFitSpline(sketch, "E870", {"points": [v(65.5, 76.74) * mm, v(62.3, 76.43) * mm, v(60.66, 76.6) * mm, v(58.91, 77.45) * mm]});
            skFitSpline(sketch, "E871", {"points": [v(58.91, 77.45) * mm, v(56.44, 78.65) * mm, v(54.35, 81.67) * mm, v(54.35, 84.05) * mm]});
            skFitSpline(sketch, "E872", {"points": [v(54.35, 84.05) * mm, v(54.35, 88.23) * mm, v(58.87, 91.63) * mm, v(62.64, 90.3) * mm]});
            skFitSpline(sketch, "E873", {"points": [v(62.64, 90.3) * mm, v(64.73, 89.55) * mm, v(66.08, 86.5) * mm, v(64.83, 85.33) * mm]});
            skFitSpline(sketch, "E874", {"points": [v(64.83, 85.33) * mm, v(64.35, 84.88) * mm, v(63.95, 85.37) * mm, v(63.65, 86.76) * mm]});
            skFitSpline(sketch, "E875", {"points": [v(63.65, 86.76) * mm, v(63.3, 88.42) * mm, v(62.82, 88.86) * mm, v(61.4, 88.86) * mm]});
            skFitSpline(sketch, "E876", {"points": [v(61.4, 88.86) * mm, v(59.26, 88.86) * mm, v(57.3, 87.21) * mm, v(57.3, 85.42) * mm]});
            skFitSpline(sketch, "E877", {"points": [v(57.3, 85.42) * mm, v(57.3, 81.37) * mm, v(61.03, 78.67) * mm, v(65.49, 79.5) * mm]});
            skFitSpline(sketch, "E878", {"points": [v(65.49, 79.5) * mm, v(69.35, 80.23) * mm, v(69.78, 80.96) * mm, v(69.78, 86.89) * mm]});
            skFitSpline(sketch, "E879", {"points": [v(69.78, 86.89) * mm, v(69.78, 93.14) * mm, v(68.9, 94.48) * mm, v(63.93, 95.73) * mm]});
            skFitSpline(sketch, "E880", {"points": [v(63.93, 95.73) * mm, v(58.31, 97.14) * mm, v(52.27, 94.8) * mm, v(49.71, 90.22) * mm]});
            skFitSpline(sketch, "E881", {"points": [v(49.71, 90.22) * mm, v(48.68, 88.37) * mm, v(48.47, 86.87) * mm, v(48.77, 83.56) * mm]});
            skFitSpline(sketch, "E882", {"points": [v(48.77, 83.56) * mm, v(49.2, 78.82) * mm, v(50.34, 76.28) * mm, v(53.16, 73.81) * mm]});
            skFitSpline(sketch, "E883", {"points": [v(53.16, 73.81) * mm, v(56.09, 71.25) * mm, v(63.83, 69.66) * mm, v(68.13, 70.74) * mm]});
            skFitSpline(sketch, "E884", {"points": [v(46.1, 71.43) * mm, v(48.1, 71.93) * mm, v(48.37, 74.43) * mm, v(46.42, 74.43) * mm]});
            skFitSpline(sketch, "E885", {"points": [v(46.42, 74.43) * mm, v(44.87, 74.43) * mm, v(43.34, 73.16) * mm, v(43.34, 71.89) * mm]});
            skFitSpline(sketch, "E886", {"points": [v(43.34, 71.89) * mm, v(43.34, 70.9) * mm, v(43.7, 70.83) * mm, v(46.1, 71.43) * mm]});
            skFitSpline(sketch, "E887", {"points": [v(39.33, 73.76) * mm, v(44.32, 76.02) * mm, v(45.02, 77.1) * mm, v(43.94, 80.87) * mm]});
            skFitSpline(sketch, "E888", {"points": [v(43.94, 80.87) * mm, v(43.44, 82.62) * mm, v(42.76, 84.05) * mm, v(42.42, 84.05) * mm]});
            skFitSpline(sketch, "E889", {"points": [v(42.42, 84.05) * mm, v(42.08, 84.05) * mm, v(40.58, 82.85) * mm, v(39.08, 81.39) * mm]});
            skFitSpline(sketch, "E890", {"points": [v(39.08, 81.39) * mm, v(34.1, 76.5) * mm, v(26.3, 76.86) * mm, v(23.44, 82.1) * mm]});
            skFitSpline(sketch, "E891", {"points": [v(23.44, 82.1) * mm, v(21.7, 85.31) * mm, v(22.04, 88) * mm, v(24.46, 90.07) * mm]});
            skFitSpline(sketch, "E892", {"points": [v(24.46, 90.07) * mm, v(27.13, 92.36) * mm, v(29, 92.54) * mm, v(31.24, 90.74) * mm]});
            skFitSpline(sketch, "E893", {"points": [v(31.24, 90.74) * mm, v(32.86, 89.43) * mm, v(33.13, 88.8) * mm, v(32.65, 87.45) * mm]});
            skFitSpline(sketch, "E894", {"points": [v(31.62, 87.42) * mm, v(30.48, 91.74) * mm, v(26.22, 90.9) * mm, v(25.85, 86.28) * mm]});
            skFitSpline(sketch, "E895", {"points": [v(25.85, 86.28) * mm, v(25.67, 84.02) * mm, v(25.95, 83.29) * mm, v(27.3, 82.4) * mm]});
            skFitSpline(sketch, "E896", {"points": [v(27.3, 82.4) * mm, v(29.4, 81.02) * mm, v(34.43, 80.98) * mm, v(36.48, 82.32) * mm]});
            skFitSpline(sketch, "E897", {"points": [v(36.48, 82.32) * mm, v(39.93, 84.58) * mm, v(39.17, 92.2) * mm, v(35.19, 95.34) * mm]});
            skFitSpline(sketch, "E898", {"points": [v(35.19, 95.34) * mm, v(33.34, 96.8) * mm, v(32.18, 97.1) * mm, v(28.7, 97.1) * mm]});
            skFitSpline(sketch, "E899", {"points": [v(28.7, 97.1) * mm, v(24.03, 97.1) * mm, v(20.86, 95.61) * mm, v(18.08, 92.1) * mm]});
            skFitSpline(sketch, "E900", {"points": [v(18.08, 92.1) * mm, v(14.36, 87.4) * mm, v(17.27, 77.06) * mm, v(23.18, 73.93) * mm]});
            skFitSpline(sketch, "E901", {"points": [v(23.18, 73.93) * mm, v(27.1, 71.85) * mm, v(34.93, 71.77) * mm, v(39.33, 73.76) * mm]});
            skFitSpline(sketch, "E902", {"points": [v(-57.65, 78.6) * mm, v(-57.02, 81.28) * mm, v(-57.29, 81.5) * mm, v(-60.52, 80.93) * mm]});
            skFitSpline(sketch, "E903", {"points": [v(-60.52, 80.93) * mm, v(-63.58, 80.4) * mm, v(-63.83, 79.63) * mm, v(-61.51, 77.83) * mm]});
            skFitSpline(sketch, "E904", {"points": [v(-61.51, 77.83) * mm, v(-59.17, 76) * mm, v(-58.21, 76.19) * mm, v(-57.65, 78.6) * mm]});
            skFitSpline(sketch, "E905", {"points": [v(12.49, 80.96) * mm, v(12.49, 82.54) * mm, v(12.22, 82.68) * mm, v(9.18, 82.68) * mm]});
            skFitSpline(sketch, "E906", {"points": [v(9.18, 82.68) * mm, v(5.34, 82.68) * mm, v(4.6, 81.16) * mm, v(7.9, 80.04) * mm]});
            skFitSpline(sketch, "E907", {"points": [v(7.9, 80.04) * mm, v(11.38, 78.85) * mm, v(12.49, 79.07) * mm, v(12.49, 80.96) * mm]});
            skFitSpline(sketch, "E908", {"points": [v(-58.9, 85.7) * mm, v(-54.33, 87.94) * mm, v(-51.41, 92.69) * mm, v(-51.42, 97.93) * mm]});
            skFitSpline(sketch, "E909", {"points": [v(-51.42, 97.93) * mm, v(-51.42, 104.62) * mm, v(-55.87, 108.78) * mm, v(-63, 108.79) * mm]});
            skFitSpline(sketch, "E910", {"points": [v(-63, 108.79) * mm, v(-65.35, 108.8) * mm, v(-67.61, 108.35) * mm, v(-68.7, 107.68) * mm]});
            skFitSpline(sketch, "E911", {"points": [v(-68.7, 107.68) * mm, v(-70.38, 106.65) * mm, v(-70.51, 106.17) * mm, v(-70.51, 100.95) * mm]});
            skFitSpline(sketch, "E912", {"points": [v(-70.51, 100.95) * mm, v(-70.51, 97.49) * mm, v(-70.17, 95) * mm, v(-69.63, 94.5) * mm]});
            skFitSpline(sketch, "E913", {"points": [v(-69.63, 94.5) * mm, v(-68.38, 93.33) * mm, v(-63.8, 93.47) * mm, v(-61.86, 94.74) * mm]});
            skFitSpline(sketch, "E914", {"points": [v(-61.86, 94.74) * mm, v(-60.04, 95.94) * mm, v(-59.6, 99.68) * mm, v(-61.11, 101.1) * mm]});
            skFitSpline(sketch, "E915", {"points": [v(-61.11, 101.1) * mm, v(-62.34, 102.24) * mm, v(-64.6, 102.13) * mm, v(-65.1, 100.89) * mm]});
            skFitSpline(sketch, "E916", {"points": [v(-65.1, 100.89) * mm, v(-65.34, 100.32) * mm, v(-65.82, 99.86) * mm, v(-66.18, 99.86) * mm]});
            skFitSpline(sketch, "E917", {"points": [v(-66.18, 99.86) * mm, v(-67.3, 99.86) * mm, v(-66.9, 101.17) * mm, v(-65.33, 102.64) * mm]});
            skFitSpline(sketch, "E918", {"points": [v(-65.33, 102.64) * mm, v(-63.52, 104.34) * mm, v(-61.34, 103.95) * mm, v(-58.94, 101.48) * mm]});
            skFitSpline(sketch, "E919", {"points": [v(-58.94, 101.48) * mm, v(-56.37, 98.83) * mm, v(-56.71, 95.45) * mm, v(-59.87, 92.5) * mm]});
            skFitSpline(sketch, "E920", {"points": [v(-59.87, 92.5) * mm, v(-62.53, 90.01) * mm, v(-63.98, 89.81) * mm, v(-68.86, 91.28) * mm]});
            skFitSpline(sketch, "E921", {"points": [v(-68.86, 91.28) * mm, v(-70.4, 91.74) * mm, v(-70.51, 91.58) * mm, v(-70.51, 88.66) * mm]});
            skFitSpline(sketch, "E922", {"points": [v(-70.51, 88.66) * mm, v(-70.51, 86.8) * mm, v(-70.14, 85.4) * mm, v(-69.6, 85.2) * mm]});
            skFitSpline(sketch, "E923", {"points": [v(-69.6, 85.2) * mm, v(-67.64, 84.46) * mm, v(-60.8, 84.79) * mm, v(-58.9, 85.7) * mm]});
            skFitSpline(sketch, "E924", {"points": [v(11.75, 87.27) * mm, v(11.75, 87.9) * mm, v(12.15, 89.44) * mm, v(12.63, 90.69) * mm]});
            skFitSpline(sketch, "E925", {"points": [v(12.63, 90.69) * mm, v(13.1, 91.93) * mm, v(13.3, 93.15) * mm, v(13.03, 93.4) * mm]});
            skFitSpline(sketch, "E926", {"points": [v(13.03, 93.4) * mm, v(12.77, 93.63) * mm, v(10.88, 93.05) * mm, v(8.83, 92.09) * mm]});
            skFitSpline(sketch, "E927", {"points": [v(8.83, 92.09) * mm, v(5.77, 90.67) * mm, v(4.66, 90.46) * mm, v(2.73, 90.98) * mm]});
            skFitSpline(sketch, "E928", {"points": [v(2.73, 90.98) * mm, v(-0.57, 91.86) * mm, v(-3.09, 93.76) * mm, v(-4.14, 96.17) * mm]});
            skFitSpline(sketch, "E929", {"points": [v(-4.14, 96.17) * mm, v(-4.89, 97.9) * mm, v(-4.82, 98.66) * mm, v(-3.73, 100.94) * mm]});
            skFitSpline(sketch, "E930", {"points": [v(-3.73, 100.94) * mm, v(-2.03, 104.5) * mm, v(0.9, 105.87) * mm, v(3.43, 104.3) * mm]});
            skFitSpline(sketch, "E931", {"points": [v(3.43, 104.3) * mm, v(5.59, 102.99) * mm, v(6.23, 101.65) * mm, v(5.47, 100.03) * mm]});
            skFitSpline(sketch, "E932", {"points": [v(5.47, 100.03) * mm, v(5.02, 99.05) * mm, v(4.83, 99.21) * mm, v(4.47, 100.89) * mm]});
            skFitSpline(sketch, "E933", {"points": [v(4.47, 100.89) * mm, v(3.57, 105.1) * mm, v(-1.47, 103.3) * mm, v(-1.47, 98.78) * mm]});
            skFitSpline(sketch, "E934", {"points": [v(-1.47, 98.78) * mm, v(-1.47, 95.4) * mm, v(0.65, 93.67) * mm, v(4.79, 93.67) * mm]});
            skFitSpline(sketch, "E935", {"points": [v(4.79, 93.67) * mm, v(7.74, 93.67) * mm, v(8.26, 93.92) * mm, v(9.56, 95.9) * mm]});
            skFitSpline(sketch, "E936", {"points": [v(9.56, 95.9) * mm, v(11.35, 98.66) * mm, v(11.52, 104.38) * mm, v(9.87, 106.58) * mm]});
            skFitSpline(sketch, "E937", {"points": [v(9.87, 106.58) * mm, v(6.3, 111.36) * mm, v(-3.17, 111.3) * mm, v(-7.45, 106.47) * mm]});
            skFitSpline(sketch, "E938", {"points": [v(-7.45, 106.47) * mm, v(-8.16, 105.67) * mm, v(-9.12, 103.38) * mm, v(-9.57, 101.4) * mm]});
            skFitSpline(sketch, "E939", {"points": [v(-9.57, 101.4) * mm, v(-11.02, 95.01) * mm, v(-9.07, 90.42) * mm, v(-3.84, 87.87) * mm]});
            skFitSpline(sketch, "E940", {"points": [v(-3.84, 87.87) * mm, v(-1, 86.48) * mm, v(0.73, 86.17) * mm, v(5.7, 86.15) * mm]});
            skFitSpline(sketch, "E941", {"points": [v(5.7, 86.15) * mm, v(10.89, 86.12) * mm, v(11.75, 86.28) * mm, v(11.75, 87.27) * mm]});
            skFitSpline(sketch, "E942", {"points": [v(-44.47, 90.35) * mm, v(-42.42, 91.22) * mm, v(-42.12, 92.68) * mm, v(-43.62, 94.53) * mm]});
            skFitSpline(sketch, "E943", {"points": [v(-43.62, 94.53) * mm, v(-45.13, 96.39) * mm, v(-46.13, 95.97) * mm, v(-46.97, 93.16) * mm]});
            skFitSpline(sketch, "E944", {"points": [v(-46.97, 93.16) * mm, v(-48.17, 89.1) * mm, v(-47.96, 88.86) * mm, v(-44.47, 90.35) * mm]});
            skFitSpline(sketch, "E945", {"points": [v(45.54, 92.63) * mm, v(45.54, 93.66) * mm, v(51.09, 99.17) * mm, v(52.12, 99.17) * mm]});
            skFitSpline(sketch, "E946", {"points": [v(52.12, 99.17) * mm, v(53.52, 99.17) * mm, v(54.5, 104.52) * mm, v(54.25, 110.68) * mm]});
            skFitSpline(sketch, "E947", {"points": [v(54.25, 110.68) * mm, v(53.95, 117.67) * mm, v(52.97, 119.33) * mm, v(47.59, 121.92) * mm]});
            skFitSpline(sketch, "E948", {"points": [v(47.59, 121.92) * mm, v(43.6, 123.82) * mm, v(36.48, 123.71) * mm, v(33.32, 121.69) * mm]});
            skFitSpline(sketch, "E949", {"points": [v(33.32, 121.69) * mm, v(27.8, 118.15) * mm, v(25.97, 109.68) * mm, v(29.8, 105.42) * mm]});
            skFitSpline(sketch, "E950", {"points": [v(29.8, 105.42) * mm, v(33.13, 101.72) * mm, v(40.84, 100.96) * mm, v(44.11, 104.02) * mm]});
            skFitSpline(sketch, "E951", {"points": [v(44.11, 104.02) * mm, v(45.14, 104.98) * mm, v(45.54, 106.3) * mm, v(45.54, 108.74) * mm]});
            skFitSpline(sketch, "E952", {"points": [v(45.54, 108.74) * mm, v(45.54, 111.58) * mm, v(45.23, 112.36) * mm, v(43.6, 113.55) * mm]});
            skFitSpline(sketch, "E953", {"points": [v(43.6, 113.55) * mm, v(39.99, 116.21) * mm, v(35.66, 114.83) * mm, v(36.11, 111.16) * mm]});
            skFitSpline(sketch, "E954", {"points": [v(36.11, 111.16) * mm, v(36.3, 109.67) * mm, v(36.8, 109.08) * mm, v(38.02, 108.91) * mm]});
            skFitSpline(sketch, "E955", {"points": [v(38.02, 108.91) * mm, v(38.94, 108.8) * mm, v(39.5, 108.4) * mm, v(39.26, 108.06) * mm]});
            skFitSpline(sketch, "E956", {"points": [v(39.26, 108.06) * mm, v(38, 106.13) * mm, v(33.79, 109.03) * mm, v(33.79, 111.83) * mm]});
            skFitSpline(sketch, "E957", {"points": [v(33.79, 111.83) * mm, v(33.79, 112.75) * mm, v(34.64, 114.45) * mm, v(35.69, 115.61) * mm]});
            skFitSpline(sketch, "E958", {"points": [v(35.69, 115.61) * mm, v(37.25, 117.35) * mm, v(38.13, 117.73) * mm, v(40.67, 117.73) * mm]});
            skFitSpline(sketch, "E959", {"points": [v(40.67, 117.73) * mm, v(47.38, 117.73) * mm, v(51.08, 111.56) * mm, v(48.22, 105.15) * mm]});
            skFitSpline(sketch, "E960", {"points": [v(48.22, 105.15) * mm, v(47.24, 102.95) * mm, v(42.47, 98.48) * mm, v(41.1, 98.48) * mm]});
            skFitSpline(sketch, "E961", {"points": [v(41.1, 98.48) * mm, v(40.02, 98.48) * mm, v(40.25, 97.13) * mm, v(41.91, 93.93) * mm]});
            skFitSpline(sketch, "E962", {"points": [v(41.91, 93.93) * mm, v(42.93, 91.96) * mm, v(43.77, 91.12) * mm, v(44.48, 91.38) * mm]});
            skFitSpline(sketch, "E963", {"points": [v(44.48, 91.38) * mm, v(45.06, 91.59) * mm, v(45.54, 92.15) * mm, v(45.54, 92.63) * mm]});
            skFitSpline(sketch, "E964", {"points": [v(-20.99, 93.93) * mm, v(-15.86, 97.6) * mm, v(-14.5, 100.03) * mm, v(-13.91, 106.6) * mm]});
            skFitSpline(sketch, "E965", {"points": [v(-13.91, 106.6) * mm, v(-13.62, 109.88) * mm, v(-13.6, 112.8) * mm, v(-13.87, 113.07) * mm]});
            skFitSpline(sketch, "E966", {"points": [v(-13.87, 113.07) * mm, v(-14.14, 113.34) * mm, v(-15.58, 113.38) * mm, v(-17.07, 113.15) * mm]});
            skFitSpline(sketch, "E967", {"points": [v(-19.68, 109.18) * mm, v(-19.52, 103.45) * mm, v(-24.42, 97.1) * mm, v(-29.01, 97.1) * mm]});
            skFitSpline(sketch, "E968", {"points": [v(-29.01, 97.1) * mm, v(-31.2, 97.1) * mm, v(-35.03, 99.76) * mm, v(-36, 101.93) * mm]});
            skFitSpline(sketch, "E969", {"points": [v(-36, 101.93) * mm, v(-37.08, 104.38) * mm, v(-35.94, 107.71) * mm, v(-33.62, 108.88) * mm]});
            skFitSpline(sketch, "E970", {"points": [v(-33.62, 108.88) * mm, v(-31.78, 109.8) * mm, v(-28.65, 109.08) * mm, v(-28.65, 107.74) * mm]});
            skFitSpline(sketch, "E971", {"points": [v(-28.65, 107.74) * mm, v(-28.65, 106.91) * mm, v(-28.9, 106.87) * mm, v(-30.02, 107.52) * mm]});
            skFitSpline(sketch, "E972", {"points": [v(-30.02, 107.52) * mm, v(-32.34, 108.88) * mm, v(-33.79, 107.79) * mm, v(-33.79, 104.67) * mm]});
            skFitSpline(sketch, "E973", {"points": [v(-33.79, 104.67) * mm, v(-33.79, 102.31) * mm, v(-33.5, 101.78) * mm, v(-31.9, 101.22) * mm]});
            skFitSpline(sketch, "E974", {"points": [v(-31.9, 101.22) * mm, v(-28.82, 100.12) * mm, v(-27.18, 100.43) * mm, v(-24.92, 102.55) * mm]});
            skFitSpline(sketch, "E975", {"points": [v(-24.92, 102.55) * mm, v(-23.29, 104.08) * mm, v(-22.77, 105.2) * mm, v(-22.77, 107.21) * mm]});
            skFitSpline(sketch, "E976", {"points": [v(-22.77, 107.21) * mm, v(-22.77, 115.48) * mm, v(-35.51, 118.03) * mm, v(-40.24, 110.7) * mm]});
            skFitSpline(sketch, "E977", {"points": [v(-40.24, 110.7) * mm, v(-43.35, 105.87) * mm, v(-42.9, 99.25) * mm, v(-39.2, 95.64) * mm]});
            skFitSpline(sketch, "E978", {"points": [v(-39.2, 95.64) * mm, v(-34.86, 91.4) * mm, v(-25.73, 90.55) * mm, v(-20.99, 93.93) * mm]});
            skFitSpline(sketch, "E979", {"points": [v(21.23, 99.64) * mm, v(23.49, 100.65) * mm, v(25.47, 101.57) * mm, v(25.62, 101.67) * mm]});
            skFitSpline(sketch, "E980", {"points": [v(25.62, 101.67) * mm, v(25.77, 101.78) * mm, v(25.35, 102.96) * mm, v(24.68, 104.28) * mm]});
            skFitSpline(sketch, "E981", {"points": [v(24.68, 104.28) * mm, v(24, 105.61) * mm, v(23.42, 108.1) * mm, v(23.38, 109.8) * mm]});
            skFitSpline(sketch, "E982", {"points": [v(23.38, 109.8) * mm, v(23.31, 113.27) * mm, v(22.89, 113.46) * mm, v(18.84, 111.88) * mm]});
            skFitSpline(sketch, "E983", {"points": [v(18.84, 111.88) * mm, v(17.4, 111.32) * mm, v(15.37, 110.85) * mm, v(14.35, 110.85) * mm]});
            skFitSpline(sketch, "E984", {"points": [v(14.35, 110.85) * mm, v(12.1, 110.85) * mm, v(12, 109.94) * mm, v(13.96, 107.6) * mm]});
            skFitSpline(sketch, "E985", {"points": [v(13.96, 107.6) * mm, v(15.05, 106.3) * mm, v(15.42, 104.82) * mm, v(15.42, 101.83) * mm]});
            skFitSpline(sketch, "E986", {"points": [v(15.42, 101.83) * mm, v(15.42, 99.25) * mm, v(15.73, 97.8) * mm, v(16.27, 97.8) * mm]});
            skFitSpline(sketch, "E987", {"points": [v(16.27, 97.8) * mm, v(16.73, 97.8) * mm, v(18.97, 98.62) * mm, v(21.23, 99.64) * mm]});
            skFitSpline(sketch, "E988", {"points": [v(62.4, 101.4) * mm, v(62.38, 102.56) * mm, v(59.83, 105.36) * mm, v(58.8, 105.36) * mm]});
            skFitSpline(sketch, "E989", {"points": [v(58.8, 105.36) * mm, v(58.04, 105.36) * mm, v(56.56, 102.6) * mm, v(56.56, 101.19) * mm]});
            skFitSpline(sketch, "E990", {"points": [v(56.56, 101.19) * mm, v(56.56, 100.83) * mm, v(57.88, 100.54) * mm, v(59.5, 100.54) * mm]});
            skFitSpline(sketch, "E991", {"points": [v(59.5, 100.54) * mm, v(61.37, 100.54) * mm, v(62.42, 100.86) * mm, v(62.4, 101.4) * mm]});
            skFitSpline(sketch, "E992", {"points": [v(69.78, 104.84) * mm, v(69.78, 106.07) * mm, v(69.04, 108.4) * mm, v(68.13, 110) * mm]});
            skFitSpline(sketch, "E993", {"points": [v(68.13, 115.64) * mm, v(69.03, 117.13) * mm, v(69.78, 119.44) * mm, v(69.78, 120.78) * mm]});
            skFitSpline(sketch, "E994", {"points": [v(69.78, 120.78) * mm, v(69.78, 124.14) * mm, v(67.79, 124.03) * mm, v(64.35, 120.47) * mm]});
            skFitSpline(sketch, "E995", {"points": [v(64.35, 120.47) * mm, v(61.9, 117.93) * mm, v(61.7, 117.4) * mm, v(61.7, 113.43) * mm]});
            skFitSpline(sketch, "E996", {"points": [v(61.7, 113.43) * mm, v(61.7, 107.68) * mm, v(64.85, 102.7) * mm, v(68.5, 102.63) * mm]});
            skFitSpline(sketch, "E997", {"points": [v(68.5, 102.63) * mm, v(69.46, 102.61) * mm, v(69.78, 103.16) * mm, v(69.78, 104.84) * mm]});
            skFitSpline(sketch, "E998", {"points": [v(-45.38, 108.98) * mm, v(-44.55, 110.79) * mm, v(-44.08, 112.47) * mm, v(-44.35, 112.72) * mm]});
            skFitSpline(sketch, "E999", {"points": [v(-44.35, 112.72) * mm, v(-45.01, 113.34) * mm, v(-51.42, 110.37) * mm, v(-51.42, 109.45) * mm]});
            skFitSpline(sketch, "E1000", {"points": [v(-51.42, 109.45) * mm, v(-51.42, 108.16) * mm, v(-48.88, 105.37) * mm, v(-47.87, 105.54) * mm]});
            skFitSpline(sketch, "E1001", {"points": [v(-47.87, 105.54) * mm, v(-47.34, 105.63) * mm, v(-46.22, 107.18) * mm, v(-45.38, 108.98) * mm]});
            skFitSpline(sketch, "E1002", {"points": [v(-5.96, 112.28) * mm, v(-4.83, 113.06) * mm, v(-2.53, 113.88) * mm, v(-0.85, 114.09) * mm]});
            skFitSpline(sketch, "E1003", {"points": [v(-0.85, 114.09) * mm, v(0.83, 114.3) * mm, v(2.2, 114.72) * mm, v(2.2, 115.02) * mm]});
            skFitSpline(sketch, "E1004", {"points": [v(2.2, 115.02) * mm, v(2.2, 116.26) * mm, v(-1.18, 120.42) * mm, v(-2.2, 120.43) * mm]});
            skFitSpline(sketch, "E1005", {"points": [v(-2.2, 120.43) * mm, v(-4, 120.45) * mm, v(-9.37, 115.22) * mm, v(-9.9, 112.95) * mm]});
            skFitSpline(sketch, "E1006", {"points": [v(-9.9, 112.95) * mm, v(-10.51, 110.37) * mm, v(-9.07, 110.13) * mm, v(-5.96, 112.28) * mm]});
            skFitSpline(sketch, "E1007", {"points": [v(-68.3, 114.29) * mm, v(-68.3, 115.05) * mm, v(-68.8, 115.66) * mm, v(-69.41, 115.66) * mm]});
            skFitSpline(sketch, "E1008", {"points": [v(-69.41, 115.66) * mm, v(-70.02, 115.66) * mm, v(-70.51, 115.05) * mm, v(-70.51, 114.29) * mm]});
            skFitSpline(sketch, "E1009", {"points": [v(-70.51, 114.29) * mm, v(-70.51, 113.53) * mm, v(-70.02, 112.91) * mm, v(-69.41, 112.91) * mm]});
            skFitSpline(sketch, "E1010", {"points": [v(-69.41, 112.91) * mm, v(-68.8, 112.91) * mm, v(-68.3, 113.53) * mm, v(-68.3, 114.29) * mm]});
            skFitSpline(sketch, "E1011", {"points": [v(-51.21, 115.02) * mm, v(-47.5, 115.98) * mm, v(-43.63, 119.27) * mm, v(-42.52, 122.4) * mm]});
            skFitSpline(sketch, "E1012", {"points": [v(-42.52, 122.4) * mm, v(-40.95, 126.8) * mm, v(-41.27, 133.43) * mm, v(-43.22, 137.14) * mm]});
            skFitSpline(sketch, "E1013", {"points": [v(-49.28, 140.4) * mm, v(-54.2, 140.4) * mm, v(-54.65, 139.75) * mm, v(-51.43, 137.21) * mm]});
            skFitSpline(sketch, "E1014", {"points": [v(-51.43, 137.21) * mm, v(-48.5, 134.9) * mm, v(-46.82, 129.75) * mm, v(-47.86, 126.23) * mm]});
            skFitSpline(sketch, "E1015", {"points": [v(-47.86, 126.23) * mm, v(-49.6, 120.36) * mm, v(-55.99, 117.82) * mm, v(-59.87, 121.45) * mm]});
            skFitSpline(sketch, "E1016", {"points": [v(-59.87, 121.45) * mm, v(-62.47, 123.88) * mm, v(-62.93, 126.4) * mm, v(-61.16, 128.6) * mm]});
            skFitSpline(sketch, "E1017", {"points": [v(-61.16, 128.6) * mm, v(-59.63, 130.53) * mm, v(-57.26, 131.05) * mm, v(-56.74, 129.58) * mm]});
            skFitSpline(sketch, "E1018", {"points": [v(-56.74, 129.58) * mm, v(-56.56, 129.07) * mm, v(-57.07, 128.72) * mm, v(-57.99, 128.72) * mm]});
            skFitSpline(sketch, "E1019", {"points": [v(-57.99, 128.72) * mm, v(-59.83, 128.72) * mm, v(-60.56, 127.3) * mm, v(-59.93, 124.94) * mm]});
            skFitSpline(sketch, "E1020", {"points": [v(-59.93, 124.94) * mm, v(-59.52, 123.43) * mm, v(-59.07, 123.22) * mm, v(-56.22, 123.22) * mm]});
            skFitSpline(sketch, "E1021", {"points": [v(-56.22, 123.22) * mm, v(-52.15, 123.22) * mm, v(-50.68, 124.9) * mm, v(-50.68, 129.51) * mm]});
            skFitSpline(sketch, "E1022", {"points": [v(-50.68, 129.51) * mm, v(-50.68, 133.86) * mm, v(-52.9, 135.6) * mm, v(-58.44, 135.6) * mm]});
            skFitSpline(sketch, "E1023", {"points": [v(-58.44, 135.6) * mm, v(-61.54, 135.6) * mm, v(-62.77, 135.24) * mm, v(-64.57, 133.82) * mm]});
            skFitSpline(sketch, "E1024", {"points": [v(-64.57, 133.82) * mm, v(-68.56, 130.68) * mm, v(-69.24, 124.09) * mm, v(-66.07, 119.2) * mm]});
            skFitSpline(sketch, "E1025", {"points": [v(-66.07, 119.2) * mm, v(-63.21, 114.81) * mm, v(-57.83, 113.3) * mm, v(-51.21, 115.02) * mm]});
            skFitSpline(sketch, "E1026", {"points": [v(19.63, 117.02) * mm, v(20.93, 117.76) * mm, v(23, 119.66) * mm, v(24.22, 121.24) * mm]});
            skFitSpline(sketch, "E1027", {"points": [v(24.22, 121.24) * mm, v(26.16, 123.75) * mm, v(26.44, 124.69) * mm, v(26.44, 128.65) * mm]});
            skFitSpline(sketch, "E1028", {"points": [v(26.44, 128.65) * mm, v(26.43, 132) * mm, v(25.96, 134.12) * mm, v(24.63, 136.8) * mm]});
            skFitSpline(sketch, "E1029", {"points": [v(18.03, 140.4) * mm, v(12.63, 140.4) * mm, v(11.76, 139.44) * mm, v(15.36, 137.45) * mm]});
            skFitSpline(sketch, "E1030", {"points": [v(15.36, 137.45) * mm, v(17.9, 136.05) * mm, v(20.57, 131.26) * mm, v(20.57, 128.1) * mm]});
            skFitSpline(sketch, "E1031", {"points": [v(20.57, 128.1) * mm, v(20.57, 126.44) * mm, v(19.9, 125.2) * mm, v(18.07, 123.5) * mm]});
            skFitSpline(sketch, "E1032", {"points": [v(18.07, 123.5) * mm, v(14.32, 119.99) * mm, v(10, 120.45) * mm, v(7.7, 124.62) * mm]});
            skFitSpline(sketch, "E1033", {"points": [v(7.7, 124.62) * mm, v(6.9, 126.07) * mm, v(6.78, 127.04) * mm, v(7.28, 127.92) * mm]});
            skFitSpline(sketch, "E1034", {"points": [v(7.28, 127.92) * mm, v(8.35, 129.8) * mm, v(10.11, 130.96) * mm, v(11.04, 130.43) * mm]});
            skFitSpline(sketch, "E1035", {"points": [v(11.04, 130.43) * mm, v(11.58, 130.11) * mm, v(11.34, 129.6) * mm, v(10.34, 128.95) * mm]});
            skFitSpline(sketch, "E1036", {"points": [v(10.34, 128.95) * mm, v(6.25, 126.27) * mm, v(10.88, 122.32) * mm, v(15.44, 124.6) * mm]});
            skFitSpline(sketch, "E1037", {"points": [v(15.44, 124.6) * mm, v(18.93, 126.35) * mm, v(17.52, 133.93) * mm, v(13.4, 135.52) * mm]});
            skFitSpline(sketch, "E1038", {"points": [v(13.4, 135.52) * mm, v(10.3, 136.72) * mm, v(5.8, 135.49) * mm, v(3.36, 132.78) * mm]});
            skFitSpline(sketch, "E1039", {"points": [v(3.36, 132.78) * mm, v(0.78, 129.91) * mm, v(0.67, 123.84) * mm, v(3.12, 120.47) * mm]});
            skFitSpline(sketch, "E1040", {"points": [v(3.12, 120.47) * mm, v(6.52, 115.82) * mm, v(14.57, 114.13) * mm, v(19.63, 117.02) * mm]});
            skFitSpline(sketch, "E1041", {"points": [v(-12.44, 117.73) * mm, v(-11, 118.1) * mm, v(-8.44, 119.51) * mm, v(-6.75, 120.87) * mm]});
            skFitSpline(sketch, "E1042", {"points": [v(-6.75, 120.87) * mm, v(-3.86, 123.18) * mm, v(-3.67, 123.55) * mm, v(-3.67, 126.94) * mm]});
            skFitSpline(sketch, "E1043", {"points": [v(-3.67, 126.94) * mm, v(-3.67, 129.83) * mm, v(-3.22, 131.2) * mm, v(-1.39, 133.77) * mm]});
            skFitSpline(sketch, "E1044", {"points": [v(-1.39, 133.77) * mm, v(-0.13, 135.55) * mm, v(1.52, 137.31) * mm, v(2.28, 137.7) * mm]});
            skFitSpline(sketch, "E1045", {"points": [v(2.28, 137.7) * mm, v(3.05, 138.08) * mm, v(3.67, 138.84) * mm, v(3.67, 139.4) * mm]});
            skFitSpline(sketch, "E1046", {"points": [v(3.67, 139.4) * mm, v(3.67, 140.2) * mm, v(2.46, 140.4) * mm, v(-2.29, 140.4) * mm]});
            skFitSpline(sketch, "E1047", {"points": [v(-7.7, 138.51) * mm, v(-5.56, 131.06) * mm, v(-9.86, 124.13) * mm, v(-17.45, 122.8) * mm]});
            skFitSpline(sketch, "E1048", {"points": [v(-17.45, 122.8) * mm, v(-18.88, 122.55) * mm, v(-20.9, 122.62) * mm, v(-21.94, 122.96) * mm]});
            skFitSpline(sketch, "E1049", {"points": [v(-21.94, 122.96) * mm, v(-24.37, 123.76) * mm, v(-27.18, 127.67) * mm, v(-27.18, 130.25) * mm]});
            skFitSpline(sketch, "E1050", {"points": [v(-27.18, 130.25) * mm, v(-27.18, 132.7) * mm, v(-23.64, 136.28) * mm, v(-21.23, 136.28) * mm]});
            skFitSpline(sketch, "E1051", {"points": [v(-21.23, 136.28) * mm, v(-19.17, 136.28) * mm, v(-16.9, 134.42) * mm, v(-16.9, 132.74) * mm]});
            skFitSpline(sketch, "E1052", {"points": [v(-16.9, 132.74) * mm, v(-16.9, 131.04) * mm, v(-18.1, 131.12) * mm, v(-18.58, 132.84) * mm]});
            skFitSpline(sketch, "E1053", {"points": [v(-18.58, 132.84) * mm, v(-19.01, 134.4) * mm, v(-21.92, 134.73) * mm, v(-23.36, 133.4) * mm]});
            skFitSpline(sketch, "E1054", {"points": [v(-23.36, 133.4) * mm, v(-24.72, 132.12) * mm, v(-24.4, 128.87) * mm, v(-22.77, 127.35) * mm]});
            skFitSpline(sketch, "E1055", {"points": [v(-22.77, 127.35) * mm, v(-20.52, 125.24) * mm, v(-15.18, 125.45) * mm, v(-12.73, 127.74) * mm]});
            skFitSpline(sketch, "E1056", {"points": [v(-12.73, 127.74) * mm, v(-11.07, 129.3) * mm, v(-10.88, 129.93) * mm, v(-11.2, 132.95) * mm]});
            skFitSpline(sketch, "E1057", {"points": [v(-11.2, 132.95) * mm, v(-11.4, 134.85) * mm, v(-12.2, 137.2) * mm, v(-13.01, 138.22) * mm]});
            skFitSpline(sketch, "E1058", {"points": [v(-13.01, 138.22) * mm, v(-14.42, 139.98) * mm, v(-14.76, 140.06) * mm, v(-21.3, 140.06) * mm]});
            skFitSpline(sketch, "E1059", {"points": [v(-30.35, 137.47) * mm, v(-32.14, 135.41) * mm, v(-32.65, 134.08) * mm, v(-32.87, 130.94) * mm]});
            skFitSpline(sketch, "E1060", {"points": [v(-32.87, 130.94) * mm, v(-33.12, 127.44) * mm, v(-32.88, 126.59) * mm, v(-30.72, 123.29) * mm]});
            skFitSpline(sketch, "E1061", {"points": [v(-30.72, 123.29) * mm, v(-29.26, 121.07) * mm, v(-27.25, 119.06) * mm, v(-25.72, 118.3) * mm]});
            skFitSpline(sketch, "E1062", {"points": [v(-25.72, 118.3) * mm, v(-22.87, 116.9) * mm, v(-16.68, 116.62) * mm, v(-12.44, 117.73) * mm]});
            skFitSpline(sketch, "E1063", {"points": [v(-37.18, 118.77) * mm, v(-34.22, 119.92) * mm, v(-34.14, 120.11) * mm, v(-35.44, 122.74) * mm]});
            skFitSpline(sketch, "E1064", {"points": [v(-35.44, 122.74) * mm, v(-36.5, 124.85) * mm, v(-37.84, 125.15) * mm, v(-38.42, 123.4) * mm]});
            skFitSpline(sketch, "E1065", {"points": [v(-38.42, 123.4) * mm, v(-38.63, 122.73) * mm, v(-39.14, 121.19) * mm, v(-39.55, 119.96) * mm]});
            skFitSpline(sketch, "E1066", {"points": [v(-39.55, 119.96) * mm, v(-39.96, 118.73) * mm, v(-40.2, 117.73) * mm, v(-40.07, 117.73) * mm]});
            skFitSpline(sketch, "E1067", {"points": [v(-40.07, 117.73) * mm, v(-39.94, 117.73) * mm, v(-38.65, 118.2) * mm, v(-37.18, 118.77) * mm]});
            skFitSpline(sketch, "E1068", {"points": [v(59.41, 120.87) * mm, v(60.56, 123.82) * mm, v(60.28, 124.18) * mm, v(57.34, 123.58) * mm]});
            skFitSpline(sketch, "E1069", {"points": [v(57.34, 123.58) * mm, v(54.98, 123.1) * mm, v(54.55, 122) * mm, v(55.85, 119.74) * mm]});
            skFitSpline(sketch, "E1070", {"points": [v(55.85, 119.74) * mm, v(57, 117.72) * mm, v(58.36, 118.15) * mm, v(59.41, 120.87) * mm]});
            skFitSpline(sketch, "E1071", {"points": [v(35.34, 127.16) * mm, v(39.08, 128.4) * mm, v(39.54, 129.18) * mm, v(38.02, 131.69) * mm]});
            skFitSpline(sketch, "E1072", {"points": [v(38.02, 131.69) * mm, v(37.52, 132.51) * mm, v(36.76, 134.27) * mm, v(36.33, 135.6) * mm]});
            skFitSpline(sketch, "E1073", {"points": [v(36.33, 135.6) * mm, v(35.57, 137.93) * mm, v(35.45, 138) * mm, v(32.28, 137.76) * mm]});
            skFitSpline(sketch, "E1074", {"points": [v(32.28, 137.76) * mm, v(30.48, 137.63) * mm, v(28.88, 137.4) * mm, v(28.72, 137.26) * mm]});
            skFitSpline(sketch, "E1075", {"points": [v(28.72, 137.26) * mm, v(28.55, 137.1) * mm, v(28.96, 135.4) * mm, v(29.63, 133.46) * mm]});
            skFitSpline(sketch, "E1076", {"points": [v(29.63, 133.46) * mm, v(30.3, 131.52) * mm, v(30.85, 129.04) * mm, v(30.85, 127.95) * mm]});
            skFitSpline(sketch, "E1077", {"points": [v(30.85, 127.95) * mm, v(30.85, 125.62) * mm, v(30.75, 125.64) * mm, v(35.34, 127.16) * mm]});
            skFitSpline(sketch, "E1078", {"points": [v(58.77, 128.62) * mm, v(62.4, 130.43) * mm, v(64.64, 133.77) * mm, v(64.64, 137.41) * mm]});
            skFitSpline(sketch, "E1079", {"points": [v(61.7, 140.4) * mm, v(58.84, 140.4) * mm, v(58.76, 140.34) * mm, v(58.76, 138.05) * mm]});
            skFitSpline(sketch, "E1080", {"points": [v(58.76, 138.05) * mm, v(58.76, 135.38) * mm, v(56.07, 132.84) * mm, v(53.25, 132.84) * mm]});
            skFitSpline(sketch, "E1081", {"points": [v(53.25, 132.84) * mm, v(50.99, 132.84) * mm, v(47.77, 135.37) * mm, v(46.54, 138.11) * mm]});
            skFitSpline(sketch, "E1082", {"points": [v(46.54, 138.11) * mm, v(45.66, 140.09) * mm, v(45.17, 140.4) * mm, v(42.96, 140.4) * mm]});
            skFitSpline(sketch, "E1083", {"points": [v(42.96, 140.4) * mm, v(39.98, 140.4) * mm, v(39.67, 139.25) * mm, v(41.53, 135.08) * mm]});
            skFitSpline(sketch, "E1084", {"points": [v(41.53, 135.08) * mm, v(44.6, 128.21) * mm, v(52.21, 125.36) * mm, v(58.77, 128.62) * mm]});
            skFitSpline(sketch, "E1085", {"points": [v(69.64, 130.95) * mm, v(69.9, 133.12) * mm, v(68.61, 133.47) * mm, v(67.13, 131.64) * mm]});
            skFitSpline(sketch, "E1086", {"points": [v(67.13, 131.64) * mm, v(65.62, 129.78) * mm, v(65.89, 128.6) * mm, v(67.76, 128.84) * mm]});
            skFitSpline(sketch, "E1087", {"points": [v(67.76, 128.84) * mm, v(68.94, 129) * mm, v(69.48, 129.6) * mm, v(69.64, 130.95) * mm]});
            skFitSpline(sketch, "E1088", {"points": [v(-36.14, 136.5) * mm, v(-34.8, 139.95) * mm, v(-35, 140.4) * mm, v(-37.83, 140.4) * mm]});
            skFitSpline(sketch, "E1089", {"points": [v(-37.83, 140.4) * mm, v(-40.68, 140.4) * mm, v(-41.14, 139.23) * mm, v(-39.55, 135.97) * mm]});
            skFitSpline(sketch, "E1090", {"points": [v(-39.55, 135.97) * mm, v(-38.38, 133.58) * mm, v(-37.2, 133.77) * mm, v(-36.14, 136.5) * mm]});
            skFitSpline(sketch, "E1091", {"points": [v(56.95, 136.32) * mm, v(57.21, 136.72) * mm, v(57.23, 137.8) * mm, v(56.98, 138.72) * mm]});
            skFitSpline(sketch, "E1092", {"points": [v(56.98, 138.72) * mm, v(56.59, 140.2) * mm, v(56.12, 140.4) * mm, v(53.24, 140.4) * mm]});
            skFitSpline(sketch, "E1093", {"points": [v(53.24, 140.4) * mm, v(50.3, 140.4) * mm, v(49.95, 140.24) * mm, v(49.95, 138.82) * mm]});
            skFitSpline(sketch, "E1094", {"points": [v(49.95, 138.82) * mm, v(49.95, 137.95) * mm, v(50.34, 136.87) * mm, v(50.83, 136.42) * mm]});
            skFitSpline(sketch, "E1095", {"points": [v(50.83, 136.42) * mm, v(51.92, 135.4) * mm, v(56.3, 135.33) * mm, v(56.95, 136.32) * mm]});
            skFitSpline(sketch, "E1096", {"points": [v(-67.45, 137.42) * mm, v(-65.41, 139.14) * mm, v(-65.78, 140.4) * mm, v(-68.3, 140.4) * mm]});
            skFitSpline(sketch, "E1097", {"points": [v(-68.3, 140.4) * mm, v(-70.27, 140.4) * mm, v(-70.51, 140.17) * mm, v(-70.51, 138.34) * mm]});
            skFitSpline(sketch, "E1098", {"points": [v(-70.51, 138.34) * mm, v(-70.51, 136.04) * mm, v(-69.46, 135.72) * mm, v(-67.45, 137.42) * mm]});
            skArc(sketch, "E1099", {"start": v(-32.32, -122.82) * mm, "mid": v(-25.72, -126.1) * mm, "end": v(-18.36, -125.92) * mm});
            skSolve(sketch);
        }
        {
            var Q0;
            {var subQ48=sQuery(id+"F0.wireOp",EDGE,"E7");Q0=makeQuery(id+"F0.imprint","IMPRINT",FACE,{"disambiguationData":[TD([[makeQuery(id+"F0.imprint","IMPRINT",EDGE,{"derivedFrom":subQ48}),-1.0]])]});}
            extrude(context, id + "F1", {"entities" : qUnion([Q0]), "depth" : 4 * mm, "offsetDistance" : 25 * mm});
        }
    });
